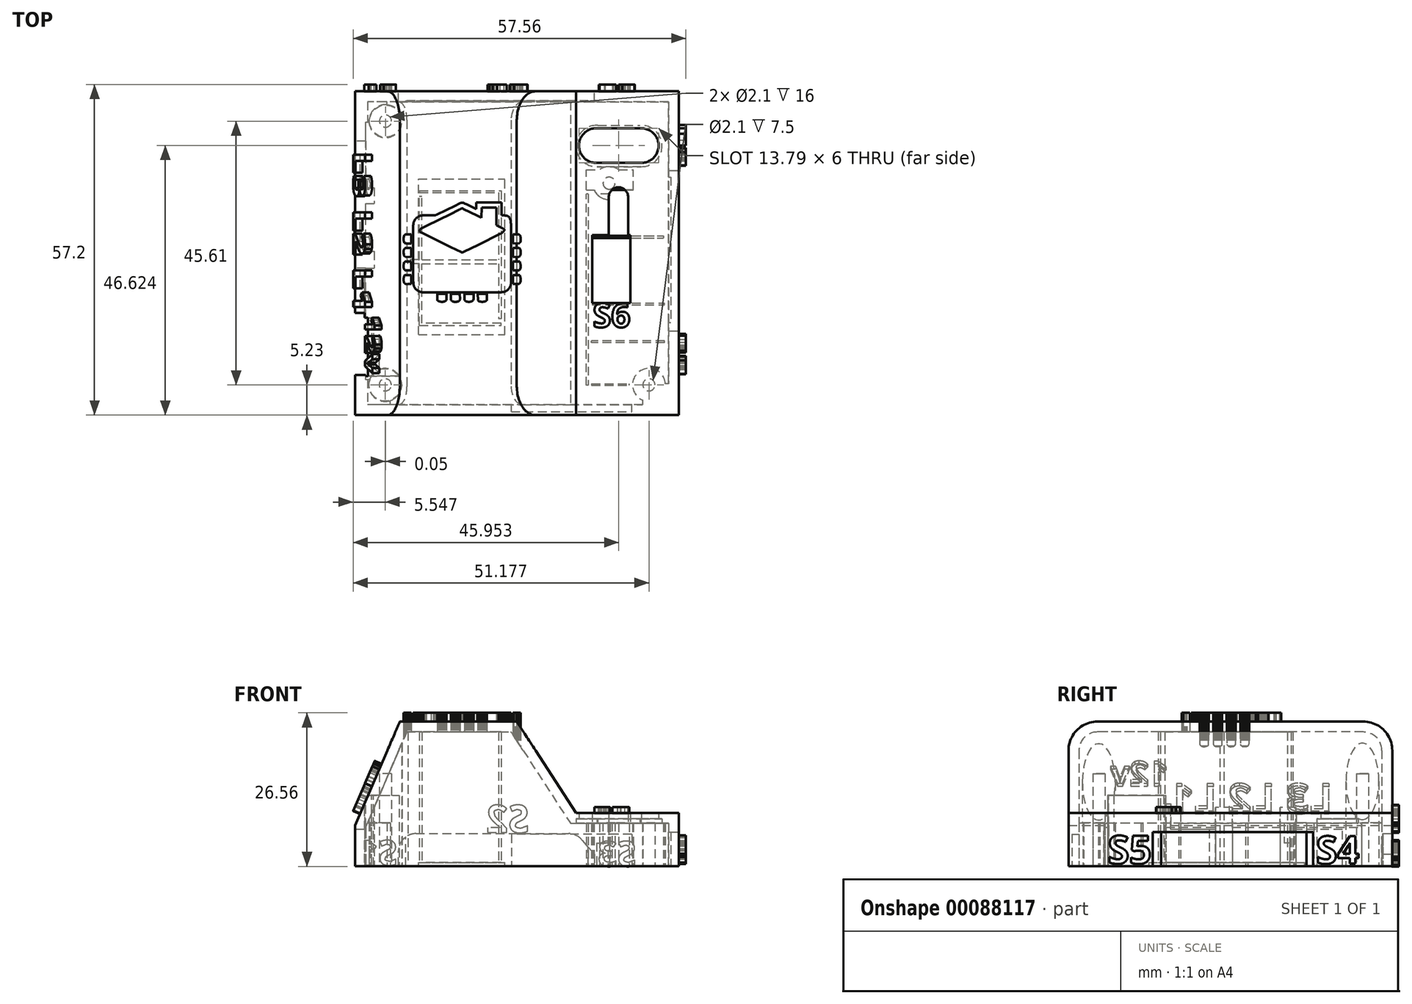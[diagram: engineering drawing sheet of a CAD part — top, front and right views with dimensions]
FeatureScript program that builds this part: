
annotation { "Feature Type Name" : "Feature", "Feature Type Description" : "" }
export const myFeature = defineFeature(function(context is Context, id is Id, definition is map)
    precondition{}
    {
        {
            var Q0;
            Q0=qCreatedBy(makeId("Top.planeOp"),FACE);
            var sketch = newSketch(context, id + "F0", { "sketchPlane" : qUnion([Q0])});
            skLineSegment(sketch, "E0.rect.bottom", {"start": v(22.84, -21.13) * mm, "end": v(-26.83, -21.13) * mm});
            skLineSegment(sketch, "E0.rect.top", {"start": v(22.84, 28.7) * mm, "end": v(-26.83, 28.7) * mm});
            skLineSegment(sketch, "E0.rect.left", {"start": v(22.84, -21.13) * mm, "end": v(22.84, 28.7) * mm});
            skPoint(sketch, "E0.rect.middle", {"position": v(-2, 3.78) * mm});
            skCircle(sketch, "E1", {"center": v(-24.81, -18.99) * mm, "radius": 1.05 * mm});
            skCircle(sketch, "E2", {"center": v(-24.76, 26.62) * mm, "radius": 1.05 * mm});
            skCircle(sketch, "E3", {"center": v(13.92, 15.91) * mm, "radius": 1.05 * mm});
            skLineSegment(sketch, "E4", {"start": v(-2, -21.13) * mm, "end": v(-2, -18.21) * mm});
            skCircle(sketch, "E5.MirrorC", {"center": v(20.82, -18.99) * mm, "radius": 1.05 * mm});
            skLineSegment(sketch, "E6.rect.bottom", {"start": v(24.75, -22.97) * mm, "end": v(-28.75, -22.97) * mm});
            skLineSegment(sketch, "E6.rect.top", {"start": v(24.75, 30.53) * mm, "end": v(-28.75, 30.53) * mm});
            skLineSegment(sketch, "E6.rect.left", {"start": v(24.75, -22.97) * mm, "end": v(24.75, 30.53) * mm});
            skLineSegment(sketch, "E6.rect.right", {"start": v(-28.75, -22.97) * mm, "end": v(-28.75, 30.53) * mm});
            skLineSegment(sketch, "E7.rect.bottom", {"start": v(26, -24.22) * mm, "end": v(-30, -24.22) * mm});
            skLineSegment(sketch, "E7.rect.top", {"start": v(26, 31.78) * mm, "end": v(-30, 31.78) * mm});
            skLineSegment(sketch, "E7.rect.left", {"start": v(26, -24.22) * mm, "end": v(26, 31.78) * mm});
            skLineSegment(sketch, "E7.rect.right", {"start": v(-30, -24.22) * mm, "end": v(-30, 31.78) * mm});
            skPoint(sketch, "E8", {"position": v(8.65, 14) * mm});
            skSolve(sketch);
        }
        {
            var Q0;
            Q0=qSketchRegion(id+"F0",true);
            var Q1;
            Q1=makeQuery(id+"F0.imprint","IMPRINT",FACE,{"disambiguationData":[TD([[makeQuery(id+"F0.imprint","IMPRINT",EDGE,{"derivedFrom":sQuery(id+"F0.wireOp",EDGE,"E1")}),-1.0]])]});
            extrude(context, id + "F1", {"entities" : qUnion([Q0, Q1]), "depth" : 25 * mm});
        }
        {
            var Q0;
            Q0=qCreatedBy(makeId("Front.planeOp"),FACE);
            var sketch = newSketch(context, id + "F2", { "sketchPlane" : qUnion([Q0])});
            skLineSegment(sketch, "E9", {"start": v(0, 0) * mm, "end": v(0, 7) * mm});
            skLineSegment(sketch, "E10", {"start": v(0, 7) * mm, "end": v(26.03, 7) * mm});
            skLineSegment(sketch, "E11", {"start": v(26.03, 9.19) * mm, "end": v(26.03, 25.51) * mm});
            skLineSegment(sketch, "E12", {"start": v(15.3, 7) * mm, "end": v(26.03, 7) * mm});
            skLineSegment(sketch, "E13", {"start": v(0, 7) * mm, "end": v(-30.02, 7) * mm});
            skLineSegment(sketch, "E14", {"start": v(-30.02, 7) * mm, "end": v(-22.06, 25.51) * mm});
            skLineSegment(sketch, "E15", {"start": v(-22.06, 25.51) * mm, "end": v(-2.39, 25.51) * mm});
            skLineSegment(sketch, "E16", {"start": v(26.03, 25.51) * mm, "end": v(-2.39, 25.51) * mm});
            skLineSegment(sketch, "E17", {"start": v(-22.06, 25.51) * mm, "end": v(-30.02, 25.51) * mm});
            skLineSegment(sketch, "E18", {"start": v(-30.02, 25.51) * mm, "end": v(-30.02, 7) * mm});
            skLineSegment(sketch, "E19", {"start": v(18.06, 10.7) * mm, "end": v(18.04, 10.7) * mm});
            skLineSegment(sketch, "E20", {"start": v(19.86, 9.19) * mm, "end": v(8.2, 9.19) * mm});
            skLineSegment(sketch, "E21", {"start": v(8.2, 9.19) * mm, "end": v(-2.39, 25.51) * mm});
            skLineSegment(sketch, "E22", {"start": v(19.86, 9.19) * mm, "end": v(26.03, 9.19) * mm});
            skSolve(sketch);
        }
        {
            var Q0;
            Q0=makeQuery(id+"F2.imprint","IMPRINT",FACE,{"disambiguationData":[TD([[makeQuery(id+"F2.imprint","IMPRINT",EDGE,{"derivedFrom":sQuery(id+"F2.wireOp",EDGE,"E14")}),1.0]])]});
            var Q1;
            {var subQ0=sQuery(id+"F2.wireOp",EDGE,"E11");Q1=makeQuery(id+"F2.imprint","IMPRINT",FACE,{"disambiguationData":[TD([[makeQuery(id+"F2.imprint","IMPRINT",EDGE,{"derivedFrom":subQ0}),1.0]])]});}
            extrude(context, id + "F3", {"entities" : qUnion([Q0, Q1]), "operationType" : NewBodyOperationType.REMOVE, "endBound" : BoundingType.UP_TO_NEXT, "oppositeDirection" : true, "depth" : 25 * mm, "hasSecondDirection" : true, "secondDirectionOppositeDirection" : false, "secondDirectionDepth" : 25 * mm});
        }
        {
            var Q0;
            Q0=makeQuery(id+"F1.opExtrude","CAP_EDGE",EDGE,{"disambiguationData":[OSD([sQuery(id+"F0.wireOp",EDGE,"E7.rect.right")])],"isStart":false});
            var Q1;
            Q1=makeQuery(id+"F3.boolean.opBoolean","COPY",EDGE,{"derivedFrom":makeQuery(id+"F3.opExtrude","TWEAK_EDGE",EDGE,{"derivedFrom":[makeQuery(id+"F1.opExtrude","CAP_FACE",FACE,{"disambiguationData":[OSD([sQuery(id+"F0.wireOp",EDGE,"E1"),sQuery(id+"F0.wireOp",EDGE,"E2"),sQuery(id+"F0.wireOp",EDGE,"E3"),sQuery(id+"F0.wireOp",EDGE,"E5.MirrorC"),sQuery(id+"F0.wireOp",EDGE,"E7.rect.bottom"),sQuery(id+"F0.wireOp",EDGE,"E7.rect.top"),sQuery(id+"F0.wireOp",EDGE,"E7.rect.left"),sQuery(id+"F0.wireOp",EDGE,"E7.rect.right")])],"isStart":false}),makeQuery(id+"F2.imprint","IMPRINT",EDGE,{"derivedFrom":sQuery(id+"F2.wireOp",EDGE,"ff17f17f-c23f-4b7b-92e3-773d52701edb")})]})});
            var Q2;
            Q2=makeQuery(id+"F3.boolean.opBoolean","COPY",EDGE,{"derivedFrom":makeQuery(id+"F3.opExtrude","TWEAK_EDGE",EDGE,{"derivedFrom":[makeQuery(id+"F1.opExtrude","CAP_FACE",FACE,{"disambiguationData":[OSD([sQuery(id+"F0.wireOp",EDGE,"E1"),sQuery(id+"F0.wireOp",EDGE,"E2"),sQuery(id+"F0.wireOp",EDGE,"E3"),sQuery(id+"F0.wireOp",EDGE,"E5.MirrorC"),sQuery(id+"F0.wireOp",EDGE,"E7.rect.bottom"),sQuery(id+"F0.wireOp",EDGE,"E7.rect.top"),sQuery(id+"F0.wireOp",EDGE,"E7.rect.left"),sQuery(id+"F0.wireOp",EDGE,"E7.rect.right")])],"isStart":false}),makeQuery(id+"F2.imprint","IMPRINT",EDGE,{"derivedFrom":sQuery(id+"F2.wireOp",EDGE,"7c30f75c-de24-4105-9ec6-0528e7197d9e")})]})});
            var Q3;
            {var subQ0=sQuery(id+"F2.wireOp",EDGE,"cpQ2IQLn-lepx-jHqE-Occg-QwCyzWVKbBFz");var subQ1=sQuery(id+"F2.wireOp",EDGE,"9136473a-ce9f-4df1-8e41-d79c079f6f02");var subQ2=makeQuery(id+"F2.imprint","INTERSECT",VERTEX,{"disambiguationData":[OD(0.0)],"derivedFrom":[subQ1,subQ0]});var subQ4=makeQuery(id+"F2.imprint","INTERSECT",VERTEX,{"disambiguationData":[OD(1.0)],"derivedFrom":[subQ1,subQ0]});Q3=makeQuery(id+"F3.boolean.opBoolean","COPY",EDGE,{"derivedFrom":makeQuery(id+"F3.opExtrude","TWEAK_EDGE",EDGE,{"derivedFrom":[makeQuery(id+"F1.opExtrude","CAP_FACE",FACE,{"disambiguationData":[OSD([sQuery(id+"F0.wireOp",EDGE,"E1"),sQuery(id+"F0.wireOp",EDGE,"E2"),sQuery(id+"F0.wireOp",EDGE,"E3"),sQuery(id+"F0.wireOp",EDGE,"E5.MirrorC"),sQuery(id+"F0.wireOp",EDGE,"E7.rect.bottom"),sQuery(id+"F0.wireOp",EDGE,"E7.rect.top"),sQuery(id+"F0.wireOp",EDGE,"E7.rect.left"),sQuery(id+"F0.wireOp",EDGE,"E7.rect.right")])],"isStart":false}),makeQuery(id+"F2.imprint","IMPRINT",EDGE,{"disambiguationData":[TD([[subQ4,1.0]])],"derivedFrom":subQ0}),makeQuery(id+"F2.imprint","IMPRINT",EDGE,{"disambiguationData":[TD([[subQ2,1.0]])],"derivedFrom":subQ0}),makeQuery(id+"F2.imprint","IMPRINT",EDGE,{"disambiguationData":[TD([[subQ2,-1.0]])],"derivedFrom":subQ0})]})});}
            var Q4;
            {var subQ0=sQuery(id+"F2.wireOp",EDGE,"cpQ2IQLn-lepx-jHqE-Occg-QwCyzWVKbBFz");var subQ1=sQuery(id+"F2.wireOp",EDGE,"9136473a-ce9f-4df1-8e41-d79c079f6f02");var subQ2=makeQuery(id+"F2.imprint","INTERSECT",VERTEX,{"disambiguationData":[OD(0.0)],"derivedFrom":[subQ1,subQ0]});var subQ3=sQuery(id+"F2.wireOp",EDGE,"7c30f75c-de24-4105-9ec6-0528e7197d9e");var subQ4=makeQuery(id+"F2.imprint","INTERSECT",VERTEX,{"derivedFrom":[subQ3,subQ0]});var subQ5=makeQuery(id+"F2.imprint","INTERSECT",VERTEX,{"disambiguationData":[OD(1.0)],"derivedFrom":[subQ1,subQ0]});Q4=makeQuery(id+"F3.boolean.opBoolean","COPY",EDGE,{"derivedFrom":makeQuery(id+"F3.opExtrude","TWEAK_EDGE",EDGE,{"disambiguationData":[OD(0.0)],"derivedFrom":[makeQuery(id+"F2.imprint","IMPRINT",EDGE,{"disambiguationData":[TD([[subQ4,1.0]])],"derivedFrom":subQ3}),makeQuery(id+"F2.imprint","IMPRINT",EDGE,{"disambiguationData":[TD([[subQ5,1.0]])],"derivedFrom":subQ0}),makeQuery(id+"F2.imprint","IMPRINT",EDGE,{"disambiguationData":[TD([[subQ2,1.0]])],"derivedFrom":subQ0}),makeQuery(id+"F2.imprint","IMPRINT",EDGE,{"disambiguationData":[TD([[subQ2,-1.0]])],"derivedFrom":subQ0})]})});}
            var Q5;
            {var subQ0=sQuery(id+"F2.wireOp",EDGE,"cpQ2IQLn-lepx-jHqE-Occg-QwCyzWVKbBFz");var subQ1=sQuery(id+"F2.wireOp",EDGE,"9136473a-ce9f-4df1-8e41-d79c079f6f02");var subQ2=makeQuery(id+"F2.imprint","INTERSECT",VERTEX,{"disambiguationData":[OD(0.0)],"derivedFrom":[subQ1,subQ0]});var subQ3=sQuery(id+"F2.wireOp",EDGE,"7c30f75c-de24-4105-9ec6-0528e7197d9e");var subQ4=makeQuery(id+"F2.imprint","INTERSECT",VERTEX,{"derivedFrom":[subQ3,subQ0]});var subQ5=makeQuery(id+"F2.imprint","INTERSECT",VERTEX,{"disambiguationData":[OD(1.0)],"derivedFrom":[subQ1,subQ0]});Q5=makeQuery(id+"F3.boolean.opBoolean","COPY",EDGE,{"derivedFrom":makeQuery(id+"F3.opExtrude","TWEAK_EDGE",EDGE,{"disambiguationData":[OD(1.0)],"derivedFrom":[makeQuery(id+"F2.imprint","IMPRINT",EDGE,{"disambiguationData":[TD([[subQ4,1.0]])],"derivedFrom":subQ3}),makeQuery(id+"F2.imprint","IMPRINT",EDGE,{"disambiguationData":[TD([[subQ5,1.0]])],"derivedFrom":subQ0}),makeQuery(id+"F2.imprint","IMPRINT",EDGE,{"disambiguationData":[TD([[subQ2,1.0]])],"derivedFrom":subQ0}),makeQuery(id+"F2.imprint","IMPRINT",EDGE,{"disambiguationData":[TD([[subQ2,-1.0]])],"derivedFrom":subQ0})]})});}
            var Q6;
            Q6=makeQuery(id+"F1.opExtrude","CAP_EDGE",EDGE,{"disambiguationData":[OSD([sQuery(id+"F0.wireOp",EDGE,"E7.rect.bottom")])],"isStart":false});
            var Q7;
            {var subQ0=sQuery(id+"F2.wireOp",EDGE,"cpQ2IQLn-lepx-jHqE-Occg-QwCyzWVKbBFz");var subQ1=sQuery(id+"F2.wireOp",EDGE,"9136473a-ce9f-4df1-8e41-d79c079f6f02");var subQ2=makeQuery(id+"F2.imprint","INTERSECT",VERTEX,{"disambiguationData":[OD(0.0)],"derivedFrom":[subQ1,subQ0]});var subQ4=makeQuery(id+"F2.imprint","INTERSECT",VERTEX,{"disambiguationData":[OD(1.0)],"derivedFrom":[subQ1,subQ0]});Q7=makeQuery(id+"F3.boolean.opBoolean","COPY",EDGE,{"derivedFrom":makeQuery(id+"F3.opExtrude","TWEAK_EDGE",EDGE,{"derivedFrom":[makeQuery(id+"F1.opExtrude","SWEPT_FACE",FACE,{"disambiguationData":[OSD([sQuery(id+"F0.wireOp",EDGE,"E7.rect.bottom")])]}),makeQuery(id+"F2.imprint","IMPRINT",EDGE,{"disambiguationData":[TD([[subQ4,1.0]])],"derivedFrom":subQ0}),makeQuery(id+"F2.imprint","IMPRINT",EDGE,{"disambiguationData":[TD([[subQ2,1.0]])],"derivedFrom":subQ0}),makeQuery(id+"F2.imprint","IMPRINT",EDGE,{"disambiguationData":[TD([[subQ2,-1.0]])],"derivedFrom":subQ0})]})});}
            var Q8;
            Q8=makeQuery(id+"F1.opExtrude","CAP_EDGE",EDGE,{"disambiguationData":[OSD([sQuery(id+"F0.wireOp",EDGE,"E7.rect.top")])],"isStart":false});
            var Q9;
            {var subQ0=sQuery(id+"F2.wireOp",EDGE,"cpQ2IQLn-lepx-jHqE-Occg-QwCyzWVKbBFz");var subQ1=sQuery(id+"F2.wireOp",EDGE,"9136473a-ce9f-4df1-8e41-d79c079f6f02");var subQ2=makeQuery(id+"F2.imprint","INTERSECT",VERTEX,{"disambiguationData":[OD(0.0)],"derivedFrom":[subQ1,subQ0]});var subQ4=makeQuery(id+"F2.imprint","INTERSECT",VERTEX,{"disambiguationData":[OD(1.0)],"derivedFrom":[subQ1,subQ0]});Q9=makeQuery(id+"F3.boolean.opBoolean","COPY",EDGE,{"derivedFrom":makeQuery(id+"F3.opExtrude","TWEAK_EDGE",EDGE,{"derivedFrom":[makeQuery(id+"F1.opExtrude","SWEPT_FACE",FACE,{"disambiguationData":[OSD([sQuery(id+"F0.wireOp",EDGE,"E7.rect.top")])]}),makeQuery(id+"F2.imprint","IMPRINT",EDGE,{"disambiguationData":[TD([[subQ4,1.0]])],"derivedFrom":subQ0}),makeQuery(id+"F2.imprint","IMPRINT",EDGE,{"disambiguationData":[TD([[subQ2,1.0]])],"derivedFrom":subQ0}),makeQuery(id+"F2.imprint","IMPRINT",EDGE,{"disambiguationData":[TD([[subQ2,-1.0]])],"derivedFrom":subQ0})]})});}
            var Q10;
            Q10=makeQuery(id+"F3.boolean.opBoolean","COPY",EDGE,{"derivedFrom":makeQuery(id+"F3.opExtrude","TWEAK_EDGE",EDGE,{"derivedFrom":[makeQuery(id+"F1.opExtrude","CAP_FACE",FACE,{"disambiguationData":[OSD([sQuery(id+"F0.wireOp",EDGE,"E1"),sQuery(id+"F0.wireOp",EDGE,"E2"),sQuery(id+"F0.wireOp",EDGE,"E3"),sQuery(id+"F0.wireOp",EDGE,"E5.MirrorC"),sQuery(id+"F0.wireOp",EDGE,"E7.rect.bottom"),sQuery(id+"F0.wireOp",EDGE,"E7.rect.top"),sQuery(id+"F0.wireOp",EDGE,"E7.rect.left"),sQuery(id+"F0.wireOp",EDGE,"E7.rect.right")])],"isStart":false}),makeQuery(id+"F2.imprint","IMPRINT",EDGE,{"derivedFrom":sQuery(id+"F2.wireOp",EDGE,"99fa5713-44e2-4710-8a3e-a5a5802f03ed")})]})});
            var Q11;
            Q11=makeQuery(id+"F3.boolean.opBoolean","COPY",EDGE,{"derivedFrom":makeQuery(id+"F3.opExtrude","TWEAK_EDGE",EDGE,{"derivedFrom":[makeQuery(id+"F1.opExtrude","CAP_FACE",FACE,{"disambiguationData":[OSD([sQuery(id+"F0.wireOp",EDGE,"E1"),sQuery(id+"F0.wireOp",EDGE,"E2"),sQuery(id+"F0.wireOp",EDGE,"E3"),sQuery(id+"F0.wireOp",EDGE,"E5.MirrorC"),sQuery(id+"F0.wireOp",EDGE,"E7.rect.bottom"),sQuery(id+"F0.wireOp",EDGE,"E7.rect.top"),sQuery(id+"F0.wireOp",EDGE,"E7.rect.left"),sQuery(id+"F0.wireOp",EDGE,"E7.rect.right")])],"isStart":false}),makeQuery(id+"F2.imprint","IMPRINT",EDGE,{"derivedFrom":sQuery(id+"F2.wireOp",EDGE,"E14")})]})});
            var Q12;
            Q12=makeQuery(id+"F3.boolean.opBoolean","COPY",EDGE,{"derivedFrom":makeQuery(id+"F3.opExtrude","TWEAK_EDGE",EDGE,{"derivedFrom":[makeQuery(id+"F1.opExtrude","CAP_FACE",FACE,{"disambiguationData":[OSD([sQuery(id+"F0.wireOp",EDGE,"E1"),sQuery(id+"F0.wireOp",EDGE,"E2"),sQuery(id+"F0.wireOp",EDGE,"E3"),sQuery(id+"F0.wireOp",EDGE,"E5.MirrorC"),sQuery(id+"F0.wireOp",EDGE,"E7.rect.bottom"),sQuery(id+"F0.wireOp",EDGE,"E7.rect.top"),sQuery(id+"F0.wireOp",EDGE,"E7.rect.left"),sQuery(id+"F0.wireOp",EDGE,"E7.rect.right")])],"isStart":false}),makeQuery(id+"F2.imprint","IMPRINT",EDGE,{"derivedFrom":sQuery(id+"F2.wireOp",EDGE,"E21")})]})});
            var Q13;
            Q13=makeQuery(id+"F3.boolean.opBoolean","COPY",EDGE,{"derivedFrom":makeQuery(id+"F3.opExtrude","TWEAK_EDGE",EDGE,{"derivedFrom":[makeQuery(id+"F2.imprint","IMPRINT",EDGE,{"derivedFrom":sQuery(id+"F2.wireOp",EDGE,"E20")}),makeQuery(id+"F2.imprint","IMPRINT",EDGE,{"derivedFrom":sQuery(id+"F2.wireOp",EDGE,"E21")})]})});
            var Q14;
            Q14=makeQuery(id+"F3.boolean.opBoolean","COPY",EDGE,{"derivedFrom":makeQuery(id+"F3.opExtrude","TWEAK_EDGE",EDGE,{"derivedFrom":[makeQuery(id+"F1.opExtrude","SWEPT_FACE",FACE,{"disambiguationData":[OSD([sQuery(id+"F0.wireOp",EDGE,"E7.rect.bottom")])]}),makeQuery(id+"F2.imprint","IMPRINT",EDGE,{"derivedFrom":sQuery(id+"F2.wireOp",EDGE,"E21")})]})});
            var Q15;
            Q15=makeQuery(id+"F3.boolean.opBoolean","COPY",EDGE,{"derivedFrom":makeQuery(id+"F3.opExtrude","TWEAK_EDGE",EDGE,{"derivedFrom":[makeQuery(id+"F1.opExtrude","SWEPT_FACE",FACE,{"disambiguationData":[OSD([sQuery(id+"F0.wireOp",EDGE,"E7.rect.top")])]}),makeQuery(id+"F2.imprint","IMPRINT",EDGE,{"derivedFrom":sQuery(id+"F2.wireOp",EDGE,"E21")})]})});
            var Q16;
            Q16=makeQuery(id+"F3.boolean.opBoolean","COPY",EDGE,{"derivedFrom":makeQuery(id+"F3.opExtrude","TWEAK_EDGE",EDGE,{"derivedFrom":[makeQuery(id+"F1.opExtrude","SWEPT_FACE",FACE,{"disambiguationData":[OSD([sQuery(id+"F0.wireOp",EDGE,"E7.rect.left")])]}),makeQuery(id+"F2.imprint","IMPRINT",EDGE,{"derivedFrom":sQuery(id+"F2.wireOp",EDGE,"E20")}),makeQuery(id+"F2.imprint","IMPRINT",EDGE,{"derivedFrom":sQuery(id+"F2.wireOp",EDGE,"E22")})]})});
            var Q17;
            Q17=makeQuery(id+"F3.boolean.opBoolean","COPY",EDGE,{"derivedFrom":makeQuery(id+"F3.opExtrude","TWEAK_EDGE",EDGE,{"derivedFrom":[makeQuery(id+"F2.imprint","IMPRINT",EDGE,{"derivedFrom":sQuery(id+"F2.wireOp",EDGE,"E20")}),makeQuery(id+"F2.imprint","IMPRINT",EDGE,{"derivedFrom":sQuery(id+"F2.wireOp",EDGE,"E21")}),makeQuery(id+"F2.imprint","IMPRINT",EDGE,{"derivedFrom":sQuery(id+"F2.wireOp",EDGE,"E22")})]})});
            fillet(context, id + "F4", {"entities" : qUnion([Q0, Q1, Q2, Q3, Q4, Q5, Q6, Q7, Q8, Q9, Q10, Q11, Q12, Q13, Q14, Q15, Q16, Q17]), "radius" : 5 * mm, "tangentPropagation" : true, "allowEdgeOverflow" : false});
        }
        {
            var Q0;
            Q0=makeQuery(id+"F1.opExtrude","SWEPT_BODY",BODY,{"disambiguationData":[OSD([sQuery(id+"F0.wireOp",EDGE,"E1"),sQuery(id+"F0.wireOp",EDGE,"E2"),sQuery(id+"F0.wireOp",EDGE,"E3"),sQuery(id+"F0.wireOp",EDGE,"E5.MirrorC"),sQuery(id+"F0.wireOp",EDGE,"E7.rect.bottom"),sQuery(id+"F0.wireOp",EDGE,"E7.rect.top"),sQuery(id+"F0.wireOp",EDGE,"E7.rect.left"),sQuery(id+"F0.wireOp",EDGE,"E7.rect.right")])]});
            transform(context, id + "F5", {"entities" : qUnion([Q0]), "transformType" : TransformType.TRANSLATION_3D, "dx" : -5 * mm, "dy" : -12 * mm, "dz" : 0 * mm, "makeCopy" : false});
        }
        {
            var Q0;
            Q0=makeQuery(id+"F1.opExtrude","CAP_FACE",FACE,{"disambiguationData":[OSD([sQuery(id+"F0.wireOp",EDGE,"E1"),sQuery(id+"F0.wireOp",EDGE,"E2"),sQuery(id+"F0.wireOp",EDGE,"E3"),sQuery(id+"F0.wireOp",EDGE,"E5.MirrorC"),sQuery(id+"F0.wireOp",EDGE,"E7.rect.bottom"),sQuery(id+"F0.wireOp",EDGE,"E7.rect.top"),sQuery(id+"F0.wireOp",EDGE,"E7.rect.left"),sQuery(id+"F0.wireOp",EDGE,"E7.rect.right")])],"isStart":true});
            shell(context, id + "F6", {"entities" : qUnion([Q0]), "thickness" : 1.8 * mm});
        }
        {
            var Q0;
            Q0=makeQuery(id+"F1.opExtrude","SWEPT_FACE",FACE,{"disambiguationData":[OSD([sQuery(id+"F0.wireOp",EDGE,"E7.rect.left")])]});
            cPlane(context, id + "F7", {"entities" : qUnion([Q0]), "cplaneType" : CPlaneType.OFFSET, "offset" : 0 * mm, "width" : 150 * mm, "height" : 150 * mm});
        }
        {
            var Q0;
            Q0=qCreatedBy(id+"F7.planeOp",FACE);
            var sketch = newSketch(context, id + "F8", { "sketchPlane" : qUnion([Q0])});
            skLineSegment(sketch, "E23.bottom", {"start": v(6.92, 0) * mm, "end": v(-20.2, 0) * mm});
            skLineSegment(sketch, "E23.top", {"start": v(6.12, 5.87) * mm, "end": v(-20.2, 5.87) * mm});
            skLineSegment(sketch, "E24", {"start": v(-20.2, 5.87) * mm, "end": v(-21.64, 5.87) * mm});
            skLineSegment(sketch, "E25", {"start": v(-21.64, 5.87) * mm, "end": v(-21.64, 0) * mm});
            skLineSegment(sketch, "E26", {"start": v(-21.64, 0) * mm, "end": v(-20.2, 0) * mm});
            skLineSegment(sketch, "E27", {"start": v(-20.2, 5.87) * mm, "end": v(-20.2, 0) * mm});
            skLineSegment(sketch, "E28", {"start": v(6.12, 5.87) * mm, "end": v(6.12, 0) * mm});
            skPoint(sketch, "E29.orphan", {"position": v(7.84, 0) * mm});
            skLineSegment(sketch, "E30", {"start": v(4.97, 0) * mm, "end": v(4.97, 5.87) * mm});
            skSolve(sketch);
        }
        {
            var Q0;
            Q0=qSketchRegion(id+"F8",true);
            extrude(context, id + "F9", {"entities" : qUnion([Q0]), "operationType" : NewBodyOperationType.REMOVE, "oppositeDirection" : true, "depth" : (1.7 - 0.3) * mm});
        }
        {
            var Q0;
            Q0=makeQuery(id+"F8.imprint","IMPRINT",FACE,{"disambiguationData":[TD([[makeQuery(id+"F8.imprint","IMPRINT",EDGE,{"derivedFrom":sQuery(id+"F8.wireOp",EDGE,"E24")}),1.0]])]});
            var Q1;
            {var subQ0=sQuery(id+"F8.wireOp",EDGE,"E23.left");Q1=makeQuery(id+"F8.imprint","IMPRINT",FACE,{"disambiguationData":[TD([[makeQuery(id+"F8.imprint","IMPRINT",EDGE,{"derivedFrom":subQ0}),1.0]])]});}
            var Q2;
            {var subQ0=sQuery(id+"F8.wireOp",EDGE,"4UiORLbo-slaH-JSft-xh6I-61qYCNnPId7j");Q2=makeQuery(id+"F8.imprint","IMPRINT",FACE,{"disambiguationData":[TD([[makeQuery(id+"F8.imprint","IMPRINT",EDGE,{"derivedFrom":subQ0}),1.0]])]});}
            var Q3;
            {var subQ0=sQuery(id+"F8.wireOp",EDGE,"E28");Q3=makeQuery(id+"F8.imprint","IMPRINT",FACE,{"disambiguationData":[TD([[makeQuery(id+"F8.imprint","IMPRINT",EDGE,{"derivedFrom":subQ0}),-1.0]])]});}
            extrude(context, id + "F10", {"entities" : qUnion([Q0, Q1, Q2, Q3]), "operationType" : NewBodyOperationType.REMOVE, "oppositeDirection" : true, "depth" : 2 * mm});
        }
        {
            var Q0;
            Q0=makeQuery(id+"F1.opExtrude","SWEPT_FACE",FACE,{"disambiguationData":[OSD([sQuery(id+"F0.wireOp",EDGE,"E7.rect.right")])]});
            cPlane(context, id + "F11", {"entities" : qUnion([Q0]), "cplaneType" : CPlaneType.OFFSET, "offset" : 0 * mm, "width" : 150 * mm, "height" : 150 * mm});
        }
        {
            var Q0;
            Q0=qCreatedBy(id+"F11.planeOp",FACE);
            var sketch = newSketch(context, id + "F12", { "sketchPlane" : qUnion([Q0])});
            skLineSegment(sketch, "E31.top", {"start": v(-11.15, 6.31) * mm, "end": v(-3.45, 6.31) * mm});
            skLineSegment(sketch, "E32", {"start": v(27.25, 11.15) * mm, "end": v(27.25, 11.15) * mm});
            skLineSegment(sketch, "E33", {"start": v(-11.15, 0) * mm, "end": v(-11.15, 6.31) * mm});
            skPoint(sketch, "E34.start.orphan", {"position": v(-15.15, 0) * mm});
            skLineSegment(sketch, "E35", {"start": v(29.28, 0) * mm, "end": v(-11.15, 0) * mm});
            skLineSegment(sketch, "E36", {"start": v(-10.29, 6.31) * mm, "end": v(-10.29, 0) * mm});
            skLineSegment(sketch, "E37", {"start": v(19.35, 12.2) * mm, "end": v(29.28, 12.2) * mm});
            skLineSegment(sketch, "E38", {"start": v(-11.15, 3.16) * mm, "end": v(-3.45, 3.16) * mm, "construction": true});
            skLineSegment(sketch, "E39", {"start": v(-3.45, 3.16) * mm, "end": v(-0.05, 3.16) * mm, "construction": true});
            skLineSegment(sketch, "E40", {"start": v(-0.05, 3.16) * mm, "end": v(7.65, 3.16) * mm, "construction": true});
            skLineSegment(sketch, "E41", {"start": v(7.65, 3.16) * mm, "end": v(11.05, 3.16) * mm, "construction": true});
            skLineSegment(sketch, "E42.trimOffspring", {"start": v(11.05, 6.31) * mm, "end": v(18.53, 6.31) * mm});
            skLineSegment(sketch, "E43", {"start": v(11.9, 6.31) * mm, "end": v(11.9, 0) * mm});
            skLineSegment(sketch, "E44", {"start": v(0, 6.31) * mm, "end": v(7.65, 6.31) * mm});
            skLineSegment(sketch, "E45", {"start": v(7.65, 0) * mm, "end": v(0, 0) * mm});
            skLineSegment(sketch, "E46", {"start": v(-3.45, 0) * mm, "end": v(-11.15, 0) * mm});
            skLineSegment(sketch, "E47", {"start": v(30.08, 0) * mm, "end": v(11.05, 0) * mm});
            skLineSegment(sketch, "E48.bottom", {"start": v(-0.32, 0) * mm, "end": v(-3.15, 0) * mm});
            skLineSegment(sketch, "E48.top", {"start": v(-0.32, 6.31) * mm, "end": v(-3.15, 6.31) * mm});
            skLineSegment(sketch, "E48.left", {"start": v(-0.32, 0) * mm, "end": v(-0.32, 6.31) * mm});
            skLineSegment(sketch, "E48.right", {"start": v(-3.15, 0) * mm, "end": v(-3.15, 6.31) * mm});
            skLineSegment(sketch, "E49.bottom", {"start": v(10.8, 0) * mm, "end": v(7.92, 0) * mm});
            skLineSegment(sketch, "E49.top", {"start": v(10.8, 6.31) * mm, "end": v(7.92, 6.31) * mm});
            skLineSegment(sketch, "E49.left", {"start": v(10.8, 0) * mm, "end": v(10.8, 6.31) * mm});
            skLineSegment(sketch, "E49.right", {"start": v(7.92, 0) * mm, "end": v(7.92, 6.31) * mm});
            skLineSegment(sketch, "E50", {"start": v(-3.45, 6.31) * mm, "end": v(11.05, 6.31) * mm});
            skLineSegment(sketch, "E51", {"start": v(29.28, 12.2) * mm, "end": v(29.28, 0) * mm});
            skPoint(sketch, "E52.end.orphan", {"position": v(30.08, 11.15) * mm});
            skPoint(sketch, "E52.start.orphan", {"position": v(30.08, 12.2) * mm});
            skLineSegment(sketch, "E53", {"start": v(18.53, 6.31) * mm, "end": v(18.53, 12.2) * mm});
            skLineSegment(sketch, "E54", {"start": v(18.53, 12.2) * mm, "end": v(19.35, 12.2) * mm});
            skPoint(sketch, "E55.start.orphan", {"position": v(19.35, 11.15) * mm});
            skPoint(sketch, "E56.end.orphan", {"position": v(19.35, 0) * mm});
            skPoint(sketch, "E56.start.orphan", {"position": v(19.35, 6.31) * mm});
            skLineSegment(sketch, "E57", {"start": v(28.38, 0) * mm, "end": v(28.38, 12.2) * mm});
            skLineSegment(sketch, "E58", {"start": v(19.35, 12.2) * mm, "end": v(19.35, 0) * mm});
            skSolve(sketch);
        }
        {
            var Q0;
            {var subQ0=sQuery(id+"F12.wireOp",EDGE,"E33");Q0=makeQuery(id+"F12.imprint","IMPRINT",FACE,{"disambiguationData":[TD([[makeQuery(id+"F12.imprint","IMPRINT",EDGE,{"derivedFrom":subQ0}),-1.0]])]});}
            var Q1;
            {var subQ1=sQuery(id+"F12.wireOp",EDGE,"E36");Q1=makeQuery(id+"F12.imprint","IMPRINT",FACE,{"disambiguationData":[TD([[makeQuery(id+"F12.imprint","IMPRINT",EDGE,{"derivedFrom":subQ1}),1.0]])]});}
            var Q2;
            {var subQ0=sQuery(id+"F12.wireOp",EDGE,"LVVauTd6-uSLQ-SWm0-nvuu-HrEgJgk2loCY");Q2=makeQuery(id+"F12.imprint","IMPRINT",FACE,{"disambiguationData":[TD([[makeQuery(id+"F12.imprint","IMPRINT",EDGE,{"derivedFrom":subQ0}),-1.0]])]});}
            var Q3;
            Q3=makeQuery(id+"F12.imprint","IMPRINT",FACE,{"disambiguationData":[TD([[makeQuery(id+"F12.imprint","IMPRINT",EDGE,{"derivedFrom":sQuery(id+"F12.wireOp",EDGE,"Bzj0w9RH-aYdH-ZF7y-Z4mK-Pif1xP8myCSu")}),1.0]])]});
            var Q4;
            {var subQ2=sQuery(id+"F12.wireOp",EDGE,"E43");Q4=makeQuery(id+"F12.imprint","IMPRINT",FACE,{"disambiguationData":[TD([[makeQuery(id+"F12.imprint","IMPRINT",EDGE,{"derivedFrom":subQ2}),1.0]])]});}
            extrude(context, id + "F13", {"entities" : qUnion([Q0, Q1, Q2, Q3, Q4]), "operationType" : NewBodyOperationType.REMOVE, "oppositeDirection" : true, "depth" : 1.6 * mm});
        }
        {
            var Q0;
            {var subQ2=sQuery(id+"F12.wireOp",EDGE,"E57");Q0=makeQuery(id+"F12.imprint","IMPRINT",FACE,{"disambiguationData":[TD([[makeQuery(id+"F12.imprint","IMPRINT",EDGE,{"derivedFrom":subQ2}),1.0]])]});}
            var Q1;
            {var subQ0=sQuery(id+"F12.wireOp",EDGE,"E33");Q1=makeQuery(id+"F12.imprint","IMPRINT",FACE,{"disambiguationData":[TD([[makeQuery(id+"F12.imprint","IMPRINT",EDGE,{"derivedFrom":subQ0}),-1.0]])]});}
            var Q2;
            {var subQ1=sQuery(id+"F12.wireOp",EDGE,"E45");Q2=makeQuery(id+"F12.imprint","IMPRINT",FACE,{"disambiguationData":[TD([[makeQuery(id+"F12.imprint","IMPRINT",EDGE,{"derivedFrom":subQ1}),-1.0]])]});}
            var Q3;
            {var subQ3=sQuery(id+"F12.wireOp",EDGE,"E36");Q3=makeQuery(id+"F12.imprint","IMPRINT",FACE,{"disambiguationData":[TD([[makeQuery(id+"F12.imprint","IMPRINT",EDGE,{"derivedFrom":subQ3}),1.0]])]});}
            var Q4;
            {var subQ3=sQuery(id+"F12.wireOp",EDGE,"E43");Q4=makeQuery(id+"F12.imprint","IMPRINT",FACE,{"disambiguationData":[TD([[makeQuery(id+"F12.imprint","IMPRINT",EDGE,{"derivedFrom":subQ3}),-1.0]])]});}
            var Q5;
            {var subQ0=sQuery(id+"F12.wireOp",EDGE,"E51");Q5=makeQuery(id+"F12.imprint","IMPRINT",FACE,{"disambiguationData":[TD([[makeQuery(id+"F12.imprint","IMPRINT",EDGE,{"derivedFrom":subQ0}),-1.0]])]});}
            extrude(context, id + "F14", {"entities" : qUnion([Q0, Q1, Q2, Q3, Q4, Q5]), "operationType" : NewBodyOperationType.REMOVE, "oppositeDirection" : true, "depth" : 8 * mm});
        }
        {
            var Q0;
            Q0=qCreatedBy(makeId("Top.planeOp"),FACE);
            var sketch = newSketch(context, id + "F15", { "sketchPlane" : qUnion([Q0])});
            skLineSegment(sketch, "E59.bottom", {"start": v(-27.19, -29.45) * mm, "end": v(-33.17, -29.45) * mm});
            skLineSegment(sketch, "E59.top", {"start": v(-27.19, -20) * mm, "end": v(-33.17, -20) * mm});
            skLineSegment(sketch, "E59.left", {"start": v(-27.19, -29.45) * mm, "end": v(-27.19, -21.32) * mm});
            skLineSegment(sketch, "E59.right", {"start": v(-33.17, -29.45) * mm, "end": v(-33.17, -21.32) * mm});
            skLineSegment(sketch, "E60", {"start": v(-33.17, -20.99) * mm, "end": v(-27.19, -20.99) * mm});
            skLineSegment(sketch, "E61", {"start": v(-33.17, -21.32) * mm, "end": v(-27.19, -21.32) * mm});
            skLineSegment(sketch, "E62.trimOffspring", {"start": v(-27.19, -20.99) * mm, "end": v(-27.19, -20) * mm});
            skLineSegment(sketch, "E63.trimOffspring", {"start": v(-33.17, -20.99) * mm, "end": v(-33.17, -20) * mm});
            skSolve(sketch);
        }
        {
            var Q0;
            Q0=qSketchRegion(id+"F15",true);
            var Q1;
            {var subQ0=sQuery(id+"F12.wireOp",EDGE,"E37");Q1=makeQuery(id+"F14.boolean.opBoolean","COPY",FACE,{"derivedFrom":makeQuery(id+"F14.opExtrude","SWEPT_FACE",FACE,{"disambiguationData":[OSD([subQ0]),TDD([makeQuery(id+"F12.imprint","IMPRINT",EDGE,{"disambiguationData":[TD([[makeQuery(id+"F12.imprint","INTERSECT",VERTEX,{"derivedFrom":[subQ0,sQuery(id+"F12.wireOp",EDGE,"E52")]}),1.0]])],"derivedFrom":subQ0})])]})});}
            extrude(context, id + "F16", {"entities" : qUnion([Q0]), "operationType" : NewBodyOperationType.REMOVE, "endBound" : BoundingType.UP_TO_SURFACE, "endBoundEntityFace" : qUnion([Q1]), "depth" : 11.3 * mm});
        }
        {
            var Q0;
            Q0=makeQuery(id+"F1.opExtrude","SWEPT_FACE",FACE,{"disambiguationData":[OSD([sQuery(id+"F0.wireOp",EDGE,"E7.rect.top")])]});
            cPlane(context, id + "F17", {"entities" : qUnion([Q0]), "cplaneType" : CPlaneType.OFFSET, "offset" : 0 * mm, "width" : 150 * mm, "height" : 150 * mm});
        }
        {
            var Q0;
            Q0=qCreatedBy(id+"F17.planeOp",FACE);
            var sketch = newSketch(context, id + "F18", { "sketchPlane" : qUnion([Q0])});
            skLineSegment(sketch, "E64.bottom", {"start": v(-6.36, 0) * mm, "end": v(27.5, 0) * mm});
            skLineSegment(sketch, "E64.left", {"start": v(-6.36, 0) * mm, "end": v(-6.36, 2.05) * mm});
            skLineSegment(sketch, "E65", {"start": v(-5.32, 3.26) * mm, "end": v(-5.32, 0) * mm});
            skLineSegment(sketch, "E66", {"start": v(27.5, 2.61) * mm, "end": v(27.5, 0) * mm});
            skLineSegment(sketch, "E67", {"start": v(26.27, 5.04) * mm, "end": v(26.27, 0) * mm});
            skPoint(sketch, "E68.visualSharp", {"position": v(-6.36, 7.05) * mm});
            skLineSegment(sketch, "E69", {"start": v(-6.36, 2.05) * mm, "end": v(-4.17, 4.58) * mm});
            skLineSegment(sketch, "E70", {"start": v(24.5, 5.61) * mm, "end": v(-1.9, 5.61) * mm});
            skPoint(sketch, "E71.visualSharp", {"position": v(-3.28, 5.61) * mm});
            skArc(sketch, "E71.filletArc", {"start": v(-1.9, 5.61) * mm, "mid": v(-3.15, 5.34) * mm, "end": v(-4.17, 4.58) * mm});
            skPoint(sketch, "E72.visualSharp", {"position": v(27.5, 5.61) * mm});
            skArc(sketch, "E72.filletArc", {"start": v(27.5, 2.61) * mm, "mid": v(26.63, 4.73) * mm, "end": v(24.5, 5.61) * mm});
            skSolve(sketch);
        }
        {
            var Q0;
            Q0=qSketchRegion(id+"F18",true);
            extrude(context, id + "F19", {"entities" : qUnion([Q0]), "operationType" : NewBodyOperationType.REMOVE, "oppositeDirection" : true, "depth" : 1.6 * mm});
        }
        {
            var Q0;
            Q0=qCreatedBy(makeId("Top.planeOp"),FACE);
            var sketch = newSketch(context, id + "F20", { "sketchPlane" : qUnion([Q0])});
            skArc(sketch, "E73", {"start": v(6.16, 2.02) * mm, "mid": v(8.9, 0.56) * mm, "end": v(11.63, 2.02) * mm});
            skLineSegment(sketch, "E74", {"start": v(11.63, 2.02) * mm, "end": v(6.16, 2.02) * mm});
            skSolve(sketch);
        }
        {
            var Q0;
            Q0=qSketchRegion(id+"F20",true);
            extrude(context, id + "F21", {"entities" : qUnion([Q0]), "operationType" : NewBodyOperationType.REMOVE, "depth" : 4 * mm});
        }
        {
            var Q0;
            {var subQ0=sQuery(id+"F18.wireOp",EDGE,"E64.left");Q0=makeQuery(id+"F18.imprint","IMPRINT",FACE,{"disambiguationData":[TD([[makeQuery(id+"F18.imprint","IMPRINT",EDGE,{"derivedFrom":subQ0}),-1.0]])]});}
            var Q1;
            {var subQ0=sQuery(id+"F18.wireOp",EDGE,"E64.right");Q1=makeQuery(id+"F18.imprint","IMPRINT",FACE,{"disambiguationData":[TD([[makeQuery(id+"F18.imprint","IMPRINT",EDGE,{"derivedFrom":subQ0}),1.0]])]});}
            extrude(context, id + "F22", {"entities" : qUnion([Q0, Q1]), "operationType" : NewBodyOperationType.REMOVE, "oppositeDirection" : true, "depth" : 2 * mm});
        }
        {
            var Q0;
            Q0=qCreatedBy(makeId("Top.planeOp"),FACE);
            var sketch = newSketch(context, id + "F23", { "sketchPlane" : qUnion([Q0])});
            skLineSegment(sketch, "E75", {"start": v(21, 19.9) * mm, "end": v(21, 10.4) * mm, "construction": true});
            skLineSegment(sketch, "E76", {"start": v(12.22, 0) * mm, "end": v(12.22, -5.06) * mm});
            skLineSegment(sketch, "E77", {"start": v(12.22, 0) * mm, "end": v(12.22, 1.5) * mm});
            skArc(sketch, "E78", {"start": v(14.47, 7.42) * mm, "mid": v(17.49, 10.4) * mm, "end": v(14.5, 13.4) * mm});
            skArc(sketch, "E79", {"start": v(6.7, 13.4) * mm, "mid": v(3.7, 10.4) * mm, "end": v(6.7, 7.4) * mm});
            skLineSegment(sketch, "E80", {"start": v(14.5, 13.4) * mm, "end": v(6.7, 13.4) * mm});
            skLineSegment(sketch, "E81", {"start": v(6.7, 7.4) * mm, "end": v(14.54, 7.42) * mm});
            skLineSegment(sketch, "E82", {"start": v(6, -5.57) * mm, "end": v(6, -16.85) * mm});
            skLineSegment(sketch, "E83", {"start": v(12.6, -16.85) * mm, "end": v(6, -16.85) * mm});
            skPoint(sketch, "E84.center.orphan", {"position": v(10.72, -16.85) * mm});
            skLineSegment(sketch, "E85", {"start": v(12.6, -5.57) * mm, "end": v(12.6, -16.85) * mm});
            skLineSegment(sketch, "E86", {"start": v(8.87, -5.06) * mm, "end": v(8.87, 1.5) * mm});
            skArc(sketch, "E87", {"start": v(12.22, 1.5) * mm, "mid": v(10.54, 3.17) * mm, "end": v(8.87, 1.5) * mm});
            skPoint(sketch, "E88.orphan", {"position": v(12.22, -16.85) * mm});
            skLineSegment(sketch, "E89", {"start": v(0, 0) * mm, "end": v(0, 19.9) * mm, "construction": true});
            skLineSegment(sketch, "E90", {"start": v(0, 19.9) * mm, "end": v(21, 19.9) * mm, "construction": true});
            skLineSegment(sketch, "E91", {"start": v(14.5, 10.4) * mm, "end": v(21, 10.4) * mm, "construction": true});
            skLineSegment(sketch, "E92", {"start": v(8.87, -5.06) * mm, "end": v(6, -5.06) * mm});
            skLineSegment(sketch, "E93", {"start": v(6, -5.06) * mm, "end": v(6, -5.57) * mm});
            skLineSegment(sketch, "E94", {"start": v(12.22, -5.06) * mm, "end": v(12.6, -5.06) * mm});
            skLineSegment(sketch, "E95", {"start": v(12.6, -5.06) * mm, "end": v(12.6, -5.57) * mm});
            skSolve(sketch);
        }
        {
            var Q0;
            Q0=qSketchRegion(id+"F23",true);
            extrude(context, id + "F24", {"entities" : qUnion([Q0]), "operationType" : NewBodyOperationType.REMOVE, "depth" : 25 * mm});
        }
        {
            var Q0;
            Q0=qCreatedBy(makeId("Top.planeOp"),FACE);
            var sketch = newSketch(context, id + "F25", { "sketchPlane" : qUnion([Q0])});
            skLineSegment(sketch, "E96", {"start": v(18.49, -17.16) * mm, "end": v(5.97, -17.16) * mm});
            skLineSegment(sketch, "E97", {"start": v(18.49, -16.86) * mm, "end": v(5.97, -16.86) * mm});
            skLineSegment(sketch, "E98", {"start": v(12.44, -31.08) * mm, "end": v(5.87, -31.08) * mm});
            skLineSegment(sketch, "E99", {"start": v(12.44, -30.78) * mm, "end": v(5.87, -30.78) * mm});
            skLineSegment(sketch, "E100.bottom", {"start": v(-33.84, 14.47) * mm, "end": v(-32.16, 14.47) * mm});
            skLineSegment(sketch, "E100.top", {"start": v(-33.84, 18.7) * mm, "end": v(-29.5, 18.7) * mm});
            skLineSegment(sketch, "E100.left", {"start": v(-33.84, 14.47) * mm, "end": v(-33.84, 18.7) * mm});
            skLineSegment(sketch, "E100.right", {"start": v(-29.5, 16.74) * mm, "end": v(-29.5, 18.7) * mm});
            skArc(sketch, "E101", {"start": v(-29.5, 16.74) * mm, "mid": v(-31.35, 16.22) * mm, "end": v(-32.16, 14.47) * mm});
            skLineSegment(sketch, "E102.bottom", {"start": v(-33.6, -31.08) * mm, "end": v(-33.6, -31.08) * mm});
            skLineSegment(sketch, "E102.top", {"start": v(-33.6, -34.81) * mm, "end": v(-31.03, -34.81) * mm});
            skLineSegment(sketch, "E102.left", {"start": v(-33.6, -31.08) * mm, "end": v(-33.6, -34.81) * mm});
            skLineSegment(sketch, "E102.right", {"start": v(-31.03, -31.08) * mm, "end": v(-31.03, -33.21) * mm});
            skLineSegment(sketch, "E103.bottom", {"start": v(-31.03, -34.81) * mm, "end": v(-28.95, -34.81) * mm});
            skLineSegment(sketch, "E103.top", {"start": v(-31.03, -33.21) * mm, "end": v(-28.95, -33.21) * mm});
            skLineSegment(sketch, "E103.right", {"start": v(-28.95, -34.81) * mm, "end": v(-28.95, -33.21) * mm});
            skPoint(sketch, "E104.end.orphan", {"position": v(-34.98, -31.08) * mm});
            skPoint(sketch, "E104.start.orphan", {"position": v(-34.98, -30.78) * mm});
            skLineSegment(sketch, "E105.bottom", {"start": v(16.87, -34.88) * mm, "end": v(19.69, -34.88) * mm});
            skLineSegment(sketch, "E105.top", {"start": v(16.87, -30.79) * mm, "end": v(19.69, -30.79) * mm});
            skLineSegment(sketch, "E105.left", {"start": v(16.87, -33.4) * mm, "end": v(16.87, -30.79) * mm});
            skLineSegment(sketch, "E105.right", {"start": v(19.69, -34.88) * mm, "end": v(19.69, -30.79) * mm});
            skLineSegment(sketch, "E106.bottom", {"start": v(16.87, -34.88) * mm, "end": v(14.73, -34.88) * mm});
            skLineSegment(sketch, "E106.top", {"start": v(16.87, -33.4) * mm, "end": v(14.73, -33.4) * mm});
            skLineSegment(sketch, "E106.right", {"start": v(14.73, -34.88) * mm, "end": v(14.73, -33.4) * mm});
            skLineSegment(sketch, "E107.top", {"start": v(-31.03, -30.09) * mm, "end": v(-33.6, -30.09) * mm});
            skLineSegment(sketch, "E107.left", {"start": v(-31.03, -31.08) * mm, "end": v(-31.03, -30.09) * mm});
            skLineSegment(sketch, "E107.right", {"start": v(-33.6, -31.08) * mm, "end": v(-33.6, -30.09) * mm});
            skLineSegment(sketch, "E108", {"start": v(5.87, -31.08) * mm, "end": v(5.87, -30.78) * mm});
            skPoint(sketch, "E109.end.orphan", {"position": v(-34.98, -17.16) * mm});
            skPoint(sketch, "E109.start.orphan", {"position": v(-34.98, -16.86) * mm});
            skLineSegment(sketch, "E110.trimOffspring", {"start": v(5.97, -17.16) * mm, "end": v(5.97, -16.86) * mm});
            skLineSegment(sketch, "E111.bottom", {"start": v(5.85, -23.4) * mm, "end": v(18.49, -23.4) * mm});
            skLineSegment(sketch, "E111.top", {"start": v(5.85, -23.7) * mm, "end": v(18.49, -23.7) * mm});
            skLineSegment(sketch, "E111.left", {"start": v(5.85, -23.4) * mm, "end": v(5.85, -23.7) * mm});
            skLineSegment(sketch, "E112", {"start": v(5.29, -31.08) * mm, "end": v(5.29, 2.03) * mm});
            skLineSegment(sketch, "E113", {"start": v(4.99, -31.08) * mm, "end": v(5.29, -31.08) * mm});
            skLineSegment(sketch, "E114", {"start": v(12.44, -30.78) * mm, "end": v(12.44, -31.08) * mm});
            skLineSegment(sketch, "E115", {"start": v(18.49, -16.86) * mm, "end": v(18.49, -17.16) * mm});
            skPoint(sketch, "E116.orphan", {"position": v(19.24, -17.16) * mm});
            skLineSegment(sketch, "E117.trimOffspring", {"start": v(18.49, -23.4) * mm, "end": v(18.49, -23.7) * mm});
            skPoint(sketch, "E118.orphan", {"position": v(19.24, -23.7) * mm});
            skLineSegment(sketch, "E119.trimOffspring", {"start": v(4.99, 2.03) * mm, "end": v(4.99, -31.08) * mm});
            skLineSegment(sketch, "E120", {"start": v(4.99, 2.03) * mm, "end": v(5.29, 2.03) * mm});
            skLineSegment(sketch, "E121.bottom", {"start": v(4.99, 2.73) * mm, "end": v(13.12, 2.73) * mm});
            skLineSegment(sketch, "E121.top", {"start": v(4.99, 6.24) * mm, "end": v(13.12, 6.24) * mm});
            skLineSegment(sketch, "E121.left", {"start": v(4.99, 2.73) * mm, "end": v(4.99, 6.24) * mm});
            skLineSegment(sketch, "E121.right", {"start": v(13.12, 2.73) * mm, "end": v(13.12, 6.24) * mm});
            skCircle(sketch, "E122", {"center": v(8.91, 3.9) * mm, "radius": 1.04 * mm});
            skPoint(sketch, "E122.first.point", {"position": v(8.9, 2.86) * mm});
            skPoint(sketch, "E122.second.point", {"position": v(8.95, 4.94) * mm});
            skPoint(sketch, "E122.third.point", {"position": v(9.95, 3.84) * mm});
            skSolve(sketch);
        }
        {
            var Q0;
            Q0=qSketchRegion(id+"F25",true);
            var Q1;
            Q1=makeQuery(id+"F6.opShell","OFFSET_FACE",FACE,{"disambiguationData":[OSD([sQuery(id+"F2.wireOp",EDGE,"E20"),sQuery(id+"F2.wireOp",EDGE,"E22")])]});
            extrude(context, id + "F26", {"entities" : qUnion([Q0]), "operationType" : NewBodyOperationType.ADD, "endBoundEntityFace" : qUnion([Q1]), "depth" : 7.5 * mm});
        }
        {
            var Q0;
            Q0=qCreatedBy(makeId("Top.planeOp"),FACE);
            var sketch = newSketch(context, id + "F27", { "sketchPlane" : qUnion([Q0])});
            skLineSegment(sketch, "E123", {"start": v(-14.06, 0.58) * mm, "end": v(-9.7, 0.57) * mm});
            skLineSegment(sketch, "E124", {"start": v(-8.04, -3.57) * mm, "end": v(-8.03, -3.84) * mm});
            skLineSegment(sketch, "E125", {"start": v(-8.03, -3.84) * mm, "end": v(-8.04, -13.15) * mm});
            skLineSegment(sketch, "E126", {"start": v(-8.04, -13.15) * mm, "end": v(-8.03, -13.22) * mm});
            skLineSegment(sketch, "E127", {"start": v(-8.03, -13.22) * mm, "end": v(-8.03, -13.28) * mm});
            skLineSegment(sketch, "E128", {"start": v(-8.03, -13.28) * mm, "end": v(-8.04, -13.35) * mm});
            skLineSegment(sketch, "E129", {"start": v(-8.04, -13.35) * mm, "end": v(-8.04, -13.42) * mm});
            skLineSegment(sketch, "E130", {"start": v(-8.04, -13.42) * mm, "end": v(-8.05, -13.48) * mm});
            skLineSegment(sketch, "E131", {"start": v(-8.05, -13.48) * mm, "end": v(-8.06, -13.55) * mm});
            skLineSegment(sketch, "E132", {"start": v(-8.06, -13.55) * mm, "end": v(-8.07, -13.61) * mm});
            skLineSegment(sketch, "E133", {"start": v(-8.07, -13.61) * mm, "end": v(-8.1, -13.68) * mm});
            skLineSegment(sketch, "E134", {"start": v(-8.1, -13.68) * mm, "end": v(-8.1, -13.74) * mm});
            skLineSegment(sketch, "E135", {"start": v(-8.1, -13.74) * mm, "end": v(-8.13, -13.8) * mm});
            skLineSegment(sketch, "E136", {"start": v(-8.13, -13.8) * mm, "end": v(-8.15, -13.86) * mm});
            skLineSegment(sketch, "E137", {"start": v(-8.15, -13.86) * mm, "end": v(-8.18, -13.93) * mm});
            skLineSegment(sketch, "E138", {"start": v(-8.18, -13.93) * mm, "end": v(-8.2, -13.99) * mm});
            skLineSegment(sketch, "E139", {"start": v(-8.2, -13.99) * mm, "end": v(-8.23, -14.05) * mm});
            skLineSegment(sketch, "E140", {"start": v(-8.23, -14.05) * mm, "end": v(-8.26, -14.1) * mm});
            skLineSegment(sketch, "E141", {"start": v(-8.26, -14.1) * mm, "end": v(-8.3, -14.16) * mm});
            skLineSegment(sketch, "E142", {"start": v(-8.3, -14.16) * mm, "end": v(-8.33, -14.22) * mm});
            skLineSegment(sketch, "E143", {"start": v(-8.33, -14.22) * mm, "end": v(-8.37, -14.27) * mm});
            skLineSegment(sketch, "E144", {"start": v(-8.37, -14.27) * mm, "end": v(-8.4, -14.32) * mm});
            skLineSegment(sketch, "E145", {"start": v(-8.4, -14.32) * mm, "end": v(-8.45, -14.37) * mm});
            skLineSegment(sketch, "E146", {"start": v(-8.45, -14.37) * mm, "end": v(-8.5, -14.42) * mm});
            skLineSegment(sketch, "E147", {"start": v(-8.5, -14.42) * mm, "end": v(-8.54, -14.47) * mm});
            skLineSegment(sketch, "E148", {"start": v(-8.54, -14.47) * mm, "end": v(-8.59, -14.52) * mm});
            skLineSegment(sketch, "E149", {"start": v(-8.59, -14.52) * mm, "end": v(-8.63, -14.56) * mm});
            skLineSegment(sketch, "E150", {"start": v(-8.63, -14.56) * mm, "end": v(-8.69, -14.6) * mm});
            skLineSegment(sketch, "E151", {"start": v(-8.69, -14.6) * mm, "end": v(-8.74, -14.64) * mm});
            skLineSegment(sketch, "E152", {"start": v(-8.74, -14.64) * mm, "end": v(-8.8, -14.68) * mm});
            skLineSegment(sketch, "E153", {"start": v(-8.8, -14.68) * mm, "end": v(-8.85, -14.72) * mm});
            skLineSegment(sketch, "E154", {"start": v(-8.85, -14.72) * mm, "end": v(-8.9, -14.75) * mm});
            skLineSegment(sketch, "E155", {"start": v(-8.9, -14.75) * mm, "end": v(-8.95, -14.77) * mm});
            skLineSegment(sketch, "E156", {"start": v(-8.95, -14.77) * mm, "end": v(-8.99, -14.8) * mm});
            skLineSegment(sketch, "E157", {"start": v(-8.99, -14.8) * mm, "end": v(-9.03, -14.81) * mm});
            skLineSegment(sketch, "E158", {"start": v(-9.03, -14.81) * mm, "end": v(-9.07, -14.83) * mm});
            skLineSegment(sketch, "E159", {"start": v(-9.07, -14.83) * mm, "end": v(-9.11, -14.85) * mm});
            skLineSegment(sketch, "E160", {"start": v(-9.11, -14.85) * mm, "end": v(-9.16, -14.86) * mm});
            skLineSegment(sketch, "E161", {"start": v(-9.16, -14.86) * mm, "end": v(-9.2, -14.88) * mm});
            skLineSegment(sketch, "E162", {"start": v(-9.2, -14.88) * mm, "end": v(-9.24, -14.9) * mm});
            skLineSegment(sketch, "E163", {"start": v(-9.24, -14.9) * mm, "end": v(-9.29, -14.9) * mm});
            skLineSegment(sketch, "E164", {"start": v(-9.29, -14.9) * mm, "end": v(-9.33, -14.91) * mm});
            skLineSegment(sketch, "E165", {"start": v(-9.33, -14.91) * mm, "end": v(-9.38, -14.92) * mm});
            skLineSegment(sketch, "E166", {"start": v(-9.38, -14.92) * mm, "end": v(-9.42, -14.93) * mm});
            skLineSegment(sketch, "E167", {"start": v(-9.42, -14.93) * mm, "end": v(-9.51, -14.94) * mm});
            skLineSegment(sketch, "E168", {"start": v(-9.51, -14.94) * mm, "end": v(-9.6, -14.96) * mm});
            skLineSegment(sketch, "E169", {"start": v(-9.6, -14.96) * mm, "end": v(-9.74, -14.97) * mm});
            skLineSegment(sketch, "E170", {"start": v(-9.74, -14.97) * mm, "end": v(-10.2, -14.98) * mm});
            skLineSegment(sketch, "E171", {"start": v(-10.2, -14.98) * mm, "end": v(-23.2, -14.97) * mm});
            skLineSegment(sketch, "E172", {"start": v(-23.2, -14.97) * mm, "end": v(-23.28, -14.97) * mm});
            skLineSegment(sketch, "E173", {"start": v(-23.28, -14.97) * mm, "end": v(-23.35, -14.97) * mm});
            skLineSegment(sketch, "E174", {"start": v(-23.35, -14.97) * mm, "end": v(-23.43, -14.97) * mm});
            skLineSegment(sketch, "E175", {"start": v(-23.43, -14.97) * mm, "end": v(-23.5, -14.96) * mm});
            skLineSegment(sketch, "E176", {"start": v(-23.5, -14.96) * mm, "end": v(-23.58, -14.94) * mm});
            skLineSegment(sketch, "E177", {"start": v(-23.58, -14.94) * mm, "end": v(-23.65, -14.93) * mm});
            skLineSegment(sketch, "E178", {"start": v(-23.65, -14.93) * mm, "end": v(-23.72, -14.9) * mm});
            skLineSegment(sketch, "E179", {"start": v(-23.72, -14.9) * mm, "end": v(-23.8, -14.89) * mm});
            skLineSegment(sketch, "E180", {"start": v(-23.8, -14.89) * mm, "end": v(-23.86, -14.86) * mm});
            skLineSegment(sketch, "E181", {"start": v(-23.86, -14.86) * mm, "end": v(-23.93, -14.83) * mm});
            skLineSegment(sketch, "E182", {"start": v(-23.93, -14.83) * mm, "end": v(-24, -14.8) * mm});
            skLineSegment(sketch, "E183", {"start": v(-24, -14.8) * mm, "end": v(-24.07, -14.77) * mm});
            skLineSegment(sketch, "E184", {"start": v(-24.07, -14.77) * mm, "end": v(-24.13, -14.73) * mm});
            skLineSegment(sketch, "E185", {"start": v(-24.13, -14.73) * mm, "end": v(-24.2, -14.7) * mm});
            skLineSegment(sketch, "E186", {"start": v(-24.2, -14.7) * mm, "end": v(-24.26, -14.65) * mm});
            skLineSegment(sketch, "E187", {"start": v(-24.26, -14.65) * mm, "end": v(-24.32, -14.6) * mm});
            skLineSegment(sketch, "E188", {"start": v(-24.32, -14.6) * mm, "end": v(-24.38, -14.56) * mm});
            skLineSegment(sketch, "E189", {"start": v(-24.38, -14.56) * mm, "end": v(-24.43, -14.51) * mm});
            skLineSegment(sketch, "E190", {"start": v(-24.43, -14.51) * mm, "end": v(-24.48, -14.46) * mm});
            skLineSegment(sketch, "E191", {"start": v(-24.48, -14.46) * mm, "end": v(-24.54, -14.4) * mm});
            skLineSegment(sketch, "E192", {"start": v(-24.54, -14.4) * mm, "end": v(-24.59, -14.35) * mm});
            skLineSegment(sketch, "E193", {"start": v(-24.59, -14.35) * mm, "end": v(-24.63, -14.3) * mm});
            skLineSegment(sketch, "E194", {"start": v(-24.63, -14.3) * mm, "end": v(-24.68, -14.23) * mm});
            skLineSegment(sketch, "E195", {"start": v(-24.68, -14.23) * mm, "end": v(-24.72, -14.17) * mm});
            skLineSegment(sketch, "E196", {"start": v(-24.72, -14.17) * mm, "end": v(-24.76, -14.1) * mm});
            skLineSegment(sketch, "E197", {"start": v(-24.76, -14.1) * mm, "end": v(-24.8, -14.04) * mm});
            skLineSegment(sketch, "E198", {"start": v(-24.8, -14.04) * mm, "end": v(-24.82, -13.97) * mm});
            skLineSegment(sketch, "E199", {"start": v(-24.82, -13.97) * mm, "end": v(-24.85, -13.9) * mm});
            skLineSegment(sketch, "E200", {"start": v(-24.85, -13.9) * mm, "end": v(-24.88, -13.83) * mm});
            skLineSegment(sketch, "E201", {"start": v(-24.88, -13.83) * mm, "end": v(-24.9, -13.76) * mm});
            skLineSegment(sketch, "E202", {"start": v(-24.9, -13.76) * mm, "end": v(-24.92, -13.66) * mm});
            skLineSegment(sketch, "E203", {"start": v(-24.92, -13.66) * mm, "end": v(-24.94, -13.55) * mm});
            skLineSegment(sketch, "E204", {"start": v(-24.94, -13.55) * mm, "end": v(-24.96, -13.38) * mm});
            skLineSegment(sketch, "E205", {"start": v(-24.96, -13.38) * mm, "end": v(-24.98, -12.8) * mm});
            skLineSegment(sketch, "E206", {"start": v(-24.98, -12.8) * mm, "end": v(-24.98, -3.92) * mm});
            skLineSegment(sketch, "E207", {"start": v(-24.98, -3.92) * mm, "end": v(-24.97, -3.38) * mm});
            skLineSegment(sketch, "E208", {"start": v(-24.97, -3.38) * mm, "end": v(-24.96, -3.24) * mm});
            skLineSegment(sketch, "E209", {"start": v(-24.96, -3.24) * mm, "end": v(-24.95, -3.15) * mm});
            skLineSegment(sketch, "E210", {"start": v(-24.95, -3.15) * mm, "end": v(-24.94, -3.1) * mm});
            skLineSegment(sketch, "E211", {"start": v(-24.94, -3.1) * mm, "end": v(-24.93, -3.06) * mm});
            skLineSegment(sketch, "E212", {"start": v(-24.93, -3.06) * mm, "end": v(-24.93, -3.02) * mm});
            skLineSegment(sketch, "E213", {"start": v(-24.93, -3.02) * mm, "end": v(-24.92, -2.97) * mm});
            skLineSegment(sketch, "E214", {"start": v(-24.92, -2.97) * mm, "end": v(-24.9, -2.93) * mm});
            skLineSegment(sketch, "E215", {"start": v(-24.9, -2.93) * mm, "end": v(-24.9, -2.88) * mm});
            skLineSegment(sketch, "E216", {"start": v(-24.9, -2.88) * mm, "end": v(-24.88, -2.84) * mm});
            skLineSegment(sketch, "E217", {"start": v(-24.88, -2.84) * mm, "end": v(-24.87, -2.8) * mm});
            skLineSegment(sketch, "E218", {"start": v(-24.87, -2.8) * mm, "end": v(-24.85, -2.76) * mm});
            skLineSegment(sketch, "E219", {"start": v(-24.85, -2.76) * mm, "end": v(-24.83, -2.71) * mm});
            skLineSegment(sketch, "E220", {"start": v(-24.83, -2.71) * mm, "end": v(-24.81, -2.67) * mm});
            skLineSegment(sketch, "E221", {"start": v(-24.81, -2.67) * mm, "end": v(-24.8, -2.63) * mm});
            skLineSegment(sketch, "E222", {"start": v(-24.8, -2.63) * mm, "end": v(-24.77, -2.58) * mm});
            skLineSegment(sketch, "E223", {"start": v(-24.77, -2.58) * mm, "end": v(-24.74, -2.53) * mm});
            skLineSegment(sketch, "E224", {"start": v(-24.74, -2.53) * mm, "end": v(-24.7, -2.48) * mm});
            skLineSegment(sketch, "E225", {"start": v(-24.7, -2.48) * mm, "end": v(-24.68, -2.43) * mm});
            skLineSegment(sketch, "E226", {"start": v(-24.68, -2.43) * mm, "end": v(-24.64, -2.38) * mm});
            skLineSegment(sketch, "E227", {"start": v(-24.64, -2.38) * mm, "end": v(-24.6, -2.34) * mm});
            skLineSegment(sketch, "E228", {"start": v(-24.6, -2.34) * mm, "end": v(-24.57, -2.3) * mm});
            skLineSegment(sketch, "E229", {"start": v(-24.57, -2.3) * mm, "end": v(-24.53, -2.25) * mm});
            skLineSegment(sketch, "E230", {"start": v(-24.53, -2.25) * mm, "end": v(-24.5, -2.2) * mm});
            skLineSegment(sketch, "E231", {"start": v(-24.5, -2.2) * mm, "end": v(-24.45, -2.16) * mm});
            skLineSegment(sketch, "E232", {"start": v(-24.45, -2.16) * mm, "end": v(-24.41, -2.12) * mm});
            skLineSegment(sketch, "E233", {"start": v(-24.41, -2.12) * mm, "end": v(-24.37, -2.08) * mm});
            skLineSegment(sketch, "E234", {"start": v(-24.37, -2.08) * mm, "end": v(-24.32, -2.05) * mm});
            skLineSegment(sketch, "E235", {"start": v(-24.32, -2.05) * mm, "end": v(-24.28, -2.01) * mm});
            skLineSegment(sketch, "E236", {"start": v(-24.28, -2.01) * mm, "end": v(-24.23, -1.98) * mm});
            skLineSegment(sketch, "E237", {"start": v(-24.23, -1.98) * mm, "end": v(-24.18, -1.94) * mm});
            skLineSegment(sketch, "E238", {"start": v(-24.18, -1.94) * mm, "end": v(-24.13, -1.91) * mm});
            skLineSegment(sketch, "E239", {"start": v(-24.13, -1.91) * mm, "end": v(-24.08, -1.88) * mm});
            skLineSegment(sketch, "E240", {"start": v(-24.08, -1.88) * mm, "end": v(-24.03, -1.86) * mm});
            skLineSegment(sketch, "E241", {"start": v(-24.03, -1.86) * mm, "end": v(-23.98, -1.83) * mm});
            skLineSegment(sketch, "E242", {"start": v(-23.98, -1.83) * mm, "end": v(-23.93, -1.8) * mm});
            skLineSegment(sketch, "E243", {"start": v(-23.93, -1.8) * mm, "end": v(-23.87, -1.79) * mm});
            skLineSegment(sketch, "E244", {"start": v(-23.87, -1.79) * mm, "end": v(-23.82, -1.77) * mm});
            skLineSegment(sketch, "E245", {"start": v(-23.82, -1.77) * mm, "end": v(-23.76, -1.75) * mm});
            skLineSegment(sketch, "E246", {"start": v(-23.76, -1.75) * mm, "end": v(-23.7, -1.73) * mm});
            skLineSegment(sketch, "E247", {"start": v(-23.7, -1.73) * mm, "end": v(-23.65, -1.72) * mm});
            skLineSegment(sketch, "E248", {"start": v(-23.65, -1.72) * mm, "end": v(-23.6, -1.71) * mm});
            skLineSegment(sketch, "E249", {"start": v(-23.6, -1.71) * mm, "end": v(-23.53, -1.7) * mm});
            skLineSegment(sketch, "E250", {"start": v(-23.53, -1.7) * mm, "end": v(-23.48, -1.7) * mm});
            skLineSegment(sketch, "E251", {"start": v(-23.48, -1.7) * mm, "end": v(-23.32, -1.69) * mm});
            skLineSegment(sketch, "E252", {"start": v(-23.32, -1.69) * mm, "end": v(-23.17, -1.68) * mm});
            skLineSegment(sketch, "E253", {"start": v(-23.17, -1.68) * mm, "end": v(-22.95, -1.67) * mm});
            skLineSegment(sketch, "E254", {"start": v(-22.95, -1.67) * mm, "end": v(-21.9, -1.67) * mm});
            skLineSegment(sketch, "E255", {"start": v(-21.9, -1.67) * mm, "end": v(-21.52, -1.67) * mm});
            skLineSegment(sketch, "E256", {"start": v(-21.52, -1.67) * mm, "end": v(-21.3, -1.66) * mm});
            skLineSegment(sketch, "E257", {"start": v(-21.3, -1.66) * mm, "end": v(-21.2, -1.64) * mm});
            skLineSegment(sketch, "E258", {"start": v(-21.2, -1.64) * mm, "end": v(-20.86, -1.5) * mm});
            skLineSegment(sketch, "E259", {"start": v(-20.86, -1.5) * mm, "end": v(-17.7, 0.02) * mm});
            skLineSegment(sketch, "E260", {"start": v(-17.7, 0.02) * mm, "end": v(-17.01, 0.36) * mm});
            skLineSegment(sketch, "E261", {"start": v(-15.75, 0.24) * mm, "end": v(-14.06, -0.59) * mm});
            skLineSegment(sketch, "E262", {"start": v(-14.06, -0.59) * mm, "end": v(-14.06, 0.58) * mm});
            skLineSegment(sketch, "E263", {"start": v(-13.15, -0.33) * mm, "end": v(-13.15, -2.1) * mm});
            skLineSegment(sketch, "E264", {"start": v(-13.15, -2.1) * mm, "end": v(-13.26, -2.06) * mm});
            skLineSegment(sketch, "E265", {"start": v(-13.26, -2.06) * mm, "end": v(-13.9, -1.75) * mm});
            skLineSegment(sketch, "E266", {"start": v(-16.83, -0.6) * mm, "end": v(-17.05, -0.71) * mm});
            skLineSegment(sketch, "E267", {"start": v(-17.05, -0.71) * mm, "end": v(-17.27, -0.83) * mm});
            skLineSegment(sketch, "E268", {"start": v(-17.27, -0.83) * mm, "end": v(-18.4, -1.4) * mm});
            skLineSegment(sketch, "E269", {"start": v(-18.4, -1.4) * mm, "end": v(-22.7, -3.51) * mm});
            skLineSegment(sketch, "E270", {"start": v(-22.7, -3.51) * mm, "end": v(-23.6, -3.97) * mm});
            skLineSegment(sketch, "E271", {"start": v(-23.6, -3.97) * mm, "end": v(-23.64, -4) * mm});
            skLineSegment(sketch, "E272", {"start": v(-23.64, -4) * mm, "end": v(-23.69, -4.02) * mm});
            skLineSegment(sketch, "E273", {"start": v(-23.69, -4.02) * mm, "end": v(-23.73, -4.05) * mm});
            skLineSegment(sketch, "E274", {"start": v(-23.73, -4.05) * mm, "end": v(-23.76, -4.08) * mm});
            skLineSegment(sketch, "E275", {"start": v(-23.76, -4.08) * mm, "end": v(-23.79, -4.1) * mm});
            skLineSegment(sketch, "E276", {"start": v(-23.79, -4.1) * mm, "end": v(-23.8, -4.13) * mm});
            skLineSegment(sketch, "E277", {"start": v(-23.8, -4.13) * mm, "end": v(-23.82, -4.15) * mm});
            skLineSegment(sketch, "E278", {"start": v(-23.82, -4.15) * mm, "end": v(-23.83, -4.16) * mm});
            skLineSegment(sketch, "E279", {"start": v(-23.83, -4.16) * mm, "end": v(-23.83, -4.18) * mm});
            skLineSegment(sketch, "E280", {"start": v(-23.83, -4.18) * mm, "end": v(-23.84, -4.2) * mm});
            skLineSegment(sketch, "E281", {"start": v(-23.84, -4.2) * mm, "end": v(-23.85, -4.21) * mm});
            skLineSegment(sketch, "E282", {"start": v(-23.85, -4.21) * mm, "end": v(-23.85, -4.23) * mm});
            skLineSegment(sketch, "E283", {"start": v(-23.85, -4.23) * mm, "end": v(-23.85, -4.25) * mm});
            skLineSegment(sketch, "E284", {"start": v(-23.85, -4.25) * mm, "end": v(-23.86, -4.27) * mm});
            skLineSegment(sketch, "E285", {"start": v(-23.86, -4.27) * mm, "end": v(-23.86, -4.29) * mm});
            skLineSegment(sketch, "E286", {"start": v(-23.86, -4.29) * mm, "end": v(-23.86, -4.3) * mm});
            skLineSegment(sketch, "E287", {"start": v(-23.86, -4.3) * mm, "end": v(-23.85, -4.32) * mm});
            skLineSegment(sketch, "E288", {"start": v(-23.85, -4.32) * mm, "end": v(-23.85, -4.34) * mm});
            skLineSegment(sketch, "E289", {"start": v(-23.85, -4.34) * mm, "end": v(-23.84, -4.36) * mm});
            skLineSegment(sketch, "E290", {"start": v(-23.84, -4.36) * mm, "end": v(-23.84, -4.38) * mm});
            skLineSegment(sketch, "E291", {"start": v(-23.84, -4.38) * mm, "end": v(-23.83, -4.4) * mm});
            skLineSegment(sketch, "E292", {"start": v(-23.83, -4.4) * mm, "end": v(-23.82, -4.42) * mm});
            skLineSegment(sketch, "E293", {"start": v(-23.82, -4.42) * mm, "end": v(-23.81, -4.44) * mm});
            skLineSegment(sketch, "E294", {"start": v(-23.81, -4.44) * mm, "end": v(-23.8, -4.45) * mm});
            skLineSegment(sketch, "E295", {"start": v(-23.8, -4.45) * mm, "end": v(-23.8, -4.47) * mm});
            skLineSegment(sketch, "E296", {"start": v(-23.8, -4.47) * mm, "end": v(-23.78, -4.48) * mm});
            skLineSegment(sketch, "E297", {"start": v(-23.78, -4.48) * mm, "end": v(-23.76, -4.5) * mm});
            skLineSegment(sketch, "E298", {"start": v(-23.76, -4.5) * mm, "end": v(-23.73, -4.53) * mm});
            skLineSegment(sketch, "E299", {"start": v(-23.73, -4.53) * mm, "end": v(-23.7, -4.55) * mm});
            skLineSegment(sketch, "E300", {"start": v(-23.7, -4.55) * mm, "end": v(-23.58, -4.62) * mm});
            skLineSegment(sketch, "E301", {"start": v(-23.58, -4.62) * mm, "end": v(-23.42, -4.7) * mm});
            skLineSegment(sketch, "E302", {"start": v(-23.42, -4.7) * mm, "end": v(-19.6, -6.6) * mm});
            skLineSegment(sketch, "E303", {"start": v(-19.6, -6.6) * mm, "end": v(-18.6, -7.09) * mm});
            skLineSegment(sketch, "E304", {"start": v(-18.6, -7.09) * mm, "end": v(-17.5, -7.65) * mm});
            skLineSegment(sketch, "E305", {"start": v(-17.5, -7.65) * mm, "end": v(-16.7, -8.03) * mm});
            skLineSegment(sketch, "E306", {"start": v(-16.7, -8.03) * mm, "end": v(-16.68, -8.04) * mm});
            skLineSegment(sketch, "E307", {"start": v(-16.68, -8.04) * mm, "end": v(-16.66, -8.05) * mm});
            skLineSegment(sketch, "E308", {"start": v(-16.66, -8.05) * mm, "end": v(-16.64, -8.06) * mm});
            skLineSegment(sketch, "E309", {"start": v(-16.64, -8.06) * mm, "end": v(-16.62, -8.06) * mm});
            skLineSegment(sketch, "E310", {"start": v(-16.62, -8.06) * mm, "end": v(-16.6, -8.07) * mm});
            skLineSegment(sketch, "E311", {"start": v(-16.6, -8.07) * mm, "end": v(-16.58, -8.07) * mm});
            skLineSegment(sketch, "E312", {"start": v(-16.58, -8.07) * mm, "end": v(-16.56, -8.07) * mm});
            skLineSegment(sketch, "E313", {"start": v(-16.56, -8.07) * mm, "end": v(-16.54, -8.07) * mm});
            skLineSegment(sketch, "E314", {"start": v(-16.54, -8.07) * mm, "end": v(-16.52, -8.08) * mm});
            skLineSegment(sketch, "E315", {"start": v(-16.52, -8.08) * mm, "end": v(-16.48, -8.07) * mm});
            skLineSegment(sketch, "E316", {"start": v(-16.48, -8.07) * mm, "end": v(-16.44, -8.07) * mm});
            skLineSegment(sketch, "E317", {"start": v(-16.44, -8.07) * mm, "end": v(-16.4, -8.06) * mm});
            skLineSegment(sketch, "E318", {"start": v(-16.4, -8.06) * mm, "end": v(-16.32, -8.04) * mm});
            skLineSegment(sketch, "E319", {"start": v(-16.32, -8.04) * mm, "end": v(-16.14, -7.96) * mm});
            skLineSegment(sketch, "E320", {"start": v(-16.14, -7.96) * mm, "end": v(-13.76, -6.78) * mm});
            skLineSegment(sketch, "E321", {"start": v(-13.76, -6.78) * mm, "end": v(-9.85, -4.84) * mm});
            skLineSegment(sketch, "E322", {"start": v(-9.4, -3.99) * mm, "end": v(-9.57, -3.89) * mm});
            skLineSegment(sketch, "E323", {"start": v(-9.57, -3.89) * mm, "end": v(-10.59, -3.4) * mm});
            skLineSegment(sketch, "E324", {"start": v(-10.59, -3.4) * mm, "end": v(-10.6, -0.33) * mm});
            skLineSegment(sketch, "E325", {"start": v(-10.6, -0.33) * mm, "end": v(-13.15, -0.33) * mm});
            skLineSegment(sketch, "E326", {"start": v(-26.34, -4.98) * mm, "end": v(-25.3, -4.97) * mm});
            skLineSegment(sketch, "E327", {"start": v(-25.3, -4.97) * mm, "end": v(-25.28, -6.53) * mm});
            skLineSegment(sketch, "E328", {"start": v(-25.28, -6.53) * mm, "end": v(-26.11, -6.52) * mm});
            skLineSegment(sketch, "E329", {"start": v(-26.11, -6.52) * mm, "end": v(-26.27, -6.5) * mm});
            skLineSegment(sketch, "E330", {"start": v(-26.27, -6.5) * mm, "end": v(-26.38, -6.49) * mm});
            skLineSegment(sketch, "E331", {"start": v(-26.38, -6.49) * mm, "end": v(-26.4, -6.47) * mm});
            skLineSegment(sketch, "E332", {"start": v(-26.4, -6.47) * mm, "end": v(-26.43, -6.45) * mm});
            skLineSegment(sketch, "E333", {"start": v(-26.43, -6.45) * mm, "end": v(-26.45, -6.43) * mm});
            skLineSegment(sketch, "E334", {"start": v(-26.45, -6.43) * mm, "end": v(-26.47, -6.41) * mm});
            skLineSegment(sketch, "E335", {"start": v(-26.47, -6.41) * mm, "end": v(-26.49, -6.39) * mm});
            skLineSegment(sketch, "E336", {"start": v(-26.49, -6.39) * mm, "end": v(-26.5, -6.37) * mm});
            skLineSegment(sketch, "E337", {"start": v(-26.5, -6.37) * mm, "end": v(-26.52, -6.34) * mm});
            skLineSegment(sketch, "E338", {"start": v(-26.52, -6.34) * mm, "end": v(-26.54, -6.32) * mm});
            skLineSegment(sketch, "E339", {"start": v(-26.54, -6.32) * mm, "end": v(-26.55, -6.29) * mm});
            skLineSegment(sketch, "E340", {"start": v(-26.55, -6.29) * mm, "end": v(-26.56, -6.26) * mm});
            skLineSegment(sketch, "E341", {"start": v(-26.56, -6.26) * mm, "end": v(-26.57, -6.23) * mm});
            skLineSegment(sketch, "E342", {"start": v(-26.57, -6.23) * mm, "end": v(-26.58, -6.2) * mm});
            skLineSegment(sketch, "E343", {"start": v(-26.58, -6.2) * mm, "end": v(-26.59, -6.18) * mm});
            skLineSegment(sketch, "E344", {"start": v(-26.59, -6.18) * mm, "end": v(-26.6, -6.15) * mm});
            skLineSegment(sketch, "E345", {"start": v(-26.6, -6.15) * mm, "end": v(-26.6, -6.09) * mm});
            skLineSegment(sketch, "E346", {"start": v(-26.6, -6.09) * mm, "end": v(-26.62, -6.03) * mm});
            skLineSegment(sketch, "E347", {"start": v(-26.62, -6.03) * mm, "end": v(-26.62, -5.9) * mm});
            skLineSegment(sketch, "E348", {"start": v(-26.62, -5.9) * mm, "end": v(-26.63, -5.75) * mm});
            skLineSegment(sketch, "E349", {"start": v(-26.63, -5.75) * mm, "end": v(-26.63, -5.7) * mm});
            skLineSegment(sketch, "E350", {"start": v(-26.63, -5.7) * mm, "end": v(-26.63, -5.62) * mm});
            skLineSegment(sketch, "E351", {"start": v(-26.63, -5.62) * mm, "end": v(-26.62, -5.5) * mm});
            skLineSegment(sketch, "E352", {"start": v(-26.62, -5.5) * mm, "end": v(-26.6, -5.42) * mm});
            skLineSegment(sketch, "E353", {"start": v(-26.6, -5.42) * mm, "end": v(-26.6, -5.36) * mm});
            skLineSegment(sketch, "E354", {"start": v(-26.6, -5.36) * mm, "end": v(-26.58, -5.3) * mm});
            skLineSegment(sketch, "E355", {"start": v(-26.58, -5.3) * mm, "end": v(-26.58, -5.28) * mm});
            skLineSegment(sketch, "E356", {"start": v(-26.58, -5.28) * mm, "end": v(-26.57, -5.25) * mm});
            skLineSegment(sketch, "E357", {"start": v(-26.57, -5.25) * mm, "end": v(-26.56, -5.23) * mm});
            skLineSegment(sketch, "E358", {"start": v(-26.56, -5.23) * mm, "end": v(-26.55, -5.2) * mm});
            skLineSegment(sketch, "E359", {"start": v(-26.55, -5.2) * mm, "end": v(-26.53, -5.18) * mm});
            skLineSegment(sketch, "E360", {"start": v(-26.53, -5.18) * mm, "end": v(-26.52, -5.15) * mm});
            skLineSegment(sketch, "E361", {"start": v(-26.52, -5.15) * mm, "end": v(-26.5, -5.13) * mm});
            skLineSegment(sketch, "E362", {"start": v(-26.5, -5.13) * mm, "end": v(-26.5, -5.1) * mm});
            skLineSegment(sketch, "E363", {"start": v(-26.5, -5.1) * mm, "end": v(-26.47, -5.09) * mm});
            skLineSegment(sketch, "E364", {"start": v(-26.47, -5.09) * mm, "end": v(-26.46, -5.07) * mm});
            skLineSegment(sketch, "E365", {"start": v(-26.46, -5.07) * mm, "end": v(-26.44, -5.05) * mm});
            skLineSegment(sketch, "E366", {"start": v(-26.44, -5.05) * mm, "end": v(-26.42, -5.03) * mm});
            skLineSegment(sketch, "E367", {"start": v(-26.42, -5.03) * mm, "end": v(-26.4, -5.01) * mm});
            skLineSegment(sketch, "E368", {"start": v(-26.4, -5.01) * mm, "end": v(-26.37, -5) * mm});
            skLineSegment(sketch, "E369", {"start": v(-26.37, -5) * mm, "end": v(-26.34, -4.98) * mm});
            skLineSegment(sketch, "E370", {"start": v(-7.72, -4.97) * mm, "end": v(-7.68, -4.98) * mm});
            skLineSegment(sketch, "E371", {"start": v(-7.68, -4.98) * mm, "end": v(-7.64, -4.98) * mm});
            skLineSegment(sketch, "E372", {"start": v(-7.64, -4.98) * mm, "end": v(-7.6, -4.98) * mm});
            skLineSegment(sketch, "E373", {"start": v(-7.6, -4.98) * mm, "end": v(-7.55, -4.98) * mm});
            skLineSegment(sketch, "E374", {"start": v(-7.55, -4.98) * mm, "end": v(-7.5, -4.98) * mm});
            skLineSegment(sketch, "E375", {"start": v(-7.5, -4.98) * mm, "end": v(-7.41, -4.97) * mm});
            skLineSegment(sketch, "E376", {"start": v(-7.41, -4.97) * mm, "end": v(-7.13, -4.95) * mm});
            skLineSegment(sketch, "E377", {"start": v(-7.13, -4.95) * mm, "end": v(-7.09, -4.94) * mm});
            skLineSegment(sketch, "E378", {"start": v(-7.09, -4.94) * mm, "end": v(-7.04, -4.94) * mm});
            skLineSegment(sketch, "E379", {"start": v(-7.04, -4.94) * mm, "end": v(-7, -4.94) * mm});
            skLineSegment(sketch, "E380", {"start": v(-7, -4.94) * mm, "end": v(-6.95, -4.94) * mm});
            skLineSegment(sketch, "E381", {"start": v(-6.95, -4.94) * mm, "end": v(-6.9, -4.94) * mm});
            skLineSegment(sketch, "E382", {"start": v(-6.9, -4.94) * mm, "end": v(-6.86, -4.95) * mm});
            skLineSegment(sketch, "E383", {"start": v(-6.86, -4.95) * mm, "end": v(-6.82, -4.95) * mm});
            skLineSegment(sketch, "E384", {"start": v(-6.82, -4.95) * mm, "end": v(-6.78, -4.96) * mm});
            skLineSegment(sketch, "E385", {"start": v(-6.78, -4.96) * mm, "end": v(-6.74, -4.97) * mm});
            skLineSegment(sketch, "E386", {"start": v(-6.74, -4.97) * mm, "end": v(-6.7, -4.99) * mm});
            skLineSegment(sketch, "E387", {"start": v(-6.7, -4.99) * mm, "end": v(-6.66, -5) * mm});
            skLineSegment(sketch, "E388", {"start": v(-6.66, -5) * mm, "end": v(-6.62, -5.03) * mm});
            skLineSegment(sketch, "E389", {"start": v(-6.62, -5.03) * mm, "end": v(-6.58, -5.05) * mm});
            skLineSegment(sketch, "E390", {"start": v(-6.58, -5.05) * mm, "end": v(-6.55, -5.08) * mm});
            skLineSegment(sketch, "E391", {"start": v(-6.55, -5.08) * mm, "end": v(-6.52, -5.1) * mm});
            skLineSegment(sketch, "E392", {"start": v(-6.52, -5.1) * mm, "end": v(-6.48, -5.14) * mm});
            skLineSegment(sketch, "E393", {"start": v(-6.48, -5.14) * mm, "end": v(-6.47, -5.18) * mm});
            skLineSegment(sketch, "E394", {"start": v(-6.47, -5.18) * mm, "end": v(-6.46, -5.21) * mm});
            skLineSegment(sketch, "E395", {"start": v(-6.46, -5.21) * mm, "end": v(-6.45, -5.24) * mm});
            skLineSegment(sketch, "E396", {"start": v(-6.45, -5.24) * mm, "end": v(-6.43, -5.31) * mm});
            skLineSegment(sketch, "E397", {"start": v(-6.43, -5.31) * mm, "end": v(-6.41, -5.38) * mm});
            skLineSegment(sketch, "E398", {"start": v(-6.41, -5.38) * mm, "end": v(-6.4, -5.45) * mm});
            skLineSegment(sketch, "E399", {"start": v(-6.4, -5.45) * mm, "end": v(-6.4, -5.52) * mm});
            skLineSegment(sketch, "E400", {"start": v(-6.4, -5.52) * mm, "end": v(-6.39, -5.59) * mm});
            skLineSegment(sketch, "E401", {"start": v(-6.39, -5.59) * mm, "end": v(-6.38, -5.7) * mm});
            skLineSegment(sketch, "E402", {"start": v(-6.38, -5.7) * mm, "end": v(-6.39, -5.83) * mm});
            skLineSegment(sketch, "E403", {"start": v(-6.39, -5.83) * mm, "end": v(-6.4, -6.08) * mm});
            skLineSegment(sketch, "E404", {"start": v(-6.4, -6.08) * mm, "end": v(-6.42, -6.15) * mm});
            skLineSegment(sketch, "E405", {"start": v(-6.42, -6.15) * mm, "end": v(-6.47, -6.3) * mm});
            skLineSegment(sketch, "E406", {"start": v(-6.47, -6.3) * mm, "end": v(-6.5, -6.36) * mm});
            skLineSegment(sketch, "E407", {"start": v(-6.5, -6.36) * mm, "end": v(-6.53, -6.4) * mm});
            skLineSegment(sketch, "E408", {"start": v(-6.53, -6.4) * mm, "end": v(-6.56, -6.43) * mm});
            skLineSegment(sketch, "E409", {"start": v(-6.56, -6.43) * mm, "end": v(-6.59, -6.46) * mm});
            skLineSegment(sketch, "E410", {"start": v(-6.59, -6.46) * mm, "end": v(-6.61, -6.47) * mm});
            skLineSegment(sketch, "E411", {"start": v(-6.61, -6.47) * mm, "end": v(-6.64, -6.49) * mm});
            skLineSegment(sketch, "E412", {"start": v(-6.64, -6.49) * mm, "end": v(-6.67, -6.5) * mm});
            skLineSegment(sketch, "E413", {"start": v(-6.67, -6.5) * mm, "end": v(-7.74, -6.53) * mm});
            skLineSegment(sketch, "E414", {"start": v(-7.74, -6.53) * mm, "end": v(-7.72, -4.97) * mm});
            skLineSegment(sketch, "E415", {"start": v(-26.35, -7.32) * mm, "end": v(-25.28, -7.3) * mm});
            skLineSegment(sketch, "E416", {"start": v(-25.28, -7.3) * mm, "end": v(-25.28, -8.87) * mm});
            skLineSegment(sketch, "E417", {"start": v(-25.28, -8.87) * mm, "end": v(-26.35, -8.85) * mm});
            skLineSegment(sketch, "E418", {"start": v(-26.35, -8.85) * mm, "end": v(-26.5, -8.7) * mm});
            skLineSegment(sketch, "E419", {"start": v(-26.5, -8.7) * mm, "end": v(-26.55, -8.62) * mm});
            skLineSegment(sketch, "E420", {"start": v(-26.55, -8.62) * mm, "end": v(-26.57, -8.57) * mm});
            skLineSegment(sketch, "E421", {"start": v(-26.57, -8.57) * mm, "end": v(-26.6, -8.52) * mm});
            skLineSegment(sketch, "E422", {"start": v(-26.6, -8.52) * mm, "end": v(-26.6, -8.47) * mm});
            skLineSegment(sketch, "E423", {"start": v(-26.6, -8.47) * mm, "end": v(-26.6, -8.45) * mm});
            skLineSegment(sketch, "E424", {"start": v(-26.6, -8.45) * mm, "end": v(-26.61, -8.37) * mm});
            skLineSegment(sketch, "E425", {"start": v(-26.61, -8.37) * mm, "end": v(-26.63, -8.2) * mm});
            skLineSegment(sketch, "E426", {"start": v(-26.63, -8.2) * mm, "end": v(-26.63, -8.08) * mm});
            skLineSegment(sketch, "E427", {"start": v(-26.63, -8.08) * mm, "end": v(-26.64, -8) * mm});
            skLineSegment(sketch, "E428", {"start": v(-26.64, -8) * mm, "end": v(-26.64, -7.95) * mm});
            skLineSegment(sketch, "E429", {"start": v(-26.64, -7.95) * mm, "end": v(-26.63, -7.9) * mm});
            skLineSegment(sketch, "E430", {"start": v(-26.63, -7.9) * mm, "end": v(-26.63, -7.86) * mm});
            skLineSegment(sketch, "E431", {"start": v(-26.63, -7.86) * mm, "end": v(-26.63, -7.82) * mm});
            skLineSegment(sketch, "E432", {"start": v(-26.63, -7.82) * mm, "end": v(-26.62, -7.78) * mm});
            skLineSegment(sketch, "E433", {"start": v(-26.62, -7.78) * mm, "end": v(-26.61, -7.74) * mm});
            skLineSegment(sketch, "E434", {"start": v(-26.61, -7.74) * mm, "end": v(-26.6, -7.7) * mm});
            skLineSegment(sketch, "E435", {"start": v(-26.6, -7.7) * mm, "end": v(-26.6, -7.66) * mm});
            skLineSegment(sketch, "E436", {"start": v(-26.6, -7.66) * mm, "end": v(-26.58, -7.62) * mm});
            skLineSegment(sketch, "E437", {"start": v(-26.58, -7.62) * mm, "end": v(-26.56, -7.58) * mm});
            skLineSegment(sketch, "E438", {"start": v(-26.56, -7.58) * mm, "end": v(-26.55, -7.54) * mm});
            skLineSegment(sketch, "E439", {"start": v(-26.55, -7.54) * mm, "end": v(-26.53, -7.5) * mm});
            skLineSegment(sketch, "E440", {"start": v(-26.53, -7.5) * mm, "end": v(-26.5, -7.47) * mm});
            skLineSegment(sketch, "E441", {"start": v(-26.5, -7.47) * mm, "end": v(-26.48, -7.44) * mm});
            skLineSegment(sketch, "E442", {"start": v(-26.48, -7.44) * mm, "end": v(-26.45, -7.4) * mm});
            skLineSegment(sketch, "E443", {"start": v(-26.45, -7.4) * mm, "end": v(-26.42, -7.38) * mm});
            skLineSegment(sketch, "E444", {"start": v(-26.42, -7.38) * mm, "end": v(-26.39, -7.35) * mm});
            skLineSegment(sketch, "E445", {"start": v(-26.39, -7.35) * mm, "end": v(-26.35, -7.32) * mm});
            skLineSegment(sketch, "E446", {"start": v(-7.73, -7.3) * mm, "end": v(-6.66, -7.32) * mm});
            skLineSegment(sketch, "E447", {"start": v(-6.66, -7.32) * mm, "end": v(-6.53, -7.44) * mm});
            skLineSegment(sketch, "E448", {"start": v(-6.53, -7.44) * mm, "end": v(-6.47, -7.53) * mm});
            skLineSegment(sketch, "E449", {"start": v(-6.47, -7.53) * mm, "end": v(-6.44, -7.58) * mm});
            skLineSegment(sketch, "E450", {"start": v(-6.44, -7.58) * mm, "end": v(-6.43, -7.63) * mm});
            skLineSegment(sketch, "E451", {"start": v(-6.43, -7.63) * mm, "end": v(-6.41, -7.68) * mm});
            skLineSegment(sketch, "E452", {"start": v(-6.41, -7.68) * mm, "end": v(-6.4, -7.7) * mm});
            skLineSegment(sketch, "E453", {"start": v(-6.4, -7.7) * mm, "end": v(-6.4, -7.79) * mm});
            skLineSegment(sketch, "E454", {"start": v(-6.4, -7.79) * mm, "end": v(-6.39, -7.96) * mm});
            skLineSegment(sketch, "E455", {"start": v(-6.39, -7.96) * mm, "end": v(-6.38, -8.09) * mm});
            skLineSegment(sketch, "E456", {"start": v(-6.38, -8.09) * mm, "end": v(-6.38, -8.17) * mm});
            skLineSegment(sketch, "E457", {"start": v(-6.38, -8.17) * mm, "end": v(-6.38, -8.22) * mm});
            skLineSegment(sketch, "E458", {"start": v(-6.38, -8.22) * mm, "end": v(-6.38, -8.26) * mm});
            skLineSegment(sketch, "E459", {"start": v(-6.38, -8.26) * mm, "end": v(-6.38, -8.3) * mm});
            skLineSegment(sketch, "E460", {"start": v(-6.38, -8.3) * mm, "end": v(-6.39, -8.34) * mm});
            skLineSegment(sketch, "E461", {"start": v(-6.39, -8.34) * mm, "end": v(-6.4, -8.39) * mm});
            skLineSegment(sketch, "E462", {"start": v(-6.4, -8.39) * mm, "end": v(-6.4, -8.43) * mm});
            skLineSegment(sketch, "E463", {"start": v(-6.4, -8.43) * mm, "end": v(-6.4, -8.47) * mm});
            skLineSegment(sketch, "E464", {"start": v(-6.4, -8.47) * mm, "end": v(-6.42, -8.5) * mm});
            skLineSegment(sketch, "E465", {"start": v(-6.42, -8.5) * mm, "end": v(-6.43, -8.55) * mm});
            skLineSegment(sketch, "E466", {"start": v(-6.43, -8.55) * mm, "end": v(-6.45, -8.58) * mm});
            skLineSegment(sketch, "E467", {"start": v(-6.45, -8.58) * mm, "end": v(-6.47, -8.62) * mm});
            skLineSegment(sketch, "E468", {"start": v(-6.47, -8.62) * mm, "end": v(-6.49, -8.66) * mm});
            skLineSegment(sketch, "E469", {"start": v(-6.49, -8.66) * mm, "end": v(-6.5, -8.7) * mm});
            skLineSegment(sketch, "E470", {"start": v(-6.5, -8.7) * mm, "end": v(-6.53, -8.73) * mm});
            skLineSegment(sketch, "E471", {"start": v(-6.53, -8.73) * mm, "end": v(-6.56, -8.76) * mm});
            skLineSegment(sketch, "E472", {"start": v(-6.56, -8.76) * mm, "end": v(-6.6, -8.79) * mm});
            skLineSegment(sketch, "E473", {"start": v(-6.6, -8.79) * mm, "end": v(-6.62, -8.82) * mm});
            skLineSegment(sketch, "E474", {"start": v(-6.62, -8.82) * mm, "end": v(-6.66, -8.85) * mm});
            skLineSegment(sketch, "E475", {"start": v(-6.66, -8.85) * mm, "end": v(-7.73, -8.87) * mm});
            skLineSegment(sketch, "E476", {"start": v(-7.73, -8.87) * mm, "end": v(-7.73, -7.3) * mm});
            skLineSegment(sketch, "E477", {"start": v(-26.38, -9.67) * mm, "end": v(-26.27, -9.66) * mm});
            skLineSegment(sketch, "E478", {"start": v(-26.27, -9.66) * mm, "end": v(-26.08, -9.64) * mm});
            skLineSegment(sketch, "E479", {"start": v(-26.08, -9.64) * mm, "end": v(-25.28, -9.63) * mm});
            skLineSegment(sketch, "E480", {"start": v(-25.28, -9.63) * mm, "end": v(-25.3, -11.2) * mm});
            skLineSegment(sketch, "E481", {"start": v(-25.3, -11.2) * mm, "end": v(-26.03, -11.2) * mm});
            skLineSegment(sketch, "E482", {"start": v(-26.03, -11.2) * mm, "end": v(-26.17, -11.2) * mm});
            skLineSegment(sketch, "E483", {"start": v(-26.17, -11.2) * mm, "end": v(-26.27, -11.19) * mm});
            skLineSegment(sketch, "E484", {"start": v(-26.27, -11.19) * mm, "end": v(-26.3, -11.18) * mm});
            skLineSegment(sketch, "E485", {"start": v(-26.3, -11.18) * mm, "end": v(-26.34, -11.17) * mm});
            skLineSegment(sketch, "E486", {"start": v(-26.34, -11.17) * mm, "end": v(-26.36, -11.16) * mm});
            skLineSegment(sketch, "E487", {"start": v(-26.36, -11.16) * mm, "end": v(-26.39, -11.15) * mm});
            skLineSegment(sketch, "E488", {"start": v(-26.39, -11.15) * mm, "end": v(-26.41, -11.13) * mm});
            skLineSegment(sketch, "E489", {"start": v(-26.41, -11.13) * mm, "end": v(-26.43, -11.11) * mm});
            skLineSegment(sketch, "E490", {"start": v(-26.43, -11.11) * mm, "end": v(-26.46, -11.1) * mm});
            skLineSegment(sketch, "E491", {"start": v(-26.46, -11.1) * mm, "end": v(-26.47, -11.08) * mm});
            skLineSegment(sketch, "E492", {"start": v(-26.47, -11.08) * mm, "end": v(-26.5, -11.05) * mm});
            skLineSegment(sketch, "E493", {"start": v(-26.5, -11.05) * mm, "end": v(-26.5, -11.03) * mm});
            skLineSegment(sketch, "E494", {"start": v(-26.5, -11.03) * mm, "end": v(-26.52, -11) * mm});
            skLineSegment(sketch, "E495", {"start": v(-26.52, -11) * mm, "end": v(-26.54, -10.98) * mm});
            skLineSegment(sketch, "E496", {"start": v(-26.54, -10.98) * mm, "end": v(-26.55, -10.95) * mm});
            skLineSegment(sketch, "E497", {"start": v(-26.55, -10.95) * mm, "end": v(-26.56, -10.93) * mm});
            skLineSegment(sketch, "E498", {"start": v(-26.56, -10.93) * mm, "end": v(-26.57, -10.9) * mm});
            skLineSegment(sketch, "E499", {"start": v(-26.57, -10.9) * mm, "end": v(-26.58, -10.87) * mm});
            skLineSegment(sketch, "E500", {"start": v(-26.58, -10.87) * mm, "end": v(-26.59, -10.84) * mm});
            skLineSegment(sketch, "E501", {"start": v(-26.59, -10.84) * mm, "end": v(-26.6, -10.78) * mm});
            skLineSegment(sketch, "E502", {"start": v(-26.6, -10.78) * mm, "end": v(-26.61, -10.72) * mm});
            skLineSegment(sketch, "E503", {"start": v(-26.61, -10.72) * mm, "end": v(-26.62, -10.63) * mm});
            skLineSegment(sketch, "E504", {"start": v(-26.62, -10.63) * mm, "end": v(-26.63, -10.55) * mm});
            skLineSegment(sketch, "E505", {"start": v(-26.63, -10.55) * mm, "end": v(-26.63, -10.5) * mm});
            skLineSegment(sketch, "E506", {"start": v(-26.63, -10.5) * mm, "end": v(-26.63, -10.47) * mm});
            skLineSegment(sketch, "E507", {"start": v(-26.63, -10.47) * mm, "end": v(-26.63, -10.38) * mm});
            skLineSegment(sketch, "E508", {"start": v(-26.63, -10.38) * mm, "end": v(-26.62, -10.23) * mm});
            skLineSegment(sketch, "E509", {"start": v(-26.62, -10.23) * mm, "end": v(-26.62, -10.14) * mm});
            skLineSegment(sketch, "E510", {"start": v(-26.62, -10.14) * mm, "end": v(-26.6, -10.08) * mm});
            skLineSegment(sketch, "E511", {"start": v(-26.6, -10.08) * mm, "end": v(-26.6, -10.02) * mm});
            skLineSegment(sketch, "E512", {"start": v(-26.6, -10.02) * mm, "end": v(-26.59, -9.99) * mm});
            skLineSegment(sketch, "E513", {"start": v(-26.59, -9.99) * mm, "end": v(-26.58, -9.96) * mm});
            skLineSegment(sketch, "E514", {"start": v(-26.58, -9.96) * mm, "end": v(-26.57, -9.93) * mm});
            skLineSegment(sketch, "E515", {"start": v(-26.57, -9.93) * mm, "end": v(-26.56, -9.9) * mm});
            skLineSegment(sketch, "E516", {"start": v(-26.56, -9.9) * mm, "end": v(-26.55, -9.87) * mm});
            skLineSegment(sketch, "E517", {"start": v(-26.55, -9.87) * mm, "end": v(-26.54, -9.85) * mm});
            skLineSegment(sketch, "E518", {"start": v(-26.54, -9.85) * mm, "end": v(-26.52, -9.82) * mm});
            skLineSegment(sketch, "E519", {"start": v(-26.52, -9.82) * mm, "end": v(-26.5, -9.8) * mm});
            skLineSegment(sketch, "E520", {"start": v(-26.5, -9.8) * mm, "end": v(-26.49, -9.77) * mm});
            skLineSegment(sketch, "E521", {"start": v(-26.49, -9.77) * mm, "end": v(-26.47, -9.75) * mm});
            skLineSegment(sketch, "E522", {"start": v(-26.47, -9.75) * mm, "end": v(-26.45, -9.73) * mm});
            skLineSegment(sketch, "E523", {"start": v(-26.45, -9.73) * mm, "end": v(-26.43, -9.71) * mm});
            skLineSegment(sketch, "E524", {"start": v(-26.43, -9.71) * mm, "end": v(-26.4, -9.7) * mm});
            skLineSegment(sketch, "E525", {"start": v(-26.4, -9.7) * mm, "end": v(-26.38, -9.67) * mm});
            skLineSegment(sketch, "E526", {"start": v(-7.73, -9.64) * mm, "end": v(-6.54, -9.67) * mm});
            skLineSegment(sketch, "E527", {"start": v(-6.54, -9.67) * mm, "end": v(-6.51, -9.75) * mm});
            skLineSegment(sketch, "E528", {"start": v(-6.51, -9.75) * mm, "end": v(-6.48, -9.83) * mm});
            skLineSegment(sketch, "E529", {"start": v(-6.48, -9.83) * mm, "end": v(-6.46, -9.9) * mm});
            skLineSegment(sketch, "E530", {"start": v(-6.46, -9.9) * mm, "end": v(-6.44, -9.99) * mm});
            skLineSegment(sketch, "E531", {"start": v(-6.44, -9.99) * mm, "end": v(-6.42, -10.07) * mm});
            skLineSegment(sketch, "E532", {"start": v(-6.42, -10.07) * mm, "end": v(-6.4, -10.15) * mm});
            skLineSegment(sketch, "E533", {"start": v(-6.4, -10.15) * mm, "end": v(-6.4, -10.23) * mm});
            skLineSegment(sketch, "E534", {"start": v(-6.4, -10.23) * mm, "end": v(-6.39, -10.32) * mm});
            skLineSegment(sketch, "E535", {"start": v(-6.39, -10.32) * mm, "end": v(-6.38, -10.4) * mm});
            skLineSegment(sketch, "E536", {"start": v(-6.38, -10.4) * mm, "end": v(-6.38, -10.44) * mm});
            skLineSegment(sketch, "E537", {"start": v(-6.38, -10.44) * mm, "end": v(-6.38, -10.48) * mm});
            skLineSegment(sketch, "E538", {"start": v(-6.38, -10.48) * mm, "end": v(-6.38, -10.53) * mm});
            skLineSegment(sketch, "E539", {"start": v(-6.38, -10.53) * mm, "end": v(-6.39, -10.57) * mm});
            skLineSegment(sketch, "E540", {"start": v(-6.39, -10.57) * mm, "end": v(-6.39, -10.6) * mm});
            skLineSegment(sketch, "E541", {"start": v(-6.39, -10.6) * mm, "end": v(-6.4, -10.65) * mm});
            skLineSegment(sketch, "E542", {"start": v(-6.4, -10.65) * mm, "end": v(-6.4, -10.7) * mm});
            skLineSegment(sketch, "E543", {"start": v(-6.4, -10.7) * mm, "end": v(-6.4, -10.73) * mm});
            skLineSegment(sketch, "E544", {"start": v(-6.4, -10.73) * mm, "end": v(-6.41, -10.77) * mm});
            skLineSegment(sketch, "E545", {"start": v(-6.41, -10.77) * mm, "end": v(-6.42, -10.82) * mm});
            skLineSegment(sketch, "E546", {"start": v(-6.42, -10.82) * mm, "end": v(-6.43, -10.86) * mm});
            skLineSegment(sketch, "E547", {"start": v(-6.43, -10.86) * mm, "end": v(-6.45, -10.92) * mm});
            skLineSegment(sketch, "E548", {"start": v(-6.45, -10.92) * mm, "end": v(-6.47, -10.97) * mm});
            skLineSegment(sketch, "E549", {"start": v(-6.47, -10.97) * mm, "end": v(-6.5, -11.03) * mm});
            skLineSegment(sketch, "E550", {"start": v(-6.5, -11.03) * mm, "end": v(-6.53, -11.07) * mm});
            skLineSegment(sketch, "E551", {"start": v(-6.53, -11.07) * mm, "end": v(-6.56, -11.1) * mm});
            skLineSegment(sketch, "E552", {"start": v(-6.56, -11.1) * mm, "end": v(-6.58, -11.12) * mm});
            skLineSegment(sketch, "E553", {"start": v(-6.58, -11.12) * mm, "end": v(-6.6, -11.14) * mm});
            skLineSegment(sketch, "E554", {"start": v(-6.6, -11.14) * mm, "end": v(-6.64, -11.15) * mm});
            skLineSegment(sketch, "E555", {"start": v(-6.64, -11.15) * mm, "end": v(-6.66, -11.17) * mm});
            skLineSegment(sketch, "E556", {"start": v(-6.66, -11.17) * mm, "end": v(-6.7, -11.18) * mm});
            skLineSegment(sketch, "E557", {"start": v(-6.7, -11.18) * mm, "end": v(-6.7, -11.18) * mm});
            skLineSegment(sketch, "E558", {"start": v(-6.7, -11.18) * mm, "end": v(-7.72, -11.2) * mm});
            skLineSegment(sketch, "E559", {"start": v(-7.72, -11.2) * mm, "end": v(-7.73, -9.64) * mm});
            skLineSegment(sketch, "E560", {"start": v(-26.47, -12.01) * mm, "end": v(-25.28, -11.98) * mm});
            skLineSegment(sketch, "E561", {"start": v(-25.28, -11.98) * mm, "end": v(-25.3, -13.53) * mm});
            skLineSegment(sketch, "E562", {"start": v(-25.3, -13.53) * mm, "end": v(-25.33, -13.53) * mm});
            skLineSegment(sketch, "E563", {"start": v(-25.33, -13.53) * mm, "end": v(-25.38, -13.52) * mm});
            skLineSegment(sketch, "E564", {"start": v(-25.38, -13.52) * mm, "end": v(-25.42, -13.52) * mm});
            skLineSegment(sketch, "E565", {"start": v(-25.42, -13.52) * mm, "end": v(-25.47, -13.52) * mm});
            skLineSegment(sketch, "E566", {"start": v(-25.47, -13.52) * mm, "end": v(-25.5, -13.52) * mm});
            skLineSegment(sketch, "E567", {"start": v(-25.5, -13.52) * mm, "end": v(-25.6, -13.53) * mm});
            skLineSegment(sketch, "E568", {"start": v(-25.6, -13.53) * mm, "end": v(-25.88, -13.56) * mm});
            skLineSegment(sketch, "E569", {"start": v(-25.88, -13.56) * mm, "end": v(-25.93, -13.56) * mm});
            skLineSegment(sketch, "E570", {"start": v(-25.93, -13.56) * mm, "end": v(-25.97, -13.56) * mm});
            skLineSegment(sketch, "E571", {"start": v(-25.97, -13.56) * mm, "end": v(-26.02, -13.56) * mm});
            skLineSegment(sketch, "E572", {"start": v(-26.02, -13.56) * mm, "end": v(-26.06, -13.56) * mm});
            skLineSegment(sketch, "E573", {"start": v(-26.06, -13.56) * mm, "end": v(-26.1, -13.56) * mm});
            skLineSegment(sketch, "E574", {"start": v(-26.1, -13.56) * mm, "end": v(-26.15, -13.56) * mm});
            skLineSegment(sketch, "E575", {"start": v(-26.15, -13.56) * mm, "end": v(-26.2, -13.55) * mm});
            skLineSegment(sketch, "E576", {"start": v(-26.2, -13.55) * mm, "end": v(-26.24, -13.54) * mm});
            skLineSegment(sketch, "E577", {"start": v(-26.24, -13.54) * mm, "end": v(-26.28, -13.53) * mm});
            skLineSegment(sketch, "E578", {"start": v(-26.28, -13.53) * mm, "end": v(-26.32, -13.52) * mm});
            skLineSegment(sketch, "E579", {"start": v(-26.32, -13.52) * mm, "end": v(-26.36, -13.5) * mm});
            skLineSegment(sketch, "E580", {"start": v(-26.36, -13.5) * mm, "end": v(-26.4, -13.48) * mm});
            skLineSegment(sketch, "E581", {"start": v(-26.4, -13.48) * mm, "end": v(-26.43, -13.45) * mm});
            skLineSegment(sketch, "E582", {"start": v(-26.43, -13.45) * mm, "end": v(-26.46, -13.43) * mm});
            skLineSegment(sketch, "E583", {"start": v(-26.46, -13.43) * mm, "end": v(-26.5, -13.4) * mm});
            skLineSegment(sketch, "E584", {"start": v(-26.5, -13.4) * mm, "end": v(-26.53, -13.36) * mm});
            skLineSegment(sketch, "E585", {"start": v(-26.53, -13.36) * mm, "end": v(-26.55, -13.31) * mm});
            skLineSegment(sketch, "E586", {"start": v(-26.55, -13.31) * mm, "end": v(-26.56, -13.27) * mm});
            skLineSegment(sketch, "E587", {"start": v(-26.56, -13.27) * mm, "end": v(-26.57, -13.22) * mm});
            skLineSegment(sketch, "E588", {"start": v(-26.57, -13.22) * mm, "end": v(-26.59, -13.18) * mm});
            skLineSegment(sketch, "E589", {"start": v(-26.59, -13.18) * mm, "end": v(-26.6, -13.13) * mm});
            skLineSegment(sketch, "E590", {"start": v(-26.6, -13.13) * mm, "end": v(-26.6, -13.08) * mm});
            skLineSegment(sketch, "E591", {"start": v(-26.6, -13.08) * mm, "end": v(-26.61, -13.04) * mm});
            skLineSegment(sketch, "E592", {"start": v(-26.61, -13.04) * mm, "end": v(-26.62, -12.99) * mm});
            skLineSegment(sketch, "E593", {"start": v(-26.62, -12.99) * mm, "end": v(-26.63, -12.94) * mm});
            skLineSegment(sketch, "E594", {"start": v(-26.63, -12.94) * mm, "end": v(-26.63, -12.9) * mm});
            skLineSegment(sketch, "E595", {"start": v(-26.63, -12.9) * mm, "end": v(-26.63, -12.85) * mm});
            skLineSegment(sketch, "E596", {"start": v(-26.63, -12.85) * mm, "end": v(-26.63, -12.8) * mm});
            skLineSegment(sketch, "E597", {"start": v(-26.63, -12.8) * mm, "end": v(-26.63, -12.75) * mm});
            skLineSegment(sketch, "E598", {"start": v(-26.63, -12.75) * mm, "end": v(-26.63, -12.7) * mm});
            skLineSegment(sketch, "E599", {"start": v(-26.63, -12.7) * mm, "end": v(-26.63, -12.66) * mm});
            skLineSegment(sketch, "E600", {"start": v(-26.63, -12.66) * mm, "end": v(-26.62, -12.6) * mm});
            skLineSegment(sketch, "E601", {"start": v(-26.62, -12.6) * mm, "end": v(-26.62, -12.56) * mm});
            skLineSegment(sketch, "E602", {"start": v(-26.62, -12.56) * mm, "end": v(-26.61, -12.51) * mm});
            skLineSegment(sketch, "E603", {"start": v(-26.61, -12.51) * mm, "end": v(-26.6, -12.47) * mm});
            skLineSegment(sketch, "E604", {"start": v(-26.6, -12.47) * mm, "end": v(-26.6, -12.42) * mm});
            skLineSegment(sketch, "E605", {"start": v(-26.6, -12.42) * mm, "end": v(-26.59, -12.37) * mm});
            skLineSegment(sketch, "E606", {"start": v(-26.59, -12.37) * mm, "end": v(-26.58, -12.33) * mm});
            skLineSegment(sketch, "E607", {"start": v(-26.58, -12.33) * mm, "end": v(-26.56, -12.28) * mm});
            skLineSegment(sketch, "E608", {"start": v(-26.56, -12.28) * mm, "end": v(-26.55, -12.23) * mm});
            skLineSegment(sketch, "E609", {"start": v(-26.55, -12.23) * mm, "end": v(-26.54, -12.19) * mm});
            skLineSegment(sketch, "E610", {"start": v(-26.54, -12.19) * mm, "end": v(-26.52, -12.14) * mm});
            skLineSegment(sketch, "E611", {"start": v(-26.52, -12.14) * mm, "end": v(-26.5, -12.1) * mm});
            skLineSegment(sketch, "E612", {"start": v(-26.5, -12.1) * mm, "end": v(-26.49, -12.05) * mm});
            skLineSegment(sketch, "E613", {"start": v(-26.49, -12.05) * mm, "end": v(-26.47, -12.01) * mm});
            skLineSegment(sketch, "E614", {"start": v(-7.73, -11.98) * mm, "end": v(-6.54, -12.01) * mm});
            skLineSegment(sketch, "E615", {"start": v(-6.54, -12.01) * mm, "end": v(-6.52, -12.06) * mm});
            skLineSegment(sketch, "E616", {"start": v(-6.52, -12.06) * mm, "end": v(-6.5, -12.1) * mm});
            skLineSegment(sketch, "E617", {"start": v(-6.5, -12.1) * mm, "end": v(-6.49, -12.16) * mm});
            skLineSegment(sketch, "E618", {"start": v(-6.49, -12.16) * mm, "end": v(-6.47, -12.2) * mm});
            skLineSegment(sketch, "E619", {"start": v(-6.47, -12.2) * mm, "end": v(-6.46, -12.26) * mm});
            skLineSegment(sketch, "E620", {"start": v(-6.46, -12.26) * mm, "end": v(-6.44, -12.31) * mm});
            skLineSegment(sketch, "E621", {"start": v(-6.44, -12.31) * mm, "end": v(-6.43, -12.37) * mm});
            skLineSegment(sketch, "E622", {"start": v(-6.43, -12.37) * mm, "end": v(-6.42, -12.42) * mm});
            skLineSegment(sketch, "E623", {"start": v(-6.42, -12.42) * mm, "end": v(-6.4, -12.48) * mm});
            skLineSegment(sketch, "E624", {"start": v(-6.4, -12.48) * mm, "end": v(-6.4, -12.53) * mm});
            skLineSegment(sketch, "E625", {"start": v(-6.4, -12.53) * mm, "end": v(-6.39, -12.59) * mm});
            skLineSegment(sketch, "E626", {"start": v(-6.39, -12.59) * mm, "end": v(-6.38, -12.64) * mm});
            skLineSegment(sketch, "E627", {"start": v(-6.38, -12.64) * mm, "end": v(-6.38, -12.7) * mm});
            skLineSegment(sketch, "E628", {"start": v(-6.38, -12.7) * mm, "end": v(-6.37, -12.75) * mm});
            skLineSegment(sketch, "E629", {"start": v(-6.37, -12.75) * mm, "end": v(-6.37, -12.8) * mm});
            skLineSegment(sketch, "E630", {"start": v(-6.37, -12.8) * mm, "end": v(-6.37, -12.86) * mm});
            skLineSegment(sketch, "E631", {"start": v(-6.37, -12.86) * mm, "end": v(-6.38, -12.91) * mm});
            skLineSegment(sketch, "E632", {"start": v(-6.38, -12.91) * mm, "end": v(-6.38, -12.97) * mm});
            skLineSegment(sketch, "E633", {"start": v(-6.38, -12.97) * mm, "end": v(-6.39, -13.02) * mm});
            skLineSegment(sketch, "E634", {"start": v(-6.39, -13.02) * mm, "end": v(-6.4, -13.07) * mm});
            skLineSegment(sketch, "E635", {"start": v(-6.4, -13.07) * mm, "end": v(-6.4, -13.12) * mm});
            skLineSegment(sketch, "E636", {"start": v(-6.4, -13.12) * mm, "end": v(-6.42, -13.17) * mm});
            skLineSegment(sketch, "E637", {"start": v(-6.42, -13.17) * mm, "end": v(-6.44, -13.22) * mm});
            skLineSegment(sketch, "E638", {"start": v(-6.44, -13.22) * mm, "end": v(-6.46, -13.27) * mm});
            skLineSegment(sketch, "E639", {"start": v(-6.46, -13.27) * mm, "end": v(-6.49, -13.32) * mm});
            skLineSegment(sketch, "E640", {"start": v(-6.49, -13.32) * mm, "end": v(-6.51, -13.36) * mm});
            skLineSegment(sketch, "E641", {"start": v(-6.51, -13.36) * mm, "end": v(-6.54, -13.4) * mm});
            skLineSegment(sketch, "E642", {"start": v(-6.54, -13.4) * mm, "end": v(-6.58, -13.45) * mm});
            skLineSegment(sketch, "E643", {"start": v(-6.58, -13.45) * mm, "end": v(-6.61, -13.49) * mm});
            skLineSegment(sketch, "E644", {"start": v(-6.61, -13.49) * mm, "end": v(-6.65, -13.5) * mm});
            skLineSegment(sketch, "E645", {"start": v(-6.65, -13.5) * mm, "end": v(-6.69, -13.5) * mm});
            skLineSegment(sketch, "E646", {"start": v(-6.69, -13.5) * mm, "end": v(-6.72, -13.52) * mm});
            skLineSegment(sketch, "E647", {"start": v(-6.72, -13.52) * mm, "end": v(-6.76, -13.52) * mm});
            skLineSegment(sketch, "E648", {"start": v(-6.76, -13.52) * mm, "end": v(-6.8, -13.53) * mm});
            skLineSegment(sketch, "E649", {"start": v(-6.8, -13.53) * mm, "end": v(-6.87, -13.54) * mm});
            skLineSegment(sketch, "E650", {"start": v(-6.87, -13.54) * mm, "end": v(-6.95, -13.55) * mm});
            skLineSegment(sketch, "E651", {"start": v(-6.95, -13.55) * mm, "end": v(-7.06, -13.55) * mm});
            skLineSegment(sketch, "E652", {"start": v(-7.06, -13.55) * mm, "end": v(-7.6, -13.53) * mm});
            skLineSegment(sketch, "E653", {"start": v(-7.6, -13.53) * mm, "end": v(-7.72, -13.53) * mm});
            skLineSegment(sketch, "E654", {"start": v(-7.72, -13.53) * mm, "end": v(-7.73, -11.98) * mm});
            skLineSegment(sketch, "E655", {"start": v(-20.77, -15.27) * mm, "end": v(-19.21, -15.27) * mm});
            skLineSegment(sketch, "E656", {"start": v(-19.21, -15.27) * mm, "end": v(-19.21, -16.13) * mm});
            skLineSegment(sketch, "E657", {"start": v(-19.21, -16.13) * mm, "end": v(-19.22, -16.27) * mm});
            skLineSegment(sketch, "E658", {"start": v(-19.22, -16.27) * mm, "end": v(-19.23, -16.29) * mm});
            skLineSegment(sketch, "E659", {"start": v(-19.23, -16.29) * mm, "end": v(-19.23, -16.3) * mm});
            skLineSegment(sketch, "E660", {"start": v(-19.23, -16.3) * mm, "end": v(-19.24, -16.32) * mm});
            skLineSegment(sketch, "E661", {"start": v(-19.24, -16.32) * mm, "end": v(-19.24, -16.34) * mm});
            skLineSegment(sketch, "E662", {"start": v(-19.24, -16.34) * mm, "end": v(-19.25, -16.35) * mm});
            skLineSegment(sketch, "E663", {"start": v(-19.25, -16.35) * mm, "end": v(-19.26, -16.37) * mm});
            skLineSegment(sketch, "E664", {"start": v(-19.26, -16.37) * mm, "end": v(-19.27, -16.38) * mm});
            skLineSegment(sketch, "E665", {"start": v(-19.27, -16.38) * mm, "end": v(-19.28, -16.4) * mm});
            skLineSegment(sketch, "E666", {"start": v(-19.28, -16.4) * mm, "end": v(-19.3, -16.41) * mm});
            skLineSegment(sketch, "E667", {"start": v(-19.3, -16.41) * mm, "end": v(-19.32, -16.43) * mm});
            skLineSegment(sketch, "E668", {"start": v(-19.32, -16.43) * mm, "end": v(-19.34, -16.46) * mm});
            skLineSegment(sketch, "E669", {"start": v(-19.34, -16.46) * mm, "end": v(-19.39, -16.49) * mm});
            skLineSegment(sketch, "E670", {"start": v(-19.39, -16.49) * mm, "end": v(-19.47, -16.53) * mm});
            skLineSegment(sketch, "E671", {"start": v(-19.47, -16.53) * mm, "end": v(-19.6, -16.58) * mm});
            skLineSegment(sketch, "E672", {"start": v(-19.6, -16.58) * mm, "end": v(-19.69, -16.6) * mm});
            skLineSegment(sketch, "E673", {"start": v(-19.69, -16.6) * mm, "end": v(-19.73, -16.6) * mm});
            skLineSegment(sketch, "E674", {"start": v(-19.73, -16.6) * mm, "end": v(-19.77, -16.6) * mm});
            skLineSegment(sketch, "E675", {"start": v(-19.77, -16.6) * mm, "end": v(-19.81, -16.61) * mm});
            skLineSegment(sketch, "E676", {"start": v(-19.81, -16.61) * mm, "end": v(-19.86, -16.62) * mm});
            skLineSegment(sketch, "E677", {"start": v(-19.86, -16.62) * mm, "end": v(-19.9, -16.62) * mm});
            skLineSegment(sketch, "E678", {"start": v(-19.9, -16.62) * mm, "end": v(-19.94, -16.62) * mm});
            skLineSegment(sketch, "E679", {"start": v(-19.94, -16.62) * mm, "end": v(-19.98, -16.62) * mm});
            skLineSegment(sketch, "E680", {"start": v(-19.98, -16.62) * mm, "end": v(-20.03, -16.62) * mm});
            skLineSegment(sketch, "E681", {"start": v(-20.03, -16.62) * mm, "end": v(-20.07, -16.62) * mm});
            skLineSegment(sketch, "E682", {"start": v(-20.07, -16.62) * mm, "end": v(-20.11, -16.62) * mm});
            skLineSegment(sketch, "E683", {"start": v(-20.11, -16.62) * mm, "end": v(-20.15, -16.62) * mm});
            skLineSegment(sketch, "E684", {"start": v(-20.15, -16.62) * mm, "end": v(-20.2, -16.61) * mm});
            skLineSegment(sketch, "E685", {"start": v(-20.2, -16.61) * mm, "end": v(-20.24, -16.6) * mm});
            skLineSegment(sketch, "E686", {"start": v(-20.24, -16.6) * mm, "end": v(-20.28, -16.6) * mm});
            skLineSegment(sketch, "E687", {"start": v(-20.28, -16.6) * mm, "end": v(-20.32, -16.6) * mm});
            skLineSegment(sketch, "E688", {"start": v(-20.32, -16.6) * mm, "end": v(-20.36, -16.58) * mm});
            skLineSegment(sketch, "E689", {"start": v(-20.36, -16.58) * mm, "end": v(-20.4, -16.57) * mm});
            skLineSegment(sketch, "E690", {"start": v(-20.4, -16.57) * mm, "end": v(-20.44, -16.56) * mm});
            skLineSegment(sketch, "E691", {"start": v(-20.44, -16.56) * mm, "end": v(-20.48, -16.54) * mm});
            skLineSegment(sketch, "E692", {"start": v(-20.48, -16.54) * mm, "end": v(-20.52, -16.53) * mm});
            skLineSegment(sketch, "E693", {"start": v(-20.52, -16.53) * mm, "end": v(-20.56, -16.51) * mm});
            skLineSegment(sketch, "E694", {"start": v(-20.56, -16.51) * mm, "end": v(-20.6, -16.5) * mm});
            skLineSegment(sketch, "E695", {"start": v(-20.6, -16.5) * mm, "end": v(-20.64, -16.47) * mm});
            skLineSegment(sketch, "E696", {"start": v(-20.64, -16.47) * mm, "end": v(-20.68, -16.45) * mm});
            skLineSegment(sketch, "E697", {"start": v(-20.68, -16.45) * mm, "end": v(-20.71, -16.43) * mm});
            skLineSegment(sketch, "E698", {"start": v(-20.71, -16.43) * mm, "end": v(-20.75, -16.4) * mm});
            skLineSegment(sketch, "E699", {"start": v(-20.75, -16.4) * mm, "end": v(-20.78, -16.38) * mm});
            skLineSegment(sketch, "E700", {"start": v(-20.78, -16.38) * mm, "end": v(-20.77, -15.27) * mm});
            skLineSegment(sketch, "E701", {"start": v(-18.48, -15.27) * mm, "end": v(-16.91, -15.27) * mm});
            skLineSegment(sketch, "E702", {"start": v(-16.91, -15.27) * mm, "end": v(-16.89, -16.15) * mm});
            skLineSegment(sketch, "E703", {"start": v(-16.89, -16.15) * mm, "end": v(-16.9, -16.21) * mm});
            skLineSegment(sketch, "E704", {"start": v(-16.9, -16.21) * mm, "end": v(-16.9, -16.27) * mm});
            skLineSegment(sketch, "E705", {"start": v(-16.9, -16.27) * mm, "end": v(-16.93, -16.32) * mm});
            skLineSegment(sketch, "E706", {"start": v(-16.93, -16.32) * mm, "end": v(-16.96, -16.37) * mm});
            skLineSegment(sketch, "E707", {"start": v(-16.96, -16.37) * mm, "end": v(-17, -16.42) * mm});
            skLineSegment(sketch, "E708", {"start": v(-17, -16.42) * mm, "end": v(-17.02, -16.45) * mm});
            skLineSegment(sketch, "E709", {"start": v(-17.02, -16.45) * mm, "end": v(-17.04, -16.47) * mm});
            skLineSegment(sketch, "E710", {"start": v(-17.04, -16.47) * mm, "end": v(-17.07, -16.5) * mm});
            skLineSegment(sketch, "E711", {"start": v(-17.07, -16.5) * mm, "end": v(-17.1, -16.52) * mm});
            skLineSegment(sketch, "E712", {"start": v(-17.1, -16.52) * mm, "end": v(-17.13, -16.54) * mm});
            skLineSegment(sketch, "E713", {"start": v(-17.13, -16.54) * mm, "end": v(-17.15, -16.55) * mm});
            skLineSegment(sketch, "E714", {"start": v(-17.15, -16.55) * mm, "end": v(-17.17, -16.56) * mm});
            skLineSegment(sketch, "E715", {"start": v(-17.17, -16.56) * mm, "end": v(-17.19, -16.56) * mm});
            skLineSegment(sketch, "E716", {"start": v(-17.19, -16.56) * mm, "end": v(-17.2, -16.57) * mm});
            skLineSegment(sketch, "E717", {"start": v(-17.2, -16.57) * mm, "end": v(-17.22, -16.57) * mm});
            skLineSegment(sketch, "E718", {"start": v(-17.22, -16.57) * mm, "end": v(-17.24, -16.57) * mm});
            skLineSegment(sketch, "E719", {"start": v(-17.24, -16.57) * mm, "end": v(-17.26, -16.58) * mm});
            skLineSegment(sketch, "E720", {"start": v(-17.26, -16.58) * mm, "end": v(-17.3, -16.58) * mm});
            skLineSegment(sketch, "E721", {"start": v(-17.3, -16.58) * mm, "end": v(-17.39, -16.6) * mm});
            skLineSegment(sketch, "E722", {"start": v(-17.39, -16.6) * mm, "end": v(-17.47, -16.61) * mm});
            skLineSegment(sketch, "E723", {"start": v(-17.47, -16.61) * mm, "end": v(-17.56, -16.62) * mm});
            skLineSegment(sketch, "E724", {"start": v(-17.56, -16.62) * mm, "end": v(-17.6, -16.62) * mm});
            skLineSegment(sketch, "E725", {"start": v(-17.6, -16.62) * mm, "end": v(-17.65, -16.63) * mm});
            skLineSegment(sketch, "E726", {"start": v(-17.65, -16.63) * mm, "end": v(-17.7, -16.63) * mm});
            skLineSegment(sketch, "E727", {"start": v(-17.7, -16.63) * mm, "end": v(-17.74, -16.63) * mm});
            skLineSegment(sketch, "E728", {"start": v(-17.74, -16.63) * mm, "end": v(-17.79, -16.63) * mm});
            skLineSegment(sketch, "E729", {"start": v(-17.79, -16.63) * mm, "end": v(-17.83, -16.62) * mm});
            skLineSegment(sketch, "E730", {"start": v(-17.83, -16.62) * mm, "end": v(-17.88, -16.62) * mm});
            skLineSegment(sketch, "E731", {"start": v(-17.88, -16.62) * mm, "end": v(-17.92, -16.61) * mm});
            skLineSegment(sketch, "E732", {"start": v(-17.92, -16.61) * mm, "end": v(-17.96, -16.6) * mm});
            skLineSegment(sketch, "E733", {"start": v(-17.96, -16.6) * mm, "end": v(-18, -16.6) * mm});
            skLineSegment(sketch, "E734", {"start": v(-18, -16.6) * mm, "end": v(-18.05, -16.59) * mm});
            skLineSegment(sketch, "E735", {"start": v(-18.05, -16.59) * mm, "end": v(-18.1, -16.57) * mm});
            skLineSegment(sketch, "E736", {"start": v(-18.1, -16.57) * mm, "end": v(-18.13, -16.56) * mm});
            skLineSegment(sketch, "E737", {"start": v(-18.13, -16.56) * mm, "end": v(-18.17, -16.54) * mm});
            skLineSegment(sketch, "E738", {"start": v(-18.17, -16.54) * mm, "end": v(-18.2, -16.52) * mm});
            skLineSegment(sketch, "E739", {"start": v(-18.2, -16.52) * mm, "end": v(-18.25, -16.5) * mm});
            skLineSegment(sketch, "E740", {"start": v(-18.25, -16.5) * mm, "end": v(-18.28, -16.48) * mm});
            skLineSegment(sketch, "E741", {"start": v(-18.28, -16.48) * mm, "end": v(-18.32, -16.45) * mm});
            skLineSegment(sketch, "E742", {"start": v(-18.32, -16.45) * mm, "end": v(-18.35, -16.42) * mm});
            skLineSegment(sketch, "E743", {"start": v(-18.35, -16.42) * mm, "end": v(-18.38, -16.39) * mm});
            skLineSegment(sketch, "E744", {"start": v(-18.38, -16.39) * mm, "end": v(-18.4, -16.35) * mm});
            skLineSegment(sketch, "E745", {"start": v(-18.4, -16.35) * mm, "end": v(-18.44, -16.32) * mm});
            skLineSegment(sketch, "E746", {"start": v(-18.44, -16.32) * mm, "end": v(-18.45, -16.25) * mm});
            skLineSegment(sketch, "E747", {"start": v(-18.45, -16.25) * mm, "end": v(-18.46, -16.14) * mm});
            skLineSegment(sketch, "E748", {"start": v(-18.46, -16.14) * mm, "end": v(-18.48, -15.96) * mm});
            skLineSegment(sketch, "E749", {"start": v(-18.48, -15.96) * mm, "end": v(-18.48, -15.27) * mm});
            skLineSegment(sketch, "E750", {"start": v(-16.1, -15.27) * mm, "end": v(-14.53, -15.27) * mm});
            skLineSegment(sketch, "E751", {"start": v(-14.53, -15.27) * mm, "end": v(-14.53, -15.99) * mm});
            skLineSegment(sketch, "E752", {"start": v(-14.53, -15.99) * mm, "end": v(-14.54, -16.16) * mm});
            skLineSegment(sketch, "E753", {"start": v(-14.54, -16.16) * mm, "end": v(-14.55, -16.26) * mm});
            skLineSegment(sketch, "E754", {"start": v(-14.55, -16.26) * mm, "end": v(-14.57, -16.3) * mm});
            skLineSegment(sketch, "E755", {"start": v(-14.57, -16.3) * mm, "end": v(-14.59, -16.33) * mm});
            skLineSegment(sketch, "E756", {"start": v(-14.59, -16.33) * mm, "end": v(-14.6, -16.36) * mm});
            skLineSegment(sketch, "E757", {"start": v(-14.6, -16.36) * mm, "end": v(-14.63, -16.38) * mm});
            skLineSegment(sketch, "E758", {"start": v(-14.63, -16.38) * mm, "end": v(-14.65, -16.41) * mm});
            skLineSegment(sketch, "E759", {"start": v(-14.65, -16.41) * mm, "end": v(-14.67, -16.44) * mm});
            skLineSegment(sketch, "E760", {"start": v(-14.67, -16.44) * mm, "end": v(-14.7, -16.46) * mm});
            skLineSegment(sketch, "E761", {"start": v(-14.7, -16.46) * mm, "end": v(-14.73, -16.48) * mm});
            skLineSegment(sketch, "E762", {"start": v(-14.73, -16.48) * mm, "end": v(-14.76, -16.5) * mm});
            skLineSegment(sketch, "E763", {"start": v(-14.76, -16.5) * mm, "end": v(-14.78, -16.52) * mm});
            skLineSegment(sketch, "E764", {"start": v(-14.78, -16.52) * mm, "end": v(-14.82, -16.53) * mm});
            skLineSegment(sketch, "E765", {"start": v(-14.82, -16.53) * mm, "end": v(-14.85, -16.55) * mm});
            skLineSegment(sketch, "E766", {"start": v(-14.85, -16.55) * mm, "end": v(-14.88, -16.56) * mm});
            skLineSegment(sketch, "E767", {"start": v(-14.88, -16.56) * mm, "end": v(-14.91, -16.57) * mm});
            skLineSegment(sketch, "E768", {"start": v(-14.91, -16.57) * mm, "end": v(-14.95, -16.58) * mm});
            skLineSegment(sketch, "E769", {"start": v(-14.95, -16.58) * mm, "end": v(-14.98, -16.59) * mm});
            skLineSegment(sketch, "E770", {"start": v(-14.98, -16.59) * mm, "end": v(-15.02, -16.6) * mm});
            skLineSegment(sketch, "E771", {"start": v(-15.02, -16.6) * mm, "end": v(-15.05, -16.6) * mm});
            skLineSegment(sketch, "E772", {"start": v(-15.05, -16.6) * mm, "end": v(-15.1, -16.6) * mm});
            skLineSegment(sketch, "E773", {"start": v(-15.1, -16.6) * mm, "end": v(-15.16, -16.61) * mm});
            skLineSegment(sketch, "E774", {"start": v(-15.16, -16.61) * mm, "end": v(-15.24, -16.62) * mm});
            skLineSegment(sketch, "E775", {"start": v(-15.24, -16.62) * mm, "end": v(-15.3, -16.62) * mm});
            skLineSegment(sketch, "E776", {"start": v(-15.3, -16.62) * mm, "end": v(-15.38, -16.62) * mm});
            skLineSegment(sketch, "E777", {"start": v(-15.38, -16.62) * mm, "end": v(-15.44, -16.61) * mm});
            skLineSegment(sketch, "E778", {"start": v(-15.44, -16.61) * mm, "end": v(-15.5, -16.62) * mm});
            skLineSegment(sketch, "E779", {"start": v(-15.5, -16.62) * mm, "end": v(-15.55, -16.61) * mm});
            skLineSegment(sketch, "E780", {"start": v(-15.55, -16.61) * mm, "end": v(-15.6, -16.6) * mm});
            skLineSegment(sketch, "E781", {"start": v(-15.6, -16.6) * mm, "end": v(-15.66, -16.6) * mm});
            skLineSegment(sketch, "E782", {"start": v(-15.66, -16.6) * mm, "end": v(-15.71, -16.59) * mm});
            skLineSegment(sketch, "E783", {"start": v(-15.71, -16.59) * mm, "end": v(-15.74, -16.58) * mm});
            skLineSegment(sketch, "E784", {"start": v(-15.74, -16.58) * mm, "end": v(-15.77, -16.57) * mm});
            skLineSegment(sketch, "E785", {"start": v(-15.77, -16.57) * mm, "end": v(-15.8, -16.56) * mm});
            skLineSegment(sketch, "E786", {"start": v(-15.8, -16.56) * mm, "end": v(-15.82, -16.55) * mm});
            skLineSegment(sketch, "E787", {"start": v(-15.82, -16.55) * mm, "end": v(-15.84, -16.54) * mm});
            skLineSegment(sketch, "E788", {"start": v(-15.84, -16.54) * mm, "end": v(-15.87, -16.53) * mm});
            skLineSegment(sketch, "E789", {"start": v(-15.87, -16.53) * mm, "end": v(-15.9, -16.52) * mm});
            skLineSegment(sketch, "E790", {"start": v(-15.9, -16.52) * mm, "end": v(-15.92, -16.5) * mm});
            skLineSegment(sketch, "E791", {"start": v(-15.92, -16.5) * mm, "end": v(-15.94, -16.49) * mm});
            skLineSegment(sketch, "E792", {"start": v(-15.94, -16.49) * mm, "end": v(-15.96, -16.47) * mm});
            skLineSegment(sketch, "E793", {"start": v(-15.96, -16.47) * mm, "end": v(-15.98, -16.46) * mm});
            skLineSegment(sketch, "E794", {"start": v(-15.98, -16.46) * mm, "end": v(-16, -16.44) * mm});
            skLineSegment(sketch, "E795", {"start": v(-16, -16.44) * mm, "end": v(-16.02, -16.42) * mm});
            skLineSegment(sketch, "E796", {"start": v(-16.02, -16.42) * mm, "end": v(-16.04, -16.4) * mm});
            skLineSegment(sketch, "E797", {"start": v(-16.04, -16.4) * mm, "end": v(-16.05, -16.38) * mm});
            skLineSegment(sketch, "E798", {"start": v(-16.05, -16.38) * mm, "end": v(-16.07, -16.35) * mm});
            skLineSegment(sketch, "E799", {"start": v(-16.07, -16.35) * mm, "end": v(-16.08, -16.33) * mm});
            skLineSegment(sketch, "E800", {"start": v(-16.08, -16.33) * mm, "end": v(-16.1, -16.3) * mm});
            skLineSegment(sketch, "E801", {"start": v(-16.1, -16.3) * mm, "end": v(-16.1, -16.28) * mm});
            skLineSegment(sketch, "E802", {"start": v(-16.1, -16.28) * mm, "end": v(-16.12, -16.18) * mm});
            skLineSegment(sketch, "E803", {"start": v(-16.12, -16.18) * mm, "end": v(-16.13, -16.04) * mm});
            skLineSegment(sketch, "E804", {"start": v(-16.13, -16.04) * mm, "end": v(-16.13, -15.76) * mm});
            skLineSegment(sketch, "E805", {"start": v(-16.13, -15.76) * mm, "end": v(-16.1, -15.27) * mm});
            skLineSegment(sketch, "E806", {"start": v(-13.8, -15.27) * mm, "end": v(-12.24, -15.27) * mm});
            skLineSegment(sketch, "E807", {"start": v(-12.24, -15.27) * mm, "end": v(-12.23, -16.38) * mm});
            skLineSegment(sketch, "E808", {"start": v(-12.23, -16.38) * mm, "end": v(-12.27, -16.4) * mm});
            skLineSegment(sketch, "E809", {"start": v(-12.27, -16.4) * mm, "end": v(-12.3, -16.43) * mm});
            skLineSegment(sketch, "E810", {"start": v(-12.3, -16.43) * mm, "end": v(-12.34, -16.45) * mm});
            skLineSegment(sketch, "E811", {"start": v(-12.34, -16.45) * mm, "end": v(-12.38, -16.48) * mm});
            skLineSegment(sketch, "E812", {"start": v(-12.38, -16.48) * mm, "end": v(-12.42, -16.5) * mm});
            skLineSegment(sketch, "E813", {"start": v(-12.42, -16.5) * mm, "end": v(-12.46, -16.51) * mm});
            skLineSegment(sketch, "E814", {"start": v(-12.46, -16.51) * mm, "end": v(-12.5, -16.53) * mm});
            skLineSegment(sketch, "E815", {"start": v(-12.5, -16.53) * mm, "end": v(-12.54, -16.55) * mm});
            skLineSegment(sketch, "E816", {"start": v(-12.54, -16.55) * mm, "end": v(-12.58, -16.56) * mm});
            skLineSegment(sketch, "E817", {"start": v(-12.58, -16.56) * mm, "end": v(-12.62, -16.57) * mm});
            skLineSegment(sketch, "E818", {"start": v(-12.62, -16.57) * mm, "end": v(-12.66, -16.58) * mm});
            skLineSegment(sketch, "E819", {"start": v(-12.66, -16.58) * mm, "end": v(-12.7, -16.6) * mm});
            skLineSegment(sketch, "E820", {"start": v(-12.7, -16.6) * mm, "end": v(-12.75, -16.6) * mm});
            skLineSegment(sketch, "E821", {"start": v(-12.75, -16.6) * mm, "end": v(-12.8, -16.6) * mm});
            skLineSegment(sketch, "E822", {"start": v(-12.8, -16.6) * mm, "end": v(-12.84, -16.61) * mm});
            skLineSegment(sketch, "E823", {"start": v(-12.84, -16.61) * mm, "end": v(-12.88, -16.62) * mm});
            skLineSegment(sketch, "E824", {"start": v(-12.88, -16.62) * mm, "end": v(-12.92, -16.62) * mm});
            skLineSegment(sketch, "E825", {"start": v(-12.92, -16.62) * mm, "end": v(-12.97, -16.62) * mm});
            skLineSegment(sketch, "E826", {"start": v(-12.97, -16.62) * mm, "end": v(-13.01, -16.62) * mm});
            skLineSegment(sketch, "E827", {"start": v(-13.01, -16.62) * mm, "end": v(-13.05, -16.62) * mm});
            skLineSegment(sketch, "E828", {"start": v(-13.05, -16.62) * mm, "end": v(-13.1, -16.62) * mm});
            skLineSegment(sketch, "E829", {"start": v(-13.1, -16.62) * mm, "end": v(-13.14, -16.62) * mm});
            skLineSegment(sketch, "E830", {"start": v(-13.14, -16.62) * mm, "end": v(-13.19, -16.61) * mm});
            skLineSegment(sketch, "E831", {"start": v(-13.19, -16.61) * mm, "end": v(-13.23, -16.6) * mm});
            skLineSegment(sketch, "E832", {"start": v(-13.23, -16.6) * mm, "end": v(-13.27, -16.6) * mm});
            skLineSegment(sketch, "E833", {"start": v(-13.27, -16.6) * mm, "end": v(-13.32, -16.6) * mm});
            skLineSegment(sketch, "E834", {"start": v(-13.32, -16.6) * mm, "end": v(-13.36, -16.59) * mm});
            skLineSegment(sketch, "E835", {"start": v(-13.36, -16.59) * mm, "end": v(-13.4, -16.58) * mm});
            skLineSegment(sketch, "E836", {"start": v(-13.4, -16.58) * mm, "end": v(-13.44, -16.57) * mm});
            skLineSegment(sketch, "E837", {"start": v(-13.44, -16.57) * mm, "end": v(-13.63, -16.48) * mm});
            skLineSegment(sketch, "E838", {"start": v(-13.63, -16.48) * mm, "end": v(-13.67, -16.46) * mm});
            skLineSegment(sketch, "E839", {"start": v(-13.67, -16.46) * mm, "end": v(-13.7, -16.44) * mm});
            skLineSegment(sketch, "E840", {"start": v(-13.7, -16.44) * mm, "end": v(-13.72, -16.42) * mm});
            skLineSegment(sketch, "E841", {"start": v(-13.72, -16.42) * mm, "end": v(-13.74, -16.4) * mm});
            skLineSegment(sketch, "E842", {"start": v(-13.74, -16.4) * mm, "end": v(-13.74, -16.39) * mm});
            skLineSegment(sketch, "E843", {"start": v(-13.74, -16.39) * mm, "end": v(-13.75, -16.37) * mm});
            skLineSegment(sketch, "E844", {"start": v(-13.75, -16.37) * mm, "end": v(-13.76, -16.36) * mm});
            skLineSegment(sketch, "E845", {"start": v(-13.76, -16.36) * mm, "end": v(-13.76, -16.34) * mm});
            skLineSegment(sketch, "E846", {"start": v(-13.76, -16.34) * mm, "end": v(-13.77, -16.33) * mm});
            skLineSegment(sketch, "E847", {"start": v(-13.77, -16.33) * mm, "end": v(-13.77, -16.31) * mm});
            skLineSegment(sketch, "E848", {"start": v(-13.77, -16.31) * mm, "end": v(-13.78, -16.3) * mm});
            skLineSegment(sketch, "E849", {"start": v(-13.78, -16.3) * mm, "end": v(-13.8, -15.27) * mm});
            skFitSpline(sketch, "E850", {"points": [v(-16.09, 0.4) * mm, v(-16.48, 0.53) * mm, v(-16.87, 0.42) * mm], "startDerivative": vector(-0.77, 0.4) * mm, "endDerivative": vector(-0.8, -0.36) * mm});
            skFitSpline(sketch, "E851", {"points": [v(-9.68, -1.66) * mm, v(-8.41, -1.95) * mm, v(-8.04, -3.41) * mm], "startDerivative": vector(3.1, -0.07) * mm, "endDerivative": vector(0.22, -3.4) * mm});
            skLineSegment(sketch, "E852", {"start": v(-8.04, -3.41) * mm, "end": v(-8.04, -3.57) * mm});
            skLineSegment(sketch, "E853", {"start": v(-16.09, 0.4) * mm, "end": v(-15.75, 0.24) * mm});
            skLineSegment(sketch, "E854", {"start": v(-17.01, 0.36) * mm, "end": v(-16.87, 0.42) * mm});
            skLineSegment(sketch, "E855", {"start": v(-9.68, -1.66) * mm, "end": v(-9.7, 0.57) * mm});
            skLineSegment(sketch, "E856", {"start": v(-13.9, -1.75) * mm, "end": v(-16.26, -0.55) * mm});
            skFitSpline(sketch, "E857", {"points": [v(-16.26, -0.55) * mm, v(-16.5, -0.47) * mm, v(-16.83, -0.6) * mm], "startDerivative": vector(-0.52, 0.27) * mm, "endDerivative": vector(-0.63, -0.37) * mm});
            skFitSpline(sketch, "E858", {"points": [v(-9.4, -3.99) * mm, v(-9.18, -4.2) * mm, v(-9.85, -4.84) * mm], "startDerivative": vector(0.88, -0.52) * mm, "endDerivative": vector(-1.57, -1.12) * mm});
            skSolve(sketch);
        }
        {
            var Q0;
            Q0=qSketchRegion(id+"F27",true);
            extrude(context, id + "F28", {"entities" : qUnion([Q0]), "depth" : 26.5 * mm});
        }
        {
            var Q0;
            Q0=qSketchRegion(id+"F27",true);
            var Q1;
            {var subQ0=sQuery(id+"F0.wireOp",EDGE,"E7.rect.top");var subQ1=sQuery(id+"F0.wireOp",EDGE,"E7.rect.right");var subQ2=sQuery(id+"F0.wireOp",EDGE,"E7.rect.left");var subQ3=sQuery(id+"F0.wireOp",EDGE,"E7.rect.bottom");var subQ4=sQuery(id+"F0.wireOp",EDGE,"E5.MirrorC");var subQ5=sQuery(id+"F0.wireOp",EDGE,"E3");var subQ6=sQuery(id+"F0.wireOp",EDGE,"E2");var subQ7=sQuery(id+"F0.wireOp",EDGE,"E1");Q1=makeQuery(id+"F28.boolean.opBoolean","SPLIT",FACE,{"disambiguationData":[TD([makeQuery(id+"F28.opExtrude","SWEPT_FACE",FACE,{"disambiguationData":[OSD([sQuery(id+"F27.wireOp",EDGE,"E123")])]})])],"derivedFrom":makeQuery(id+"F6.opShell","OFFSET_FACE",FACE,{"disambiguationData":[OSD([subQ7,subQ6,subQ5,subQ4,subQ3,subQ0,subQ2,subQ1]),TDD([makeQuery(id+"F1.opExtrude","CAP_FACE",FACE,{"disambiguationData":[OSD([subQ7,subQ6,subQ5,subQ4,subQ3,subQ0,subQ2,subQ1])],"isStart":false})])]})});}
            extrude(context, id + "F29", {"entities" : qUnion([Q0]), "operationType" : NewBodyOperationType.REMOVE, "endBound" : BoundingType.UP_TO_SURFACE, "endBoundEntityFace" : qUnion([Q1]), "depth" : 23 * mm});
        }
        {
            var Q0;
            {var subQ0=sQuery(id+"F18.wireOp",EDGE,"E66");Q0=makeQuery(id+"F18.imprint","IMPRINT",FACE,{"disambiguationData":[TD([[makeQuery(id+"F18.imprint","IMPRINT",EDGE,{"derivedFrom":subQ0}),-1.0]])]});}
            extrude(context, id + "F30", {"entities" : qUnion([Q0]), "operationType" : NewBodyOperationType.REMOVE, "oppositeDirection" : true, "depth" : 2 * mm});
        }
        {
            var Q0;
            Q0=qCreatedBy(makeId("Top.planeOp"),FACE);
            var sketch = newSketch(context, id + "F31", { "sketchPlane" : qUnion([Q0])});
            skLineSegment(sketch, "E859.bottom", {"start": v(7.48, -5.58) * mm, "end": v(13.97, -5.58) * mm});
            skLineSegment(sketch, "E859.top", {"start": v(7.48, -5.2) * mm, "end": v(13.97, -5.2) * mm});
            skLineSegment(sketch, "E860.bottom", {"start": v(6.04, -5.58) * mm, "end": v(16.8, -5.58) * mm});
            skLineSegment(sketch, "E860.top", {"start": v(6.04, -5.2) * mm, "end": v(16.8, -5.2) * mm});
            skLineSegment(sketch, "E860.left", {"start": v(6.04, -5.58) * mm, "end": v(6.04, -5.2) * mm});
            skLineSegment(sketch, "E861", {"start": v(16.8, -5.2) * mm, "end": v(18.32, -5.2) * mm});
            skLineSegment(sketch, "E862", {"start": v(18.32, -5.2) * mm, "end": v(18.32, -5.58) * mm});
            skLineSegment(sketch, "E863", {"start": v(18.32, -5.58) * mm, "end": v(16.8, -5.58) * mm});
            skSolve(sketch);
        }
        {
            var Q0;
            Q0=qSketchRegion(id+"F31",true);
            var Q1;
            {var subQ1=sQuery(id+"F2.wireOp",EDGE,"E22");var subQ3=sQuery(id+"F2.wireOp",EDGE,"E20");Q1=makeQuery(id+"F24.boolean.opBoolean","SPLIT",FACE,{"disambiguationData":[TD([makeQuery(id+"F6.opShell","OFFSET_FACE",FACE,{"disambiguationData":[OSD([sQuery(id+"F0.wireOp",EDGE,"E3")])]})])],"derivedFrom":makeQuery(id+"F6.opShell","OFFSET_FACE",FACE,{"disambiguationData":[OSD([subQ3,subQ1])]})});}
            extrude(context, id + "F32", {"entities" : qUnion([Q0]), "operationType" : NewBodyOperationType.ADD, "endBound" : BoundingType.UP_TO_SURFACE, "endBoundEntityFace" : qUnion([Q1]), "depth" : 25 * mm});
        }
        {
            var Q0;
            {var subQ0=sQuery(id+"F0.wireOp",EDGE,"E7.rect.top");var subQ1=sQuery(id+"F0.wireOp",EDGE,"E7.rect.right");var subQ2=sQuery(id+"F0.wireOp",EDGE,"E7.rect.left");var subQ3=sQuery(id+"F0.wireOp",EDGE,"E7.rect.bottom");var subQ4=sQuery(id+"F0.wireOp",EDGE,"E5.MirrorC");var subQ5=sQuery(id+"F0.wireOp",EDGE,"E3");var subQ6=sQuery(id+"F0.wireOp",EDGE,"E2");var subQ7=sQuery(id+"F0.wireOp",EDGE,"E1");Q0=makeQuery(id+"F28.boolean.opBoolean","SPLIT",FACE,{"disambiguationData":[TD([makeQuery(id+"F4.opFillet","BLEND_FACE",FACE,{"disambiguationData":[OSD([subQ0])]})])],"derivedFrom":makeQuery(id+"F1.opExtrude","CAP_FACE",FACE,{"disambiguationData":[OSD([subQ7,subQ6,subQ5,subQ4,subQ3,subQ0,subQ2,subQ1])],"isStart":false})});}
            cPlane(context, id + "F33", {"entities" : qUnion([Q0]), "cplaneType" : CPlaneType.OFFSET, "offset" : 9 * mm, "oppositeDirection" : true, "width" : 150 * mm, "height" : 150 * mm});
        }
        {
            var Q0;
            Q0=qCreatedBy(id+"F33.planeOp",FACE);
            var sketch = newSketch(context, id + "F34", { "sketchPlane" : qUnion([Q0])});
            skCircle(sketch, "E864", {"center": v(-29.86, -30.9) * mm, "radius": 1.22 * mm});
            skCircle(sketch, "E865", {"center": v(-29.84, 14.65) * mm, "radius": 1.25 * mm});
            skSolve(sketch);
        }
        {
            var Q0;
            Q0=qSketchRegion(id+"F34",true);
            var Q1;
            Q1=makeQuery(id+"F3.boolean.opBoolean","COPY",FACE,{"derivedFrom":makeQuery(id+"F3.opExtrude","SWEPT_FACE",FACE,{"disambiguationData":[OSD([sQuery(id+"F2.wireOp",EDGE,"E14")])]})});
            extrude(context, id + "F35", {"entities" : qUnion([Q0]), "operationType" : NewBodyOperationType.ADD, "endBound" : BoundingType.UP_TO_SURFACE, "endBoundEntityFace" : qUnion([Q1]), "depth" : 25 * mm});
        }
        {
            var Q0;
            {var subQ0=sQuery(id+"F0.wireOp",EDGE,"E7.rect.right");var subQ1=sQuery(id+"F0.wireOp",EDGE,"E7.rect.left");var subQ2=sQuery(id+"F0.wireOp",EDGE,"E7.rect.top");var subQ3=sQuery(id+"F0.wireOp",EDGE,"E7.rect.bottom");var subQ4=sQuery(id+"F0.wireOp",EDGE,"E5.MirrorC");var subQ5=sQuery(id+"F0.wireOp",EDGE,"E3");var subQ6=sQuery(id+"F0.wireOp",EDGE,"E2");var subQ7=sQuery(id+"F0.wireOp",EDGE,"E1");Q0=makeQuery(id+"F28.boolean.opBoolean","SPLIT",FACE,{"disambiguationData":[TD([makeQuery(id+"F4.opFillet","BLEND_FACE",FACE,{"disambiguationData":[OSD([subQ3])]})])],"derivedFrom":makeQuery(id+"F1.opExtrude","CAP_FACE",FACE,{"disambiguationData":[OSD([subQ7,subQ6,subQ5,subQ4,subQ3,subQ2,subQ1,subQ0])],"isStart":false})});}
            cPlane(context, id + "F36", {"entities" : qUnion([Q0]), "cplaneType" : CPlaneType.OFFSET, "offset" : 17.5 * mm, "oppositeDirection" : true, "width" : 150 * mm, "height" : 150 * mm});
        }
        {
            var Q0;
            Q0=qCreatedBy(id+"F36.planeOp",FACE);
            var sketch = newSketch(context, id + "F37", { "sketchPlane" : qUnion([Q0])});
            skCircle(sketch, "E866", {"center": v(8.9, 3.98) * mm, "radius": 1.26 * mm});
            skCircle(sketch, "E867", {"center": v(15.8, -30.92) * mm, "radius": 1.17 * mm});
            skSolve(sketch);
        }
        {
            var Q0;
            Q0=qSketchRegion(id+"F37",true);
            var Q1;
            {var subQ0=sQuery(id+"F2.wireOp",EDGE,"E22");var subQ1=sQuery(id+"F2.wireOp",EDGE,"E20");Q1=makeQuery(id+"F24.boolean.opBoolean","SPLIT",FACE,{"disambiguationData":[TD([makeQuery(id+"F1.opExtrude","SWEPT_FACE",FACE,{"disambiguationData":[OSD([sQuery(id+"F0.wireOp",EDGE,"E3")])]})])],"derivedFrom":makeQuery(id+"F3.boolean.opBoolean","COPY",FACE,{"derivedFrom":makeQuery(id+"F3.opExtrude","SWEPT_FACE",FACE,{"disambiguationData":[OSD([subQ1,subQ0])]})})});}
            extrude(context, id + "F38", {"entities" : qUnion([Q0]), "operationType" : NewBodyOperationType.ADD, "endBound" : BoundingType.UP_TO_SURFACE, "endBoundEntityFace" : qUnion([Q1]), "depth" : 25 * mm});
        }
        {
            var Q0;
            Q0=makeQuery(id+"F1.opExtrude","SWEPT_FACE",FACE,{"disambiguationData":[OSD([sQuery(id+"F0.wireOp",EDGE,"E7.rect.bottom")])]});
            cPlane(context, id + "F39", {"entities" : qUnion([Q0]), "cplaneType" : CPlaneType.OFFSET, "offset" : 1.8 * mm, "oppositeDirection" : true, "width" : 150 * mm, "height" : 150 * mm});
        }
        {
            var Q0;
            Q0=qCreatedBy(id+"F39.planeOp",FACE);
            var sketch = newSketch(context, id + "F40", { "sketchPlane" : qUnion([Q0])});
            skLineSegment(sketch, "E868.top", {"start": v(-5.27, 0) * mm, "end": v(12.86, 0) * mm});
            skLineSegment(sketch, "E869.right", {"start": v(12.86, 5.48) * mm, "end": v(12.86, 0) * mm});
            skLineSegment(sketch, "E870.bottom", {"start": v(12.86, 0) * mm, "end": v(-5.27, 0) * mm});
            skLineSegment(sketch, "E870.top", {"start": v(12.86, 5.48) * mm, "end": v(-5.27, 5.48) * mm});
            skLineSegment(sketch, "E870.left", {"start": v(12.86, 0) * mm, "end": v(12.86, 5.48) * mm});
            skPoint(sketch, "E871.orphan", {"position": v(14.06, 0) * mm});
            skLineSegment(sketch, "E872", {"start": v(-5.27, 5.48) * mm, "end": v(-8, 5.48) * mm});
            skLineSegment(sketch, "E873", {"start": v(-8, 5.48) * mm, "end": v(-8, 0) * mm});
            skLineSegment(sketch, "E874", {"start": v(-8, 0) * mm, "end": v(-5.27, 0) * mm});
            skSolve(sketch);
        }
        {
            var Q0;
            Q0=qSketchRegion(id+"F40",true);
            extrude(context, id + "F41", {"entities" : qUnion([Q0]), "operationType" : NewBodyOperationType.REMOVE, "depth" : 1.2 * mm});
        }
        {
            var Q0;
            Q0=qCreatedBy(makeId("Top.planeOp"),FACE);
            var sketch = newSketch(context, id + "F42", { "sketchPlane" : qUnion([Q0])});
            skLineSegment(sketch, "E875.bottom", {"start": v(-10.2, -20.34) * mm, "end": v(-23.5, -20.34) * mm});
            skLineSegment(sketch, "E875.top", {"start": v(-9.76, -20.7) * mm, "end": v(-23.91, -20.7) * mm});
            skLineSegment(sketch, "E875.left", {"start": v(-9.76, -20.34) * mm, "end": v(-9.76, -20.7) * mm});
            skLineSegment(sketch, "E876", {"start": v(-9.76, -19.58) * mm, "end": v(-9.76, 2.28) * mm});
            skLineSegment(sketch, "E877.bottom", {"start": v(-10.2, 2.28) * mm, "end": v(-23.5, 2.28) * mm});
            skLineSegment(sketch, "E877.top", {"start": v(-9.76, 2.58) * mm, "end": v(-23.91, 2.58) * mm});
            skLineSegment(sketch, "E877.left", {"start": v(-9.76, 2.28) * mm, "end": v(-9.76, 2.58) * mm});
            skLineSegment(sketch, "E877.right", {"start": v(-23.91, 2.28) * mm, "end": v(-23.91, 2.58) * mm});
            skLineSegment(sketch, "E878.bottom", {"start": v(-10.2, -10.06) * mm, "end": v(-23.5, -10.06) * mm});
            skLineSegment(sketch, "E878.top", {"start": v(-10.2, -9.35) * mm, "end": v(-23.5, -9.35) * mm});
            skLineSegment(sketch, "E878.left", {"start": v(-9.76, -10.06) * mm, "end": v(-9.76, -9.35) * mm});
            skLineSegment(sketch, "E878.right", {"start": v(-25.9, -10.06) * mm, "end": v(-25.9, -9.35) * mm});
            skLineSegment(sketch, "E879", {"start": v(-10.2, -19.58) * mm, "end": v(-10.2, -10.06) * mm});
            skLineSegment(sketch, "E880.bottom", {"start": v(-23.91, 2.58) * mm, "end": v(-23.5, 2.58) * mm});
            skLineSegment(sketch, "E880.top", {"start": v(-23.91, -20.7) * mm, "end": v(-23.5, -20.7) * mm});
            skLineSegment(sketch, "E880.left", {"start": v(-23.91, 2.58) * mm, "end": v(-23.91, 2.28) * mm});
            skLineSegment(sketch, "E880.right", {"start": v(-23.5, 1.67) * mm, "end": v(-23.5, -9.35) * mm});
            skLineSegment(sketch, "E881.trimOffspring", {"start": v(-10.2, -9.35) * mm, "end": v(-10.2, 2.28) * mm});
            skLineSegment(sketch, "E882.trimOffspring", {"start": v(-23.91, -10.06) * mm, "end": v(-25.9, -10.06) * mm});
            skLineSegment(sketch, "E883.trimOffspring", {"start": v(-23.91, -10.06) * mm, "end": v(-23.91, -20.7) * mm});
            skLineSegment(sketch, "E884.trimOffspring", {"start": v(-23.5, -10.06) * mm, "end": v(-23.5, -20.34) * mm});
            skLineSegment(sketch, "E885.trimOffspring", {"start": v(-23.91, -9.35) * mm, "end": v(-25.9, -9.35) * mm});
            skLineSegment(sketch, "E886", {"start": v(-10.2, -19.58) * mm, "end": v(-9.76, -19.58) * mm});
            skLineSegment(sketch, "E887", {"start": v(-10.2, -20.34) * mm, "end": v(-9.76, -20.34) * mm});
            skLineSegment(sketch, "E888", {"start": v(-23.5, 2.28) * mm, "end": v(-23.91, 2.28) * mm});
            skLineSegment(sketch, "E889", {"start": v(-23.5, 1.67) * mm, "end": v(-23.91, 1.67) * mm});
            skLineSegment(sketch, "E890.trimOffspring", {"start": v(-23.91, 1.67) * mm, "end": v(-23.91, -9.35) * mm});
            skSolve(sketch);
        }
        {
            var Q0;
            Q0=qSketchRegion(id+"F42",true);
            var Q1;
            {var subQ0=sQuery(id+"F27.wireOp",EDGE,"E849");var subQ1=sQuery(id+"F27.wireOp",EDGE,"E848");var subQ2=sQuery(id+"F27.wireOp",EDGE,"E847");var subQ3=sQuery(id+"F27.wireOp",EDGE,"E846");var subQ4=sQuery(id+"F27.wireOp",EDGE,"E845");var subQ5=sQuery(id+"F27.wireOp",EDGE,"E844");var subQ6=sQuery(id+"F27.wireOp",EDGE,"E843");var subQ7=sQuery(id+"F27.wireOp",EDGE,"E842");var subQ8=sQuery(id+"F27.wireOp",EDGE,"E841");var subQ9=sQuery(id+"F27.wireOp",EDGE,"E840");var subQ10=sQuery(id+"F27.wireOp",EDGE,"E839");var subQ11=sQuery(id+"F27.wireOp",EDGE,"E838");var subQ12=sQuery(id+"F27.wireOp",EDGE,"E837");var subQ13=sQuery(id+"F27.wireOp",EDGE,"E836");var subQ14=sQuery(id+"F27.wireOp",EDGE,"E835");var subQ15=sQuery(id+"F27.wireOp",EDGE,"E834");var subQ16=sQuery(id+"F27.wireOp",EDGE,"E833");var subQ17=sQuery(id+"F27.wireOp",EDGE,"E832");var subQ18=sQuery(id+"F27.wireOp",EDGE,"E831");var subQ19=sQuery(id+"F27.wireOp",EDGE,"E830");var subQ20=sQuery(id+"F27.wireOp",EDGE,"E829");var subQ21=sQuery(id+"F27.wireOp",EDGE,"E828");var subQ22=sQuery(id+"F27.wireOp",EDGE,"E827");var subQ23=sQuery(id+"F27.wireOp",EDGE,"E826");var subQ24=sQuery(id+"F27.wireOp",EDGE,"E825");var subQ25=sQuery(id+"F27.wireOp",EDGE,"E824");var subQ26=sQuery(id+"F27.wireOp",EDGE,"E823");var subQ27=sQuery(id+"F27.wireOp",EDGE,"E822");var subQ28=sQuery(id+"F27.wireOp",EDGE,"E821");var subQ29=sQuery(id+"F27.wireOp",EDGE,"E820");var subQ30=sQuery(id+"F27.wireOp",EDGE,"E819");var subQ31=sQuery(id+"F27.wireOp",EDGE,"E818");var subQ32=sQuery(id+"F27.wireOp",EDGE,"E817");var subQ33=sQuery(id+"F27.wireOp",EDGE,"E816");var subQ34=sQuery(id+"F27.wireOp",EDGE,"E815");var subQ35=sQuery(id+"F27.wireOp",EDGE,"E814");var subQ36=sQuery(id+"F27.wireOp",EDGE,"E813");var subQ37=sQuery(id+"F27.wireOp",EDGE,"E812");var subQ38=sQuery(id+"F27.wireOp",EDGE,"E811");var subQ39=sQuery(id+"F27.wireOp",EDGE,"E810");var subQ40=sQuery(id+"F27.wireOp",EDGE,"E809");var subQ41=sQuery(id+"F27.wireOp",EDGE,"E808");var subQ42=sQuery(id+"F27.wireOp",EDGE,"E807");var subQ43=sQuery(id+"F27.wireOp",EDGE,"E806");var subQ44=sQuery(id+"F27.wireOp",EDGE,"E805");var subQ45=sQuery(id+"F27.wireOp",EDGE,"E804");var subQ46=sQuery(id+"F27.wireOp",EDGE,"E803");var subQ47=sQuery(id+"F27.wireOp",EDGE,"E802");var subQ48=sQuery(id+"F27.wireOp",EDGE,"E801");var subQ49=sQuery(id+"F27.wireOp",EDGE,"E800");var subQ50=sQuery(id+"F27.wireOp",EDGE,"E799");var subQ51=sQuery(id+"F27.wireOp",EDGE,"E798");var subQ52=sQuery(id+"F27.wireOp",EDGE,"E797");var subQ53=sQuery(id+"F27.wireOp",EDGE,"E796");var subQ54=sQuery(id+"F27.wireOp",EDGE,"E795");var subQ55=sQuery(id+"F27.wireOp",EDGE,"E794");var subQ56=sQuery(id+"F27.wireOp",EDGE,"E793");var subQ57=sQuery(id+"F27.wireOp",EDGE,"E792");var subQ58=sQuery(id+"F27.wireOp",EDGE,"E791");var subQ59=sQuery(id+"F27.wireOp",EDGE,"E790");var subQ60=sQuery(id+"F27.wireOp",EDGE,"E789");var subQ61=sQuery(id+"F27.wireOp",EDGE,"E788");var subQ62=sQuery(id+"F27.wireOp",EDGE,"E787");var subQ63=sQuery(id+"F27.wireOp",EDGE,"E786");var subQ64=sQuery(id+"F27.wireOp",EDGE,"E785");var subQ65=sQuery(id+"F27.wireOp",EDGE,"E784");var subQ66=sQuery(id+"F27.wireOp",EDGE,"E783");var subQ67=sQuery(id+"F27.wireOp",EDGE,"E782");var subQ68=sQuery(id+"F27.wireOp",EDGE,"E781");var subQ69=sQuery(id+"F27.wireOp",EDGE,"E780");var subQ70=sQuery(id+"F27.wireOp",EDGE,"E779");var subQ71=sQuery(id+"F27.wireOp",EDGE,"E778");var subQ72=sQuery(id+"F27.wireOp",EDGE,"E777");var subQ73=sQuery(id+"F27.wireOp",EDGE,"E776");var subQ74=sQuery(id+"F27.wireOp",EDGE,"E775");var subQ75=sQuery(id+"F27.wireOp",EDGE,"E774");var subQ76=sQuery(id+"F27.wireOp",EDGE,"E773");var subQ77=sQuery(id+"F27.wireOp",EDGE,"E772");var subQ78=sQuery(id+"F27.wireOp",EDGE,"E771");var subQ79=sQuery(id+"F27.wireOp",EDGE,"E770");var subQ80=sQuery(id+"F27.wireOp",EDGE,"E769");var subQ81=sQuery(id+"F27.wireOp",EDGE,"E768");var subQ82=sQuery(id+"F27.wireOp",EDGE,"E767");var subQ83=sQuery(id+"F27.wireOp",EDGE,"E766");var subQ84=sQuery(id+"F27.wireOp",EDGE,"E765");var subQ85=sQuery(id+"F27.wireOp",EDGE,"E764");var subQ86=sQuery(id+"F27.wireOp",EDGE,"E763");var subQ87=sQuery(id+"F27.wireOp",EDGE,"E762");var subQ88=sQuery(id+"F27.wireOp",EDGE,"E761");var subQ89=sQuery(id+"F27.wireOp",EDGE,"E760");var subQ90=sQuery(id+"F27.wireOp",EDGE,"E759");var subQ91=sQuery(id+"F27.wireOp",EDGE,"E758");var subQ92=sQuery(id+"F27.wireOp",EDGE,"E757");var subQ93=sQuery(id+"F27.wireOp",EDGE,"E756");var subQ94=sQuery(id+"F27.wireOp",EDGE,"E755");var subQ95=sQuery(id+"F27.wireOp",EDGE,"E754");var subQ96=sQuery(id+"F27.wireOp",EDGE,"E753");var subQ97=sQuery(id+"F27.wireOp",EDGE,"E752");var subQ98=sQuery(id+"F27.wireOp",EDGE,"E751");var subQ99=sQuery(id+"F27.wireOp",EDGE,"E750");var subQ100=sQuery(id+"F27.wireOp",EDGE,"E749");var subQ101=sQuery(id+"F27.wireOp",EDGE,"E748");var subQ102=sQuery(id+"F27.wireOp",EDGE,"E747");var subQ103=sQuery(id+"F27.wireOp",EDGE,"E746");var subQ104=sQuery(id+"F27.wireOp",EDGE,"E745");var subQ105=sQuery(id+"F27.wireOp",EDGE,"E744");var subQ106=sQuery(id+"F27.wireOp",EDGE,"E743");var subQ107=sQuery(id+"F27.wireOp",EDGE,"E742");var subQ108=sQuery(id+"F27.wireOp",EDGE,"E741");var subQ109=sQuery(id+"F27.wireOp",EDGE,"E740");var subQ110=sQuery(id+"F27.wireOp",EDGE,"E739");var subQ111=sQuery(id+"F27.wireOp",EDGE,"E738");var subQ112=sQuery(id+"F27.wireOp",EDGE,"E737");var subQ113=sQuery(id+"F27.wireOp",EDGE,"E736");var subQ114=sQuery(id+"F27.wireOp",EDGE,"E735");var subQ115=sQuery(id+"F27.wireOp",EDGE,"E734");var subQ116=sQuery(id+"F27.wireOp",EDGE,"E733");var subQ117=sQuery(id+"F27.wireOp",EDGE,"E732");var subQ118=sQuery(id+"F27.wireOp",EDGE,"E731");var subQ119=sQuery(id+"F27.wireOp",EDGE,"E730");var subQ120=sQuery(id+"F27.wireOp",EDGE,"E729");var subQ121=sQuery(id+"F27.wireOp",EDGE,"E728");var subQ122=sQuery(id+"F27.wireOp",EDGE,"E727");var subQ123=sQuery(id+"F27.wireOp",EDGE,"E726");var subQ124=sQuery(id+"F27.wireOp",EDGE,"E725");var subQ125=sQuery(id+"F27.wireOp",EDGE,"E724");var subQ126=sQuery(id+"F27.wireOp",EDGE,"E723");var subQ127=sQuery(id+"F27.wireOp",EDGE,"E722");var subQ128=sQuery(id+"F27.wireOp",EDGE,"E721");var subQ129=sQuery(id+"F27.wireOp",EDGE,"E720");var subQ130=sQuery(id+"F27.wireOp",EDGE,"E719");var subQ131=sQuery(id+"F27.wireOp",EDGE,"E718");var subQ132=sQuery(id+"F27.wireOp",EDGE,"E717");var subQ133=sQuery(id+"F27.wireOp",EDGE,"E716");var subQ134=sQuery(id+"F27.wireOp",EDGE,"E715");var subQ135=sQuery(id+"F27.wireOp",EDGE,"E714");var subQ136=sQuery(id+"F27.wireOp",EDGE,"E713");var subQ137=sQuery(id+"F27.wireOp",EDGE,"E712");var subQ138=sQuery(id+"F27.wireOp",EDGE,"E711");var subQ139=sQuery(id+"F27.wireOp",EDGE,"E710");var subQ140=sQuery(id+"F27.wireOp",EDGE,"E709");var subQ141=sQuery(id+"F27.wireOp",EDGE,"E708");var subQ142=sQuery(id+"F27.wireOp",EDGE,"E707");var subQ143=sQuery(id+"F27.wireOp",EDGE,"E706");var subQ144=sQuery(id+"F27.wireOp",EDGE,"E705");var subQ145=sQuery(id+"F27.wireOp",EDGE,"E704");var subQ146=sQuery(id+"F27.wireOp",EDGE,"E703");var subQ147=sQuery(id+"F27.wireOp",EDGE,"E702");var subQ148=sQuery(id+"F27.wireOp",EDGE,"E701");var subQ149=sQuery(id+"F27.wireOp",EDGE,"E700");var subQ150=sQuery(id+"F27.wireOp",EDGE,"E699");var subQ151=sQuery(id+"F27.wireOp",EDGE,"E698");var subQ152=sQuery(id+"F27.wireOp",EDGE,"E697");var subQ153=sQuery(id+"F27.wireOp",EDGE,"E696");var subQ154=sQuery(id+"F27.wireOp",EDGE,"E695");var subQ155=sQuery(id+"F27.wireOp",EDGE,"E694");var subQ156=sQuery(id+"F27.wireOp",EDGE,"E693");var subQ157=sQuery(id+"F27.wireOp",EDGE,"E692");var subQ158=sQuery(id+"F27.wireOp",EDGE,"E691");var subQ159=sQuery(id+"F27.wireOp",EDGE,"E690");var subQ160=sQuery(id+"F27.wireOp",EDGE,"E689");var subQ161=sQuery(id+"F27.wireOp",EDGE,"E688");var subQ162=sQuery(id+"F27.wireOp",EDGE,"E687");var subQ163=sQuery(id+"F27.wireOp",EDGE,"E686");var subQ164=sQuery(id+"F27.wireOp",EDGE,"E685");var subQ165=sQuery(id+"F27.wireOp",EDGE,"E684");var subQ166=sQuery(id+"F27.wireOp",EDGE,"E683");var subQ167=sQuery(id+"F27.wireOp",EDGE,"E682");var subQ168=sQuery(id+"F27.wireOp",EDGE,"E681");var subQ169=sQuery(id+"F27.wireOp",EDGE,"E680");var subQ170=sQuery(id+"F27.wireOp",EDGE,"E679");var subQ171=sQuery(id+"F27.wireOp",EDGE,"E678");var subQ172=sQuery(id+"F27.wireOp",EDGE,"E677");var subQ173=sQuery(id+"F27.wireOp",EDGE,"E676");var subQ174=sQuery(id+"F27.wireOp",EDGE,"E675");var subQ175=sQuery(id+"F27.wireOp",EDGE,"E674");var subQ176=sQuery(id+"F27.wireOp",EDGE,"E673");var subQ177=sQuery(id+"F27.wireOp",EDGE,"E672");var subQ178=sQuery(id+"F27.wireOp",EDGE,"E671");var subQ179=sQuery(id+"F27.wireOp",EDGE,"E670");var subQ180=sQuery(id+"F27.wireOp",EDGE,"E669");var subQ181=sQuery(id+"F27.wireOp",EDGE,"E668");var subQ182=sQuery(id+"F27.wireOp",EDGE,"E667");var subQ183=sQuery(id+"F27.wireOp",EDGE,"E666");var subQ184=sQuery(id+"F27.wireOp",EDGE,"E665");var subQ185=sQuery(id+"F27.wireOp",EDGE,"E664");var subQ186=sQuery(id+"F27.wireOp",EDGE,"E663");var subQ187=sQuery(id+"F27.wireOp",EDGE,"E662");var subQ188=sQuery(id+"F27.wireOp",EDGE,"E661");var subQ189=sQuery(id+"F27.wireOp",EDGE,"E660");var subQ190=sQuery(id+"F27.wireOp",EDGE,"E659");var subQ191=sQuery(id+"F27.wireOp",EDGE,"E658");var subQ192=sQuery(id+"F27.wireOp",EDGE,"E657");var subQ193=sQuery(id+"F27.wireOp",EDGE,"E656");var subQ194=sQuery(id+"F27.wireOp",EDGE,"E655");var subQ195=sQuery(id+"F27.wireOp",EDGE,"E858");var subQ196=sQuery(id+"F27.wireOp",EDGE,"E857");var subQ197=sQuery(id+"F27.wireOp",EDGE,"E856");var subQ198=sQuery(id+"F27.wireOp",EDGE,"E854");var subQ199=sQuery(id+"F27.wireOp",EDGE,"E853");var subQ200=sQuery(id+"F27.wireOp",EDGE,"E850");var subQ201=sQuery(id+"F27.wireOp",EDGE,"E325");var subQ202=sQuery(id+"F27.wireOp",EDGE,"E324");var subQ203=sQuery(id+"F27.wireOp",EDGE,"E323");var subQ204=sQuery(id+"F27.wireOp",EDGE,"E321");var subQ205=sQuery(id+"F27.wireOp",EDGE,"E320");var subQ206=sQuery(id+"F27.wireOp",EDGE,"E319");var subQ207=sQuery(id+"F27.wireOp",EDGE,"E318");var subQ208=sQuery(id+"F27.wireOp",EDGE,"E317");var subQ209=sQuery(id+"F27.wireOp",EDGE,"E316");var subQ210=sQuery(id+"F27.wireOp",EDGE,"E315");var subQ211=sQuery(id+"F27.wireOp",EDGE,"E314");var subQ212=sQuery(id+"F27.wireOp",EDGE,"E313");var subQ213=sQuery(id+"F27.wireOp",EDGE,"E312");var subQ214=sQuery(id+"F27.wireOp",EDGE,"E311");var subQ215=sQuery(id+"F27.wireOp",EDGE,"E310");var subQ216=sQuery(id+"F27.wireOp",EDGE,"E309");var subQ217=sQuery(id+"F27.wireOp",EDGE,"E308");var subQ218=sQuery(id+"F27.wireOp",EDGE,"E307");var subQ219=sQuery(id+"F27.wireOp",EDGE,"E306");var subQ220=sQuery(id+"F27.wireOp",EDGE,"E305");var subQ221=sQuery(id+"F27.wireOp",EDGE,"E304");var subQ222=sQuery(id+"F27.wireOp",EDGE,"E303");var subQ223=sQuery(id+"F27.wireOp",EDGE,"E302");var subQ224=sQuery(id+"F27.wireOp",EDGE,"E301");var subQ225=sQuery(id+"F27.wireOp",EDGE,"E300");var subQ226=sQuery(id+"F27.wireOp",EDGE,"E299");var subQ227=sQuery(id+"F27.wireOp",EDGE,"E298");var subQ228=sQuery(id+"F27.wireOp",EDGE,"E297");var subQ229=sQuery(id+"F27.wireOp",EDGE,"E296");var subQ230=sQuery(id+"F27.wireOp",EDGE,"E295");var subQ231=sQuery(id+"F27.wireOp",EDGE,"E294");var subQ232=sQuery(id+"F27.wireOp",EDGE,"E293");var subQ233=sQuery(id+"F27.wireOp",EDGE,"E292");var subQ234=sQuery(id+"F27.wireOp",EDGE,"E291");var subQ235=sQuery(id+"F27.wireOp",EDGE,"E290");var subQ236=sQuery(id+"F27.wireOp",EDGE,"E289");var subQ237=sQuery(id+"F27.wireOp",EDGE,"E288");var subQ238=sQuery(id+"F27.wireOp",EDGE,"E287");var subQ239=sQuery(id+"F27.wireOp",EDGE,"E286");var subQ240=sQuery(id+"F27.wireOp",EDGE,"E285");var subQ241=sQuery(id+"F27.wireOp",EDGE,"E284");var subQ242=sQuery(id+"F27.wireOp",EDGE,"E283");var subQ243=sQuery(id+"F27.wireOp",EDGE,"E282");var subQ244=sQuery(id+"F27.wireOp",EDGE,"E281");var subQ245=sQuery(id+"F27.wireOp",EDGE,"E280");var subQ246=sQuery(id+"F27.wireOp",EDGE,"E279");var subQ247=sQuery(id+"F27.wireOp",EDGE,"E278");var subQ248=sQuery(id+"F27.wireOp",EDGE,"E277");var subQ249=sQuery(id+"F27.wireOp",EDGE,"E276");var subQ250=sQuery(id+"F27.wireOp",EDGE,"E275");var subQ251=sQuery(id+"F27.wireOp",EDGE,"E274");var subQ252=sQuery(id+"F27.wireOp",EDGE,"E273");var subQ253=sQuery(id+"F27.wireOp",EDGE,"E272");var subQ254=sQuery(id+"F27.wireOp",EDGE,"E271");var subQ255=sQuery(id+"F27.wireOp",EDGE,"E270");var subQ256=sQuery(id+"F27.wireOp",EDGE,"E269");var subQ257=sQuery(id+"F27.wireOp",EDGE,"E268");var subQ258=sQuery(id+"F27.wireOp",EDGE,"E267");var subQ259=sQuery(id+"F27.wireOp",EDGE,"E266");var subQ260=sQuery(id+"F27.wireOp",EDGE,"E265");var subQ261=sQuery(id+"F27.wireOp",EDGE,"E264");var subQ262=sQuery(id+"F27.wireOp",EDGE,"E263");var subQ263=sQuery(id+"F27.wireOp",EDGE,"E262");var subQ264=sQuery(id+"F27.wireOp",EDGE,"E261");var subQ265=sQuery(id+"F27.wireOp",EDGE,"E260");var subQ266=sQuery(id+"F27.wireOp",EDGE,"E259");var subQ267=sQuery(id+"F27.wireOp",EDGE,"E258");var subQ268=sQuery(id+"F27.wireOp",EDGE,"E257");var subQ269=sQuery(id+"F27.wireOp",EDGE,"E256");var subQ270=sQuery(id+"F27.wireOp",EDGE,"E255");var subQ271=sQuery(id+"F27.wireOp",EDGE,"E254");var subQ272=sQuery(id+"F27.wireOp",EDGE,"E253");var subQ273=sQuery(id+"F27.wireOp",EDGE,"E252");var subQ274=sQuery(id+"F27.wireOp",EDGE,"E251");var subQ275=sQuery(id+"F27.wireOp",EDGE,"E250");var subQ276=sQuery(id+"F27.wireOp",EDGE,"E249");var subQ277=sQuery(id+"F27.wireOp",EDGE,"E248");var subQ278=sQuery(id+"F27.wireOp",EDGE,"E247");var subQ279=sQuery(id+"F27.wireOp",EDGE,"E246");var subQ280=sQuery(id+"F27.wireOp",EDGE,"E245");var subQ281=sQuery(id+"F27.wireOp",EDGE,"E244");var subQ282=sQuery(id+"F27.wireOp",EDGE,"E243");var subQ283=sQuery(id+"F27.wireOp",EDGE,"E242");var subQ284=sQuery(id+"F27.wireOp",EDGE,"E241");var subQ285=sQuery(id+"F27.wireOp",EDGE,"E182");var subQ286=sQuery(id+"F27.wireOp",EDGE,"E181");var subQ287=sQuery(id+"F27.wireOp",EDGE,"E180");var subQ288=sQuery(id+"F27.wireOp",EDGE,"E179");var subQ289=sQuery(id+"F27.wireOp",EDGE,"E178");var subQ290=sQuery(id+"F27.wireOp",EDGE,"E177");var subQ291=sQuery(id+"F27.wireOp",EDGE,"E176");var subQ292=sQuery(id+"F27.wireOp",EDGE,"E175");var subQ293=sQuery(id+"F27.wireOp",EDGE,"E174");var subQ294=sQuery(id+"F27.wireOp",EDGE,"E173");var subQ295=sQuery(id+"F27.wireOp",EDGE,"E172");var subQ296=sQuery(id+"F27.wireOp",EDGE,"E171");var subQ297=sQuery(id+"F27.wireOp",EDGE,"E170");var subQ298=sQuery(id+"F27.wireOp",EDGE,"E123");var subQ299=sQuery(id+"F0.wireOp",EDGE,"E7.rect.bottom");var subQ302=sQuery(id+"F0.wireOp",EDGE,"E7.rect.right");var subQ303=sQuery(id+"F0.wireOp",EDGE,"E7.rect.left");var subQ304=sQuery(id+"F0.wireOp",EDGE,"E7.rect.top");var subQ305=sQuery(id+"F0.wireOp",EDGE,"E5.MirrorC");var subQ306=sQuery(id+"F0.wireOp",EDGE,"E3");var subQ307=sQuery(id+"F0.wireOp",EDGE,"E2");var subQ308=sQuery(id+"F0.wireOp",EDGE,"E1");var subQ309=makeQuery(id+"F1.opExtrude","CAP_FACE",FACE,{"disambiguationData":[OSD([subQ308,subQ307,subQ306,subQ305,subQ299,subQ304,subQ303,subQ302])],"isStart":false});var subQ312=makeQuery(id+"F6.opShell","OFFSET_FACE",FACE,{"disambiguationData":[OSD([subQ308,subQ307,subQ306,subQ305,subQ299,subQ304,subQ303,subQ302]),TDD([subQ309])]});Q1=makeQuery(id+"F29.boolean.opBoolean","MERGE",FACE,{"derivedFrom":[makeQuery(id+"F28.boolean.opBoolean","SPLIT",FACE,{"disambiguationData":[TD([makeQuery(id+"F28.opExtrude","SWEPT_FACE",FACE,{"disambiguationData":[OSD([subQ298])]})])],"derivedFrom":subQ312}),makeQuery(id+"F28.boolean.opBoolean","SPLIT",FACE,{"disambiguationData":[TD([makeQuery(id+"F28.opExtrude","SWEPT_FACE",FACE,{"disambiguationData":[OSD([subQ262])]})])],"derivedFrom":subQ312}),makeQuery(id+"F28.boolean.opBoolean","SPLIT",FACE,{"disambiguationData":[TD([makeQuery(id+"F28.opExtrude","SWEPT_FACE",FACE,{"disambiguationData":[OSD([subQ297])]})])],"derivedFrom":subQ312}),makeQuery(id+"F29.opExtrude","CAP_FACE",FACE,{"disambiguationData":[OSD([subQ298,sQuery(id+"F27.wireOp",EDGE,"E124"),sQuery(id+"F27.wireOp",EDGE,"E125"),sQuery(id+"F27.wireOp",EDGE,"E126"),sQuery(id+"F27.wireOp",EDGE,"E127"),sQuery(id+"F27.wireOp",EDGE,"E128"),sQuery(id+"F27.wireOp",EDGE,"E129"),sQuery(id+"F27.wireOp",EDGE,"E130"),sQuery(id+"F27.wireOp",EDGE,"E131"),sQuery(id+"F27.wireOp",EDGE,"E132"),sQuery(id+"F27.wireOp",EDGE,"E133"),sQuery(id+"F27.wireOp",EDGE,"E134"),sQuery(id+"F27.wireOp",EDGE,"E135"),sQuery(id+"F27.wireOp",EDGE,"E136"),sQuery(id+"F27.wireOp",EDGE,"E137"),sQuery(id+"F27.wireOp",EDGE,"E138"),sQuery(id+"F27.wireOp",EDGE,"E139"),sQuery(id+"F27.wireOp",EDGE,"E140"),sQuery(id+"F27.wireOp",EDGE,"E141"),sQuery(id+"F27.wireOp",EDGE,"E142"),sQuery(id+"F27.wireOp",EDGE,"E143"),sQuery(id+"F27.wireOp",EDGE,"E144"),sQuery(id+"F27.wireOp",EDGE,"E145"),sQuery(id+"F27.wireOp",EDGE,"E146"),sQuery(id+"F27.wireOp",EDGE,"E147"),sQuery(id+"F27.wireOp",EDGE,"E148"),sQuery(id+"F27.wireOp",EDGE,"E149"),sQuery(id+"F27.wireOp",EDGE,"E150"),sQuery(id+"F27.wireOp",EDGE,"E151"),sQuery(id+"F27.wireOp",EDGE,"E152"),sQuery(id+"F27.wireOp",EDGE,"E153"),sQuery(id+"F27.wireOp",EDGE,"E154"),sQuery(id+"F27.wireOp",EDGE,"E155"),sQuery(id+"F27.wireOp",EDGE,"E156"),sQuery(id+"F27.wireOp",EDGE,"E157"),sQuery(id+"F27.wireOp",EDGE,"E158"),sQuery(id+"F27.wireOp",EDGE,"E159"),sQuery(id+"F27.wireOp",EDGE,"E160"),sQuery(id+"F27.wireOp",EDGE,"E161"),sQuery(id+"F27.wireOp",EDGE,"E162"),sQuery(id+"F27.wireOp",EDGE,"E163"),sQuery(id+"F27.wireOp",EDGE,"E164"),sQuery(id+"F27.wireOp",EDGE,"E165"),sQuery(id+"F27.wireOp",EDGE,"E166"),sQuery(id+"F27.wireOp",EDGE,"E167"),sQuery(id+"F27.wireOp",EDGE,"E168"),sQuery(id+"F27.wireOp",EDGE,"E169"),subQ297,subQ296,subQ295,subQ294,subQ293,subQ292,subQ291,subQ290,subQ289,subQ288,subQ287,subQ286,subQ285,sQuery(id+"F27.wireOp",EDGE,"E183"),sQuery(id+"F27.wireOp",EDGE,"E184"),sQuery(id+"F27.wireOp",EDGE,"E185"),sQuery(id+"F27.wireOp",EDGE,"E186"),sQuery(id+"F27.wireOp",EDGE,"E187"),sQuery(id+"F27.wireOp",EDGE,"E188"),sQuery(id+"F27.wireOp",EDGE,"E189"),sQuery(id+"F27.wireOp",EDGE,"E190"),sQuery(id+"F27.wireOp",EDGE,"E191"),sQuery(id+"F27.wireOp",EDGE,"E192"),sQuery(id+"F27.wireOp",EDGE,"E193"),sQuery(id+"F27.wireOp",EDGE,"E194"),sQuery(id+"F27.wireOp",EDGE,"E195"),sQuery(id+"F27.wireOp",EDGE,"E196"),sQuery(id+"F27.wireOp",EDGE,"E197"),sQuery(id+"F27.wireOp",EDGE,"E198"),sQuery(id+"F27.wireOp",EDGE,"E199"),sQuery(id+"F27.wireOp",EDGE,"E200"),sQuery(id+"F27.wireOp",EDGE,"E201"),sQuery(id+"F27.wireOp",EDGE,"E202"),sQuery(id+"F27.wireOp",EDGE,"E203"),sQuery(id+"F27.wireOp",EDGE,"E204"),sQuery(id+"F27.wireOp",EDGE,"E205"),sQuery(id+"F27.wireOp",EDGE,"E206"),sQuery(id+"F27.wireOp",EDGE,"E207"),sQuery(id+"F27.wireOp",EDGE,"E208"),sQuery(id+"F27.wireOp",EDGE,"E209"),sQuery(id+"F27.wireOp",EDGE,"E210"),sQuery(id+"F27.wireOp",EDGE,"E211"),sQuery(id+"F27.wireOp",EDGE,"E212"),sQuery(id+"F27.wireOp",EDGE,"E213"),sQuery(id+"F27.wireOp",EDGE,"E214"),sQuery(id+"F27.wireOp",EDGE,"E215"),sQuery(id+"F27.wireOp",EDGE,"E216"),sQuery(id+"F27.wireOp",EDGE,"E217"),sQuery(id+"F27.wireOp",EDGE,"E218"),sQuery(id+"F27.wireOp",EDGE,"E219"),sQuery(id+"F27.wireOp",EDGE,"E220"),sQuery(id+"F27.wireOp",EDGE,"E221"),sQuery(id+"F27.wireOp",EDGE,"E222"),sQuery(id+"F27.wireOp",EDGE,"E223"),sQuery(id+"F27.wireOp",EDGE,"E224"),sQuery(id+"F27.wireOp",EDGE,"E225"),sQuery(id+"F27.wireOp",EDGE,"E226"),sQuery(id+"F27.wireOp",EDGE,"E227"),sQuery(id+"F27.wireOp",EDGE,"E228"),sQuery(id+"F27.wireOp",EDGE,"E229"),sQuery(id+"F27.wireOp",EDGE,"E230"),sQuery(id+"F27.wireOp",EDGE,"E231"),sQuery(id+"F27.wireOp",EDGE,"E232"),sQuery(id+"F27.wireOp",EDGE,"E233"),sQuery(id+"F27.wireOp",EDGE,"E234"),sQuery(id+"F27.wireOp",EDGE,"E235"),sQuery(id+"F27.wireOp",EDGE,"E236"),sQuery(id+"F27.wireOp",EDGE,"E237"),sQuery(id+"F27.wireOp",EDGE,"E238"),sQuery(id+"F27.wireOp",EDGE,"E239"),sQuery(id+"F27.wireOp",EDGE,"E240"),subQ284,subQ283,subQ282,subQ281,subQ280,subQ279,subQ278,subQ277,subQ276,subQ275,subQ274,subQ273,subQ272,subQ271,subQ270,subQ269,subQ268,subQ267,subQ266,subQ265,subQ264,subQ263,subQ262,subQ261,subQ260,subQ259,subQ258,subQ257,subQ256,subQ255,subQ254,subQ253,subQ252,subQ251,subQ250,subQ249,subQ248,subQ247,subQ246,subQ245,subQ244,subQ243,subQ242,subQ241,subQ240,subQ239,subQ238,subQ237,subQ236,subQ235,subQ234,subQ233,subQ232,subQ231,subQ230,subQ229,subQ228,subQ227,subQ226,subQ225,subQ224,subQ223,subQ222,subQ221,subQ220,subQ219,subQ218,subQ217,subQ216,subQ215,subQ214,subQ213,subQ212,subQ211,subQ210,subQ209,subQ208,subQ207,subQ206,subQ205,subQ204,sQuery(id+"F27.wireOp",EDGE,"E322"),subQ203,subQ202,subQ201,subQ200,sQuery(id+"F27.wireOp",EDGE,"E851"),sQuery(id+"F27.wireOp",EDGE,"E852"),subQ199,subQ198,sQuery(id+"F27.wireOp",EDGE,"E855"),subQ197,subQ196,subQ195])],"isStart":false}),makeQuery(id+"F29.opExtrude","CAP_FACE",FACE,{"disambiguationData":[OSD([subQ194,subQ193,subQ192,subQ191,subQ190,subQ189,subQ188,subQ187,subQ186,subQ185,subQ184,subQ183,subQ182,subQ181,subQ180,subQ179,subQ178,subQ177,subQ176,subQ175,subQ174,subQ173,subQ172,subQ171,subQ170,subQ169,subQ168,subQ167,subQ166,subQ165,subQ164,subQ163,subQ162,subQ161,subQ160,subQ159,subQ158,subQ157,subQ156,subQ155,subQ154,subQ153,subQ152,subQ151,subQ150,subQ149])],"isStart":false}),makeQuery(id+"F29.opExtrude","CAP_FACE",FACE,{"disambiguationData":[OSD([subQ148,subQ147,subQ146,subQ145,subQ144,subQ143,subQ142,subQ141,subQ140,subQ139,subQ138,subQ137,subQ136,subQ135,subQ134,subQ133,subQ132,subQ131,subQ130,subQ129,subQ128,subQ127,subQ126,subQ125,subQ124,subQ123,subQ122,subQ121,subQ120,subQ119,subQ118,subQ117,subQ116,subQ115,subQ114,subQ113,subQ112,subQ111,subQ110,subQ109,subQ108,subQ107,subQ106,subQ105,subQ104,subQ103,subQ102,subQ101,subQ100])],"isStart":false}),makeQuery(id+"F29.opExtrude","CAP_FACE",FACE,{"disambiguationData":[OSD([subQ99,subQ98,subQ97,subQ96,subQ95,subQ94,subQ93,subQ92,subQ91,subQ90,subQ89,subQ88,subQ87,subQ86,subQ85,subQ84,subQ83,subQ82,subQ81,subQ80,subQ79,subQ78,subQ77,subQ76,subQ75,subQ74,subQ73,subQ72,subQ71,subQ70,subQ69,subQ68,subQ67,subQ66,subQ65,subQ64,subQ63,subQ62,subQ61,subQ60,subQ59,subQ58,subQ57,subQ56,subQ55,subQ54,subQ53,subQ52,subQ51,subQ50,subQ49,subQ48,subQ47,subQ46,subQ45,subQ44])],"isStart":false}),makeQuery(id+"F29.opExtrude","CAP_FACE",FACE,{"disambiguationData":[OSD([subQ43,subQ42,subQ41,subQ40,subQ39,subQ38,subQ37,subQ36,subQ35,subQ34,subQ33,subQ32,subQ31,subQ30,subQ29,subQ28,subQ27,subQ26,subQ25,subQ24,subQ23,subQ22,subQ21,subQ20,subQ19,subQ18,subQ17,subQ16,subQ15,subQ14,subQ13,subQ12,subQ11,subQ10,subQ9,subQ8,subQ7,subQ6,subQ5,subQ4,subQ3,subQ2,subQ1,subQ0])],"isStart":false})]});}
            extrude(context, id + "F43", {"entities" : qUnion([Q0]), "operationType" : NewBodyOperationType.ADD, "endBound" : BoundingType.UP_TO_SURFACE, "endBoundEntityFace" : qUnion([Q1]), "depth" : 25 * mm});
        }
        {
            var Q0;
            {var subQ0=sQuery(id+"F0.wireOp",EDGE,"E7.rect.right");var subQ2=sQuery(id+"F0.wireOp",EDGE,"E7.rect.bottom");var subQ3=makeQuery(id+"F1.opExtrude","SWEPT_FACE",FACE,{"disambiguationData":[OSD([subQ2])]});var subQ8=sQuery(id+"F0.wireOp",EDGE,"E7.rect.left");var subQ17=sQuery(id+"F0.wireOp",EDGE,"E7.rect.top");var subQ19=sQuery(id+"F0.wireOp",EDGE,"E5.MirrorC");var subQ20=sQuery(id+"F0.wireOp",EDGE,"E3");var subQ21=sQuery(id+"F0.wireOp",EDGE,"E2");var subQ22=sQuery(id+"F0.wireOp",EDGE,"E1");var subQ23=makeQuery(id+"F1.opExtrude","CAP_FACE",FACE,{"disambiguationData":[OSD([subQ22,subQ21,subQ20,subQ19,subQ2,subQ17,subQ8,subQ0])],"isStart":true});Q0=makeQuery(id+"F26.boolean.opBoolean","MERGE",FACE,{"derivedFrom":[makeQuery(id+"F6.opShell","OFFSET_FACE",FACE,{"disambiguationData":[OSD([subQ22,subQ21,subQ20,subQ19,subQ2,subQ17,subQ8,subQ0]),TDD([subQ23]),OD(2.0)]}),makeQuery(id+"F14.boolean.opBoolean","SPLIT",FACE,{"disambiguationData":[TD([makeQuery(id+"F1.opExtrude","SWEPT_FACE",FACE,{"disambiguationData":[OSD([subQ22])]})])],"derivedFrom":makeQuery(id+"F6.opShell","OFFSET_FACE",FACE,{"disambiguationData":[OSD([subQ22,subQ21,subQ20,subQ19,subQ2,subQ17,subQ8,subQ0]),TDD([subQ23]),OD(0.0)]})}),makeQuery(id+"F14.boolean.opBoolean","SPLIT",FACE,{"disambiguationData":[TD([subQ3])],"derivedFrom":makeQuery(id+"F10.boolean.opBoolean","SPLIT",FACE,{"disambiguationData":[TD([subQ3])],"derivedFrom":makeQuery(id+"F6.opShell","OFFSET_FACE",FACE,{"disambiguationData":[OSD([subQ22,subQ21,subQ20,subQ19,subQ2,subQ17,subQ8,subQ0]),TDD([subQ23]),OD(3.0)]})})}),makeQuery(id+"F26.opExtrude","CAP_FACE",FACE,{"disambiguationData":[OSD([sQuery(id+"F25.wireOp",EDGE,"E102.top"),sQuery(id+"F25.wireOp",EDGE,"E102.left"),sQuery(id+"F25.wireOp",EDGE,"E102.right"),sQuery(id+"F25.wireOp",EDGE,"E103.bottom"),sQuery(id+"F25.wireOp",EDGE,"E103.top"),sQuery(id+"F25.wireOp",EDGE,"E103.right"),sQuery(id+"F25.wireOp",EDGE,"E102.bottom"),sQuery(id+"F25.wireOp",EDGE,"E107.top"),sQuery(id+"F25.wireOp",EDGE,"E107.left"),sQuery(id+"F25.wireOp",EDGE,"E107.right")])],"isStart":true}),makeQuery(id+"F26.opExtrude","CAP_FACE",FACE,{"disambiguationData":[OSD([sQuery(id+"F25.wireOp",EDGE,"E105.bottom"),sQuery(id+"F25.wireOp",EDGE,"E105.top"),sQuery(id+"F25.wireOp",EDGE,"E105.left"),sQuery(id+"F25.wireOp",EDGE,"E105.right"),sQuery(id+"F25.wireOp",EDGE,"E106.bottom"),sQuery(id+"F25.wireOp",EDGE,"E106.top"),sQuery(id+"F25.wireOp",EDGE,"E106.right")])],"isStart":true})]});}
            cPlane(context, id + "F44", {"entities" : qUnion([Q0]), "cplaneType" : CPlaneType.OFFSET, "offset" : 0.6 * mm, "oppositeDirection" : true, "width" : 150 * mm, "height" : 150 * mm});
        }
        {
            var Q0;
            Q0=qCreatedBy(id+"F44.planeOp",FACE);
            var sketch = newSketch(context, id + "F45", { "sketchPlane" : qUnion([Q0])});
            skLineSegment(sketch, "E891.bottom", {"start": v(-24.07, 22.32) * mm, "end": v(-9.14, 22.32) * mm});
            skLineSegment(sketch, "E891.top", {"start": v(-24.07, -4.65) * mm, "end": v(-9.14, -4.65) * mm});
            skLineSegment(sketch, "E891.left", {"start": v(-24.07, 22.32) * mm, "end": v(-24.07, -4.65) * mm});
            skLineSegment(sketch, "E891.right", {"start": v(-9.14, 22.32) * mm, "end": v(-9.14, -4.65) * mm});
            skSolve(sketch);
        }
        {
            var Q0;
            Q0=qSketchRegion(id+"F45",true);
            extrude(context, id + "F46", {"entities" : qUnion([Q0]), "operationType" : NewBodyOperationType.ADD, "depth" : 0.6 * mm});
        }
        {
            var Q0;
            Q0=qCreatedBy(makeId("Top.planeOp"),FACE);
            var sketch = newSketch(context, id + "F47", { "sketchPlane" : qUnion([Q0])});
            skLineSegment(sketch, "E892.bottom", {"start": v(-32.16, -19.74) * mm, "end": v(-31.86, -19.74) * mm});
            skLineSegment(sketch, "E892.top", {"start": v(-32.16, -29.43) * mm, "end": v(-31.86, -29.43) * mm});
            skLineSegment(sketch, "E892.left", {"start": v(-32.16, -19.74) * mm, "end": v(-32.16, -29.43) * mm});
            skLineSegment(sketch, "E892.right", {"start": v(-31.86, -19.74) * mm, "end": v(-31.86, -29.43) * mm});
            skLineSegment(sketch, "E893.bottom", {"start": v(-34.1, 3.13) * mm, "end": v(-31.72, 3.13) * mm});
            skLineSegment(sketch, "E893.top", {"start": v(-34.1, 0.35) * mm, "end": v(-31.72, 0.35) * mm});
            skLineSegment(sketch, "E893.left", {"start": v(-34.1, 3.13) * mm, "end": v(-34.1, 0.35) * mm});
            skLineSegment(sketch, "E893.right", {"start": v(-31.72, 3.13) * mm, "end": v(-31.72, 0.35) * mm});
            skLineSegment(sketch, "E894.bottom", {"start": v(-34.13, -7.9) * mm, "end": v(-31.72, -7.9) * mm});
            skLineSegment(sketch, "E894.top", {"start": v(-34.13, -10.8) * mm, "end": v(-31.72, -10.8) * mm});
            skLineSegment(sketch, "E894.left", {"start": v(-34.13, -7.9) * mm, "end": v(-34.13, -10.8) * mm});
            skLineSegment(sketch, "E894.right", {"start": v(-31.72, -7.9) * mm, "end": v(-31.72, -10.8) * mm});
            skSolve(sketch);
        }
        {
            var Q0;
            Q0=qSketchRegion(id+"F47",true);
            var Q1;
            Q1=makeQuery(id+"F35.boolean.opBoolean","MERGE",FACE,{"derivedFrom":[makeQuery(id+"F3.boolean.opBoolean","COPY",FACE,{"derivedFrom":makeQuery(id+"F3.opExtrude","SWEPT_FACE",FACE,{"disambiguationData":[OSD([sQuery(id+"F2.wireOp",EDGE,"E14")])]})}),makeQuery(id+"F35.opExtrude","CAP_FACE",FACE,{"disambiguationData":[OSD([sQuery(id+"F34.wireOp",EDGE,"E864")])],"isStart":false}),makeQuery(id+"F35.opExtrude","CAP_FACE",FACE,{"disambiguationData":[OSD([sQuery(id+"F34.wireOp",EDGE,"E865")])],"isStart":false})]});
            extrude(context, id + "F48", {"entities" : qUnion([Q0]), "operationType" : NewBodyOperationType.ADD, "endBound" : BoundingType.UP_TO_SURFACE, "endBoundEntityFace" : qUnion([Q1]), "depth" : 25 * mm});
        }
        {
            var Q0;
            Q0=makeQuery(id+"F35.boolean.opBoolean","MERGE",FACE,{"derivedFrom":[makeQuery(id+"F3.boolean.opBoolean","COPY",FACE,{"derivedFrom":makeQuery(id+"F3.opExtrude","SWEPT_FACE",FACE,{"disambiguationData":[OSD([sQuery(id+"F2.wireOp",EDGE,"E14")])]})}),makeQuery(id+"F35.opExtrude","CAP_FACE",FACE,{"disambiguationData":[OSD([sQuery(id+"F34.wireOp",EDGE,"E864")])],"isStart":false}),makeQuery(id+"F35.opExtrude","CAP_FACE",FACE,{"disambiguationData":[OSD([sQuery(id+"F34.wireOp",EDGE,"E865")])],"isStart":false})]});
            var sketch = newSketch(context, id + "F49", { "sketchPlane" : qUnion([Q0])});
            skText(sketch, "E895", { "text": "12v", "fontName": "OpenSans-Bold.ttf"});
            skText(sketch, "E896", { "text": "L3 L2 L1", "fontName": "OpenSans-Bold.ttf"});
            const initialGuessF49  = {"E895": [0.019, 0, 1, 0, 0.0042], "E896": [-0.00949, -0.00516, 1, 0, 0.00516]};
            skSetInitialGuess(sketch, initialGuessF49);
            skSolve(sketch);
        }
        {
            var Q0;
            Q0=qSketchRegion(id+"F49",true);
            extrude(context, id + "F50", {"entities" : qUnion([Q0]), "depth" : 1.3 * mm});
        }
        {
            var Q0;
            {var subQ1=sQuery(id+"F0.wireOp",EDGE,"E7.rect.top");var subQ2=sQuery(id+"F0.wireOp",EDGE,"E7.rect.right");var subQ9=makeQuery(id+"F1.opExtrude","SWEPT_FACE",FACE,{"disambiguationData":[OSD([subQ1])]});Q0=makeQuery(id+"F19.boolean.opBoolean","SPLIT",FACE,{"disambiguationData":[TD([makeQuery(id+"F1.opExtrude","SWEPT_FACE",FACE,{"disambiguationData":[OSD([subQ2])]})])],"derivedFrom":subQ9});}
            var sketch = newSketch(context, id + "F51", { "sketchPlane" : qUnion([Q0])});
            skText(sketch, "E897", { "text": "S2", "fontName": "OpenSans-Bold.ttf"});
            skText(sketch, "E898", { "text": "S3", "fontName": "OpenSans-Bold.ttf"});
            skText(sketch, "E899", { "text": "S1", "fontName": "OpenSans-Bold.ttf"});
            const initialGuessF51  = {"E897": [0.0049, 0.00582, 1, 0, 0.00474], "E898": [-0.01363, 0, 1, 0, 0.0043], "E899": [0.02768, 0.00016, 1, 0, 0.0043]};
            skSetInitialGuess(sketch, initialGuessF51);
            skSolve(sketch);
        }
        {
            var Q0;
            Q0=qSketchRegion(id+"F51",true);
            extrude(context, id + "F52", {"entities" : qUnion([Q0]), "depth" : 1.2 * mm, "hasSecondDirection" : true, "secondDirectionOppositeDirection" : true, "secondDirectionDepth" : 0.1 * mm});
        }
        {
            var Q0;
            {var subQ0=sQuery(id+"F2.wireOp",EDGE,"E22");var subQ1=sQuery(id+"F2.wireOp",EDGE,"E20");Q0=makeQuery(id+"F38.boolean.opBoolean","MERGE",FACE,{"derivedFrom":[makeQuery(id+"F24.boolean.opBoolean","SPLIT",FACE,{"disambiguationData":[TD([makeQuery(id+"F1.opExtrude","SWEPT_FACE",FACE,{"disambiguationData":[OSD([sQuery(id+"F0.wireOp",EDGE,"E3")])]})])],"derivedFrom":makeQuery(id+"F3.boolean.opBoolean","COPY",FACE,{"derivedFrom":makeQuery(id+"F3.opExtrude","SWEPT_FACE",FACE,{"disambiguationData":[OSD([subQ1,subQ0])]})})}),makeQuery(id+"F38.opExtrude","CAP_FACE",FACE,{"disambiguationData":[OSD([sQuery(id+"F37.wireOp",EDGE,"E866")])],"isStart":false}),makeQuery(id+"F38.opExtrude","CAP_FACE",FACE,{"disambiguationData":[OSD([sQuery(id+"F37.wireOp",EDGE,"E867")])],"isStart":false})]});}
            var sketch = newSketch(context, id + "F53", { "sketchPlane" : qUnion([Q0])});
            skText(sketch, "E900", { "text": "S6", "fontName": "OpenSans-Bold.ttf"});
            const initialGuessF53  = {"E900": [0.00608, -0.02103, 1, 0, 0.00418]};
            skSetInitialGuess(sketch, initialGuessF53);
            skSolve(sketch);
        }
        {
            var Q0;
            Q0=qSketchRegion(id+"F53",true);
            var Q1;
            Q1=makeQuery(id+"F4.opFillet","BLEND_FACE",FACE,{"disambiguationData":[OSD([sQuery(id+"F0.wireOp",EDGE,"E7.rect.left"),sQuery(id+"F2.wireOp",EDGE,"E20"),sQuery(id+"F2.wireOp",EDGE,"E22")])]});
            extrude(context, id + "F54", {"entities" : qUnion([Q0]), "depth" : 1 * mm, "hasSecondDirection" : true, "secondDirectionOppositeDirection" : true, "secondDirectionBoundEntityFace" : qUnion([Q1]), "secondDirectionDepth" : 0.1 * mm});
        }
        {
            var Q0;
            {var subQ1=sQuery(id+"F0.wireOp",EDGE,"E7.rect.left");var subQ3=sQuery(id+"F0.wireOp",EDGE,"E7.rect.bottom");Q0=makeQuery(id+"F9.boolean.opBoolean","SPLIT",FACE,{"disambiguationData":[TD([makeQuery(id+"F1.opExtrude","SWEPT_FACE",FACE,{"disambiguationData":[OSD([subQ3])]})])],"derivedFrom":makeQuery(id+"F1.opExtrude","SWEPT_FACE",FACE,{"disambiguationData":[OSD([subQ1])]})});}
            var sketch = newSketch(context, id + "F55", { "sketchPlane" : qUnion([Q0])});
            skText(sketch, "E901", { "text": "S5", "fontName": "OpenSans-Bold.ttf"});
            skText(sketch, "E902", { "text": "S4", "fontName": "OpenSans-Bold.ttf"});
            const initialGuessF55  = {"E901": [-0.02945, 0.0004, 1, 0, 0.00488], "E902": [0.0066, 0.0004, 1, 0, 0.0048]};
            skSetInitialGuess(sketch, initialGuessF55);
            skSolve(sketch);
        }
        {
            var Q0;
            Q0=qSketchRegion(id+"F55",true);
            extrude(context, id + "F56", {"entities" : qUnion([Q0]), "depth" : 1.2 * mm});
        }
        {
            var Q0;
            {var subQ0=sQuery(id+"F12.wireOp",EDGE,"E51");Q0=makeQuery(id+"F12.imprint","IMPRINT",FACE,{"disambiguationData":[TD([[makeQuery(id+"F12.imprint","IMPRINT",EDGE,{"derivedFrom":subQ0}),-1.0]])]});}
            extrude(context, id + "F57", {"entities" : qUnion([Q0]), "operationType" : NewBodyOperationType.REMOVE, "oppositeDirection" : true, "depth" : 8 * mm});
        }
        {
            var Q0;
            Q0=makeQuery(id+"F0.imprint","IMPRINT",FACE,{"disambiguationData":[TD([[makeQuery(id+"F0.imprint","IMPRINT",EDGE,{"derivedFrom":sQuery(id+"F0.wireOp",EDGE,"E1")}),-1.0]])]});
            var sketch = newSketch(context, id + "F58", { "sketchPlane" : qUnion([Q0])});
            skPoint(sketch, "E903.first.point", {"position": v(6.62, 7.4) * mm});
            skPoint(sketch, "E903.second.point", {"position": v(6.67, 13.38) * mm});
            skPoint(sketch, "E903.third.point", {"position": v(3.73, 10.32) * mm});
            skPoint(sketch, "E904.first.point", {"position": v(17.45, 10.32) * mm});
            skPoint(sketch, "E904.second.point", {"position": v(14.7, 13.34) * mm});
            skPoint(sketch, "E904.third.point", {"position": v(14.7, 7.45) * mm});
            skPoint(sketch, "E905.MirrorP", {"position": v(17.5, 10.32) * mm});
            skPoint(sketch, "E906.MirrorP", {"position": v(14.62, 7.4) * mm});
            skPoint(sketch, "E907.MirrorP", {"position": v(14.57, 13.38) * mm});
            skLineSegment(sketch, "E908", {"start": v(14.46, 6.75) * mm, "end": v(6.63, 6.75) * mm});
            skLineSegment(sketch, "E909", {"start": v(14.66, 13.88) * mm, "end": v(6.96, 13.88) * mm});
            skArc(sketch, "E910.trimOffspring", {"start": v(6.96, 13.88) * mm, "mid": v(3.17, 10.38) * mm, "end": v(6.84, 6.75) * mm});
            skArc(sketch, "E911.trimOffspring", {"start": v(14.27, 13.88) * mm, "mid": v(18.08, 10.42) * mm, "end": v(14.46, 6.75) * mm});
            skPoint(sketch, "E912.orphan", {"position": v(14.5, 10.4) * mm});
            skPoint(sketch, "E913.start.orphan", {"position": v(10.62, 10.36) * mm});
            skCircle(sketch, "E914", {"center": v(6.74, 10.32) * mm, "radius": 2.01 * mm});
            skCircle(sketch, "E915", {"center": v(14.51, 10.32) * mm, "radius": 2.16 * mm});
            skLineSegment(sketch, "E916.trimOffspring", {"start": v(6.52, 13.88) * mm, "end": v(6.5, 13.88) * mm});
            skSolve(sketch);
        }
        {
            var Q0;
            Q0=qSketchRegion(id+"F58",true);
            extrude(context, id + "F59", {"entities" : qUnion([Q0]), "operationType" : NewBodyOperationType.REMOVE, "depth" : 8.2 * mm});
        }
    });
